FCSTD DOCUMENT  (FreeCAD 1.0R39319 (Git))
Label: externalDesign
License: All rights reserved
LicenseURL: http://en.wikipedia.org/wiki/All_rights_reserved
objects: Part::Feature×136, Sketcher::SketchObject×119, Part::MultiFuse×93, Part::Extrusion×87, Part::Fillet×59, Part::Cut×56, Part::FeaturePython×56, Part::Cylinder×50, Part::Loft×17, App::Part×15, Part::Box×14, Part::Sphere×14, Part::Compound×8, Part::Mirroring×2, Part::Part2DObjectPython×2, Part::MultiCommon×1
note: 833 computed .brp shape members not serialized (recipe doc carries the construction recipe); baked Part::Feature solids carry a one-line shape summary decoded from their .brp

FEATURE [Part::Cylinder] Cylinder198  label="tSlotCut"
  Angle = 360
  AttacherType = Attacher::AttachEngine3D
  FirstAngle = 0
  Height = 10
  Placement = pos=(0,-290.956,1.7236) rot=(1,0,0;0.698132rad)
  Radius = 1.63
  SecondAngle = 0
FEATURE [Part::Feature] Part__Feature328  label="srsCut009"
  Placement = pos=(-31.2,-59.5,20.5) rot=(0,0,1;0rad)
  shape: bbox 22.79 x 8 x 17.08 mm, 886 faces (baked)
FEATURE [Sketcher::SketchObject] Sketch332
  ArcFitTolerance = 0
  FullyConstrained = true
  MakeInternals = false
  sketch-geometry (7):
    g0: LineSegment StartX=45 StartY=-77.9423 StartZ=0 EndX=90 EndY=3.3e-15 EndZ=0
    g1: LineSegment StartX=90 StartY=3.3e-15 StartZ=0 EndX=45 EndY=77.9423 EndZ=0
    g2: LineSegment StartX=45 StartY=77.9423 StartZ=0 EndX=-45 EndY=77.9423 EndZ=0
    g3: LineSegment StartX=-45 StartY=77.9423 StartZ=0 EndX=-90 EndY=1.9e-14 EndZ=0
    g4: LineSegment StartX=-90 StartY=1.9e-14 StartZ=0 EndX=-45 EndY=-77.9423 EndZ=0
    g5: LineSegment StartX=-45 StartY=-77.9423 StartZ=0 EndX=45 EndY=-77.9423 EndZ=0
    g6: Circle [constr] CenterX=0 CenterY=0 CenterZ=0 NormalX=0 NormalY=0 NormalZ=1 AngleXU=0 Radius=90
  constraints (16):
    c: Coincident(g0,g1)
    c: Coincident(g1,g2)
    c: Coincident(g2,g3)
    c: Coincident(g3,g4)
    c: Coincident(g4,g5)
    c: Coincident(g5,g0)
    c: Equal(g0, g1-g5) x5
    c: PointOnObject(g0,g6)
    c: PointOnObject(g1,g6)
    c: PointOnObject(g2,g6)
    c: PointOnObject(g3,g6)
    c: PointOnObject(g4,g6)
    c: PointOnObject(g5,g6)
    c: DistanceX(g5,g5) = 90
    c: Horizontal(g5)
    c: Coincident(g6,g-1)
FEATURE [Sketcher::SketchObject] Sketch333
  ArcFitTolerance = 0
  FullyConstrained = true
  MakeInternals = false
  Placement = pos=(0,0,20) rot=(0,0,1;0rad)
  sketch-geometry (7):
    g0: LineSegment StartX=35 StartY=-60.6218 StartZ=0 EndX=70 EndY=2e-16 EndZ=0
    g1: LineSegment StartX=70 StartY=2e-16 StartZ=0 EndX=35 EndY=60.6218 EndZ=0
    g2: LineSegment StartX=35 StartY=60.6218 StartZ=0 EndX=-35 EndY=60.6218 EndZ=0
    g3: LineSegment StartX=-35 StartY=60.6218 StartZ=0 EndX=-70 EndY=-2.1e-15 EndZ=0
    g4: LineSegment StartX=-70 StartY=0 StartZ=0 EndX=-35 EndY=-60.6218 EndZ=0
    g5: LineSegment StartX=-35 StartY=-60.6218 StartZ=0 EndX=35 EndY=-60.6218 EndZ=0
    g6: Circle [constr] CenterX=0 CenterY=0 CenterZ=0 NormalX=0 NormalY=0 NormalZ=1 AngleXU=0 Radius=70
  constraints (16):
    c: Coincident(g0,g1)
    c: Coincident(g1,g2)
    c: Coincident(g2,g3)
    c: Coincident(g3,g4)
    c: Coincident(g4,g5)
    c: Coincident(g5,g0)
    c: Equal(g0, g1-g5) x5
    c: PointOnObject(g0,g6)
    c: PointOnObject(g1,g6)
    c: PointOnObject(g2,g6)
    c: PointOnObject(g3,g6)
    c: PointOnObject(g4,g6)
    c: PointOnObject(g5,g6)
    c: DistanceX(g5,g5) = 70
    c: Horizontal(g5)
    c: Coincident(g6,g-1)
FEATURE [Part::Loft] Loft
  Closed = false
  MaxDegree = 5
  Ruled = false
  Sections = -> [Sketch333,Sketch332]
  Solid = true
FEATURE [Sketcher::SketchObject] Sketch334
  ArcFitTolerance = 0
  FullyConstrained = true
  MakeInternals = false
  sketch-geometry (7):
    g0: LineSegment StartX=45 StartY=-77.9423 StartZ=0 EndX=90 EndY=3.3e-15 EndZ=0
    g1: LineSegment StartX=90 StartY=0 StartZ=0 EndX=45 EndY=77.9423 EndZ=0
    g2: LineSegment StartX=45 StartY=77.9423 StartZ=0 EndX=-45 EndY=77.9423 EndZ=0
    g3: LineSegment StartX=-45 StartY=77.9423 StartZ=0 EndX=-90 EndY=1.9e-14 EndZ=0
    g4: LineSegment StartX=-90 StartY=1.9e-14 StartZ=0 EndX=-45 EndY=-77.9423 EndZ=0
    g5: LineSegment StartX=-45 StartY=-77.9423 StartZ=0 EndX=45 EndY=-77.9423 EndZ=0
    g6: Circle [constr] CenterX=0 CenterY=0 CenterZ=0 NormalX=0 NormalY=0 NormalZ=1 AngleXU=0 Radius=90
  constraints (16):
    c: Coincident(g0,g1)
    c: Coincident(g1,g2)
    c: Coincident(g2,g3)
    c: Coincident(g3,g4)
    c: Coincident(g4,g5)
    c: Coincident(g5,g0)
    c: Equal(g0, g1-g5) x5
    c: PointOnObject(g0,g6)
    c: PointOnObject(g1,g6)
    c: PointOnObject(g2,g6)
    c: PointOnObject(g3,g6)
    c: PointOnObject(g4,g6)
    c: PointOnObject(g5,g6)
    c: DistanceX(g5,g5) = 90
    c: Horizontal(g5)
    c: Coincident(g6,g-1)
FEATURE [Sketcher::SketchObject] Sketch335
  ArcFitTolerance = 0
  FullyConstrained = true
  MakeInternals = false
  Placement = pos=(0,0,20) rot=(0,0,1;0rad)
  sketch-geometry (7):
    g0: LineSegment StartX=35 StartY=-60.6218 StartZ=0 EndX=70 EndY=2e-16 EndZ=0
    g1: LineSegment StartX=70 StartY=2e-16 StartZ=0 EndX=35 EndY=60.6218 EndZ=0
    g2: LineSegment StartX=35 StartY=60.6218 StartZ=0 EndX=-35 EndY=60.6218 EndZ=0
    g3: LineSegment StartX=-35 StartY=60.6218 StartZ=0 EndX=-70 EndY=-2.1e-15 EndZ=0
    g4: LineSegment StartX=-70 StartY=-2.1e-15 StartZ=0 EndX=-35 EndY=-60.6218 EndZ=0
    g5: LineSegment StartX=-35 StartY=-60.6218 StartZ=0 EndX=35 EndY=-60.6218 EndZ=0
    g6: Circle [constr] CenterX=0 CenterY=0 CenterZ=0 NormalX=0 NormalY=0 NormalZ=1 AngleXU=0 Radius=70
  constraints (16):
    c: Coincident(g0,g1)
    c: Coincident(g1,g2)
    c: Coincident(g2,g3)
    c: Coincident(g3,g4)
    c: Coincident(g4,g5)
    c: Coincident(g5,g0)
    c: Equal(g0, g1-g5) x5
    c: PointOnObject(g0,g6)
    c: PointOnObject(g1,g6)
    c: PointOnObject(g2,g6)
    c: PointOnObject(g3,g6)
    c: PointOnObject(g4,g6)
    c: PointOnObject(g5,g6)
    c: DistanceX(g5,g5) = 70
    c: Horizontal(g5)
    c: Coincident(g6,g-1)
FEATURE [Part::Loft] Loft065
  Closed = false
  MaxDegree = 5
  Placement = pos=(0,0,-4) rot=(0,0,1;0rad)
  Ruled = false
  Sections = -> [Sketch335,Sketch334]
  Solid = true
FEATURE [Part::Cut] Cut124  label="flap"
  Base = -> Loft
  Tool = -> Loft065
FEATURE [Part::Fillet] Fillet216
  Base = -> Cut124
  EdgeLinks = -> Cut124 [Edge1,Edge5,Edge6,Edge7,Edge8,Edge9,Edge27,Edge29,Edge31,Edge33,Edge35,Edge36]
  Edges = 12 edges r=5: [Edge1,Edge5,Edge6,Edge7,Edge8,Edge9,Edge27,Edge29,Edge31,Edge33,Edge35,Edge36]
FEATURE [Part::Fillet] Fillet217
  Base = -> Fillet216
  EdgeLinks = -> Fillet216 [Edge2,Edge6,Edge11,Edge12,Edge13,Edge14,Edge15,Edge16,Edge17,Edge18,Edge19,Edge20]
  Edges = 12 edges r=1: [Edge2,Edge6,Edge11,Edge12,Edge13,Edge14,Edge15,Edge16,Edge17,Edge18,Edge19,Edge20]
FEATURE [Part::Fillet] Fillet218
  Base = -> Fillet217
  EdgeLinks = -> Fillet217 [Edge1,Edge3,Edge5,Edge15,Edge17,Edge41,Edge61,Edge63,Edge65,Edge66,Edge69,Edge70]
  Edges = 12 edges r=2: [Edge1,Edge3,Edge5,Edge15,Edge17,Edge41,Edge61,Edge63,Edge65,Edge66,Edge69,Edge70]
FEATURE [Sketcher::SketchObject] Sketch336
  ArcFitTolerance = 0
  FullyConstrained = false
  MakeInternals = false
  sketch-geometry (7):
    g0: LineSegment StartX=32.5172 StartY=-56.2817 StartZ=0 EndX=65 EndY=0.0199031 EndZ=0
    g1: LineSegment StartX=65 StartY=0.0199031 StartZ=0 EndX=32.4828 EndY=56.3016 EndZ=0
    g2: LineSegment StartX=32.4828 StartY=56.3016 StartZ=0 EndX=-32.5172 EndY=56.2817 EndZ=0
    g3: LineSegment StartX=-32.5172 StartY=56.2817 StartZ=0 EndX=-65 EndY=-0.0199031 EndZ=0
    g4: LineSegment StartX=-65 StartY=-0.0199031 StartZ=0 EndX=-32.4828 EndY=-56.3016 EndZ=0
    g5: LineSegment StartX=-32.4828 StartY=-56.3016 StartZ=0 EndX=32.5172 EndY=-56.2817 EndZ=0
    g6: Circle [constr] CenterX=0 CenterY=0 CenterZ=0 NormalX=0 NormalY=0 NormalZ=1 AngleXU=0 Radius=65
  constraints (15):
    c: Coincident(g0,g1)
    c: Coincident(g1,g2)
    c: Coincident(g2,g3)
    c: Coincident(g3,g4)
    c: Coincident(g4,g5)
    c: Coincident(g5,g0)
    c: Equal(g0, g1-g5) x5
    c: PointOnObject(g0,g6)
    c: PointOnObject(g1,g6)
    c: PointOnObject(g2,g6)
    c: PointOnObject(g3,g6)
    c: PointOnObject(g4,g6)
    c: PointOnObject(g5,g6)
    c: Coincident(g6,g-1)
    c: DistanceX(g2,g2) = 65
FEATURE [Part::Extrusion] Extrude137
  Base = -> Sketch336
  Dir = (0,0,1)
  DirMode = 2
  FaceMakerClass = Part::FaceMakerBullseye
  FaceMakerMode = 3
  LengthFwd = 20
  LengthRev = 0
  Solid = true
  Symmetric = false
FEATURE [Part::Cut] Cut125  label="plate"
  Base = -> Fillet218
  Tool = -> Extrude137
FEATURE [Part::Fillet] Fillet219  label="plate001"
  Base = -> Cut125
  EdgeLinks = -> Cut125 [Edge48,Edge49,Edge50,Edge51,Edge52,Edge53,Edge110,Edge111,Edge112,Edge113,Edge114,Edge115,Edge116,Edge117,Edge118,Edge119,Edge120,Edge121]
  Edges = 18 edges r=1.5: [Edge48,Edge49,Edge50,Edge51,Edge52,Edge53,Edge110,Edge111,Edge112,Edge113,Edge114,Edge115,Edge116,Edge117,Edge118,Edge119,Edge120,Edge121]
FEATURE [Sketcher::SketchObject] Sketch337
  ArcFitTolerance = 0
  FullyConstrained = true
  MakeInternals = false
  sketch-geometry (7):
    g0: LineSegment StartX=45 StartY=-77.9423 StartZ=0 EndX=90 EndY=3.3e-15 EndZ=0
    g1: LineSegment StartX=90 StartY=3.3e-15 StartZ=0 EndX=45 EndY=77.9423 EndZ=0
    g2: LineSegment StartX=45 StartY=77.9423 StartZ=0 EndX=-45 EndY=77.9423 EndZ=0
    g3: LineSegment StartX=-45 StartY=77.9423 StartZ=0 EndX=-90 EndY=1.9e-14 EndZ=0
    g4: LineSegment StartX=-90 StartY=1.9e-14 StartZ=0 EndX=-45 EndY=-77.9423 EndZ=0
    g5: LineSegment StartX=-45 StartY=-77.9423 StartZ=0 EndX=45 EndY=-77.9423 EndZ=0
    g6: Circle [constr] CenterX=0 CenterY=0 CenterZ=0 NormalX=0 NormalY=0 NormalZ=1 AngleXU=0 Radius=90
  constraints (16):
    c: Coincident(g0,g1)
    c: Coincident(g1,g2)
    c: Coincident(g2,g3)
    c: Coincident(g3,g4)
    c: Coincident(g4,g5)
    c: Coincident(g5,g0)
    c: Equal(g0, g1-g5) x5
    c: PointOnObject(g0,g6)
    c: PointOnObject(g1,g6)
    c: PointOnObject(g2,g6)
    c: PointOnObject(g3,g6)
    c: PointOnObject(g4,g6)
    c: PointOnObject(g5,g6)
    c: DistanceX(g5,g5) = 90
    c: Horizontal(g5)
    c: Coincident(g6,g-1)
FEATURE [Sketcher::SketchObject] Sketch338
  ArcFitTolerance = 0
  FullyConstrained = true
  MakeInternals = false
  Placement = pos=(0,0,20) rot=(0,0,1;0rad)
  sketch-geometry (7):
    g0: LineSegment StartX=35 StartY=-60.6218 StartZ=0 EndX=70 EndY=2e-16 EndZ=0
    g1: LineSegment StartX=70 StartY=0 StartZ=0 EndX=35 EndY=60.6218 EndZ=0
    g2: LineSegment StartX=35 StartY=60.6218 StartZ=0 EndX=-35 EndY=60.6218 EndZ=0
    g3: LineSegment StartX=-35 StartY=60.6218 StartZ=0 EndX=-70 EndY=-2.1e-15 EndZ=0
    g4: LineSegment StartX=-70 StartY=0 StartZ=0 EndX=-35 EndY=-60.6218 EndZ=0
    g5: LineSegment StartX=-35 StartY=-60.6218 StartZ=0 EndX=35 EndY=-60.6218 EndZ=0
    g6: Circle [constr] CenterX=0 CenterY=0 CenterZ=0 NormalX=0 NormalY=0 NormalZ=1 AngleXU=0 Radius=70
  constraints (16):
    c: Coincident(g0,g1)
    c: Coincident(g1,g2)
    c: Coincident(g2,g3)
    c: Coincident(g3,g4)
    c: Coincident(g4,g5)
    c: Coincident(g5,g0)
    c: Equal(g0, g1-g5) x5
    c: PointOnObject(g0,g6)
    c: PointOnObject(g1,g6)
    c: PointOnObject(g2,g6)
    c: PointOnObject(g3,g6)
    c: PointOnObject(g4,g6)
    c: PointOnObject(g5,g6)
    c: DistanceX(g5,g5) = 70
    c: Horizontal(g5)
    c: Coincident(g6,g-1)
FEATURE [Part::Loft] Loft066
  Closed = false
  MaxDegree = 5
  Ruled = false
  Sections = -> [Sketch338,Sketch337]
  Solid = true
FEATURE [Sketcher::SketchObject] Sketch339
  ArcFitTolerance = 0
  FullyConstrained = true
  MakeInternals = false
  sketch-geometry (7):
    g0: LineSegment StartX=45 StartY=-77.9423 StartZ=0 EndX=90 EndY=3.3e-15 EndZ=0
    g1: LineSegment StartX=90 StartY=0 StartZ=0 EndX=45 EndY=77.9423 EndZ=0
    g2: LineSegment StartX=45 StartY=77.9423 StartZ=0 EndX=-45 EndY=77.9423 EndZ=0
    g3: LineSegment StartX=-45 StartY=77.9423 StartZ=0 EndX=-90 EndY=1.9e-14 EndZ=0
    g4: LineSegment StartX=-90 StartY=1.42e-14 StartZ=0 EndX=-45 EndY=-77.9423 EndZ=0
    g5: LineSegment StartX=-45 StartY=-77.9423 StartZ=0 EndX=45 EndY=-77.9423 EndZ=0
    g6: Circle [constr] CenterX=0 CenterY=0 CenterZ=0 NormalX=0 NormalY=0 NormalZ=1 AngleXU=0 Radius=90
  constraints (16):
    c: Coincident(g0,g1)
    c: Coincident(g1,g2)
    c: Coincident(g2,g3)
    c: Coincident(g3,g4)
    c: Coincident(g4,g5)
    c: Coincident(g5,g0)
    c: Equal(g0, g1-g5) x5
    c: PointOnObject(g0,g6)
    c: PointOnObject(g1,g6)
    c: PointOnObject(g2,g6)
    c: PointOnObject(g3,g6)
    c: PointOnObject(g4,g6)
    c: PointOnObject(g5,g6)
    c: DistanceX(g5,g5) = 90
    c: Horizontal(g5)
    c: Coincident(g6,g-1)
FEATURE [Sketcher::SketchObject] Sketch340
  ArcFitTolerance = 0
  FullyConstrained = true
  MakeInternals = false
  Placement = pos=(0,0,20) rot=(0,0,1;0rad)
  sketch-geometry (7):
    g0: LineSegment StartX=35 StartY=-60.6218 StartZ=0 EndX=70 EndY=2e-16 EndZ=0
    g1: LineSegment StartX=70 StartY=0 StartZ=0 EndX=35 EndY=60.6218 EndZ=0
    g2: LineSegment StartX=35 StartY=60.6218 StartZ=0 EndX=-35 EndY=60.6218 EndZ=0
    g3: LineSegment StartX=-35 StartY=60.6218 StartZ=0 EndX=-70 EndY=-2.1e-15 EndZ=0
    g4: LineSegment StartX=-70 StartY=0 StartZ=0 EndX=-35 EndY=-60.6218 EndZ=0
    g5: LineSegment StartX=-35 StartY=-60.6218 StartZ=0 EndX=35 EndY=-60.6218 EndZ=0
    g6: Circle [constr] CenterX=0 CenterY=0 CenterZ=0 NormalX=0 NormalY=0 NormalZ=1 AngleXU=0 Radius=70
  constraints (16):
    c: Coincident(g0,g1)
    c: Coincident(g1,g2)
    c: Coincident(g2,g3)
    c: Coincident(g3,g4)
    c: Coincident(g4,g5)
    c: Coincident(g5,g0)
    c: Equal(g0, g1-g5) x5
    c: PointOnObject(g0,g6)
    c: PointOnObject(g1,g6)
    c: PointOnObject(g2,g6)
    c: PointOnObject(g3,g6)
    c: PointOnObject(g4,g6)
    c: PointOnObject(g5,g6)
    c: DistanceX(g5,g5) = 70
    c: Horizontal(g5)
    c: Coincident(g6,g-1)
FEATURE [Part::Loft] Loft067
  Closed = false
  MaxDegree = 5
  Placement = pos=(0,0,-4) rot=(0,0,1;0rad)
  Ruled = false
  Sections = -> [Sketch340,Sketch339]
  Solid = true
FEATURE [Part::Cut] Cut126  label="flap001"
  Base = -> Loft066
  Tool = -> Loft067
FEATURE [Part::Fillet] Fillet220
  Base = -> Cut126
  EdgeLinks = -> Cut126 [Edge1,Edge5,Edge6,Edge7,Edge8,Edge9,Edge27,Edge29,Edge31,Edge33,Edge35,Edge36]
  Edges = 12 edges r=5: [Edge1,Edge5,Edge6,Edge7,Edge8,Edge9,Edge27,Edge29,Edge31,Edge33,Edge35,Edge36]
FEATURE [Part::Fillet] Fillet221
  Base = -> Fillet220
  EdgeLinks = -> Fillet220 [Edge2,Edge6,Edge11,Edge12,Edge13,Edge14,Edge15,Edge16,Edge17,Edge18,Edge19,Edge20]
  Edges = 12 edges r=1: [Edge2,Edge6,Edge11,Edge12,Edge13,Edge14,Edge15,Edge16,Edge17,Edge18,Edge19,Edge20]
FEATURE [Part::Fillet] Fillet222
  Base = -> Fillet221
  EdgeLinks = -> Fillet221 [Edge1,Edge3,Edge5,Edge15,Edge17,Edge41,Edge61,Edge63,Edge65,Edge66,Edge69,Edge70]
  Edges = 12 edges r=2: [Edge1,Edge3,Edge5,Edge15,Edge17,Edge41,Edge61,Edge63,Edge65,Edge66,Edge69,Edge70]
FEATURE [Sketcher::SketchObject] Sketch341
  ArcFitTolerance = 0
  FullyConstrained = false
  MakeInternals = false
  sketch-geometry (7):
    g0: LineSegment StartX=32.5172 StartY=-56.2817 StartZ=0 EndX=65 EndY=0.0199031 EndZ=0
    g1: LineSegment StartX=65 StartY=0.0199031 StartZ=0 EndX=32.4828 EndY=56.3016 EndZ=0
    g2: LineSegment StartX=32.4828 StartY=56.3016 StartZ=0 EndX=-32.5172 EndY=56.2817 EndZ=0
    g3: LineSegment StartX=-32.5172 StartY=56.2817 StartZ=0 EndX=-65 EndY=-0.0199031 EndZ=0
    g4: LineSegment StartX=-65 StartY=-0.0199031 StartZ=0 EndX=-32.4828 EndY=-56.3016 EndZ=0
    g5: LineSegment StartX=-32.4828 StartY=-56.3016 StartZ=0 EndX=32.5172 EndY=-56.2817 EndZ=0
    g6: Circle [constr] CenterX=0 CenterY=0 CenterZ=0 NormalX=0 NormalY=0 NormalZ=1 AngleXU=0 Radius=65
  constraints (15):
    c: Coincident(g0,g1)
    c: Coincident(g1,g2)
    c: Coincident(g2,g3)
    c: Coincident(g3,g4)
    c: Coincident(g4,g5)
    c: Coincident(g5,g0)
    c: Equal(g0, g1-g5) x5
    c: PointOnObject(g0,g6)
    c: PointOnObject(g1,g6)
    c: PointOnObject(g2,g6)
    c: PointOnObject(g3,g6)
    c: PointOnObject(g4,g6)
    c: PointOnObject(g5,g6)
    c: Coincident(g6,g-1)
    c: DistanceX(g2,g2) = 65
FEATURE [Part::Extrusion] Extrude138
  Base = -> Sketch341
  Dir = (0,0,1)
  DirMode = 2
  FaceMakerClass = Part::FaceMakerBullseye
  FaceMakerMode = 3
  LengthFwd = 20
  LengthRev = 0
  Solid = true
  Symmetric = false
FEATURE [Part::Cut] Cut127  label="plate002"
  Base = -> Fillet222
  Tool = -> Extrude138
FEATURE [Part::Fillet] Fillet223  label="plate003"
  Base = -> Cut127
  EdgeLinks = -> Cut127 [Edge48,Edge49,Edge50,Edge51,Edge52,Edge53,Edge110,Edge111,Edge112,Edge113,Edge114,Edge115,Edge116,Edge117,Edge118,Edge119,Edge120,Edge121]
  Edges = 18 edges r=1.5: [Edge48,Edge49,Edge50,Edge51,Edge52,Edge53,Edge110,Edge111,Edge112,Edge113,Edge114,Edge115,Edge116,Edge117,Edge118,Edge119,Edge120,Edge121]
  Placement = pos=(0,0,18) rot=(0,0,1;0rad)
FEATURE [Sketcher::SketchObject] Sketch342
  ArcFitTolerance = 0
  FullyConstrained = true
  MakeInternals = false
  sketch-geometry (7):
    g0: LineSegment StartX=45 StartY=-77.9423 StartZ=0 EndX=90 EndY=3.3e-15 EndZ=0
    g1: LineSegment StartX=90 StartY=0 StartZ=0 EndX=45 EndY=77.9423 EndZ=0
    g2: LineSegment StartX=45 StartY=77.9423 StartZ=0 EndX=-45 EndY=77.9423 EndZ=0
    g3: LineSegment StartX=-45 StartY=77.9423 StartZ=0 EndX=-90 EndY=1.9e-14 EndZ=0
    g4: LineSegment StartX=-90 StartY=1.9e-14 StartZ=0 EndX=-45 EndY=-77.9423 EndZ=0
    g5: LineSegment StartX=-45 StartY=-77.9423 StartZ=0 EndX=45 EndY=-77.9423 EndZ=0
    g6: Circle [constr] CenterX=0 CenterY=0 CenterZ=0 NormalX=0 NormalY=0 NormalZ=1 AngleXU=0 Radius=90
  constraints (16):
    c: Coincident(g0,g1)
    c: Coincident(g1,g2)
    c: Coincident(g2,g3)
    c: Coincident(g3,g4)
    c: Coincident(g4,g5)
    c: Coincident(g5,g0)
    c: Equal(g0, g1-g5) x5
    c: PointOnObject(g0,g6)
    c: PointOnObject(g1,g6)
    c: PointOnObject(g2,g6)
    c: PointOnObject(g3,g6)
    c: PointOnObject(g4,g6)
    c: PointOnObject(g5,g6)
    c: DistanceX(g5,g5) = 90
    c: Horizontal(g5)
    c: Coincident(g6,g-1)
FEATURE [Sketcher::SketchObject] Sketch343
  ArcFitTolerance = 0
  FullyConstrained = true
  MakeInternals = false
  Placement = pos=(0,0,20) rot=(0,0,1;0rad)
  sketch-geometry (7):
    g0: LineSegment StartX=35 StartY=-60.6218 StartZ=0 EndX=70 EndY=2e-16 EndZ=0
    g1: LineSegment StartX=70 StartY=0 StartZ=0 EndX=35 EndY=60.6218 EndZ=0
    g2: LineSegment StartX=35 StartY=60.6218 StartZ=0 EndX=-35 EndY=60.6218 EndZ=0
    g3: LineSegment StartX=-35 StartY=60.6218 StartZ=0 EndX=-70 EndY=-2.1e-15 EndZ=0
    g4: LineSegment StartX=-70 StartY=-2.1e-15 StartZ=0 EndX=-35 EndY=-60.6218 EndZ=0
    g5: LineSegment StartX=-35 StartY=-60.6218 StartZ=0 EndX=35 EndY=-60.6218 EndZ=0
    g6: Circle [constr] CenterX=0 CenterY=0 CenterZ=0 NormalX=0 NormalY=0 NormalZ=1 AngleXU=0 Radius=70
  constraints (16):
    c: Coincident(g0,g1)
    c: Coincident(g1,g2)
    c: Coincident(g2,g3)
    c: Coincident(g3,g4)
    c: Coincident(g4,g5)
    c: Coincident(g5,g0)
    c: Equal(g0, g1-g5) x5
    c: PointOnObject(g0,g6)
    c: PointOnObject(g1,g6)
    c: PointOnObject(g2,g6)
    c: PointOnObject(g3,g6)
    c: PointOnObject(g4,g6)
    c: PointOnObject(g5,g6)
    c: DistanceX(g5,g5) = 70
    c: Horizontal(g5)
    c: Coincident(g6,g-1)
FEATURE [Part::Loft] Loft068
  Closed = false
  MaxDegree = 5
  Ruled = false
  Sections = -> [Sketch343,Sketch342]
  Solid = true
FEATURE [Sketcher::SketchObject] Sketch344
  ArcFitTolerance = 0
  FullyConstrained = true
  MakeInternals = false
  sketch-geometry (7):
    g0: LineSegment StartX=45 StartY=-77.9423 StartZ=0 EndX=90 EndY=3.3e-15 EndZ=0
    g1: LineSegment StartX=90 StartY=3.3e-15 StartZ=0 EndX=45 EndY=77.9423 EndZ=0
    g2: LineSegment StartX=45 StartY=77.9423 StartZ=0 EndX=-45 EndY=77.9423 EndZ=0
    g3: LineSegment StartX=-45 StartY=77.9423 StartZ=0 EndX=-90 EndY=1.9e-14 EndZ=0
    g4: LineSegment StartX=-90 StartY=1.42e-14 StartZ=0 EndX=-45 EndY=-77.9423 EndZ=0
    g5: LineSegment StartX=-45 StartY=-77.9423 StartZ=0 EndX=45 EndY=-77.9423 EndZ=0
    g6: Circle [constr] CenterX=0 CenterY=0 CenterZ=0 NormalX=0 NormalY=0 NormalZ=1 AngleXU=0 Radius=90
  constraints (16):
    c: Coincident(g0,g1)
    c: Coincident(g1,g2)
    c: Coincident(g2,g3)
    c: Coincident(g3,g4)
    c: Coincident(g4,g5)
    c: Coincident(g5,g0)
    c: Equal(g0, g1-g5) x5
    c: PointOnObject(g0,g6)
    c: PointOnObject(g1,g6)
    c: PointOnObject(g2,g6)
    c: PointOnObject(g3,g6)
    c: PointOnObject(g4,g6)
    c: PointOnObject(g5,g6)
    c: DistanceX(g5,g5) = 90
    c: Horizontal(g5)
    c: Coincident(g6,g-1)
FEATURE [Sketcher::SketchObject] Sketch345
  ArcFitTolerance = 0
  FullyConstrained = true
  MakeInternals = false
  Placement = pos=(0,0,20) rot=(0,0,1;0rad)
  sketch-geometry (7):
    g0: LineSegment StartX=35 StartY=-60.6218 StartZ=0 EndX=70 EndY=2e-16 EndZ=0
    g1: LineSegment StartX=70 StartY=0 StartZ=0 EndX=35 EndY=60.6218 EndZ=0
    g2: LineSegment StartX=35 StartY=60.6218 StartZ=0 EndX=-35 EndY=60.6218 EndZ=0
    g3: LineSegment StartX=-35 StartY=60.6218 StartZ=0 EndX=-70 EndY=-2.1e-15 EndZ=0
    g4: LineSegment StartX=-70 StartY=0 StartZ=0 EndX=-35 EndY=-60.6218 EndZ=0
    g5: LineSegment StartX=-35 StartY=-60.6218 StartZ=0 EndX=35 EndY=-60.6218 EndZ=0
    g6: Circle [constr] CenterX=0 CenterY=0 CenterZ=0 NormalX=0 NormalY=0 NormalZ=1 AngleXU=0 Radius=70
  constraints (16):
    c: Coincident(g0,g1)
    c: Coincident(g1,g2)
    c: Coincident(g2,g3)
    c: Coincident(g3,g4)
    c: Coincident(g4,g5)
    c: Coincident(g5,g0)
    c: Equal(g0, g1-g5) x5
    c: PointOnObject(g0,g6)
    c: PointOnObject(g1,g6)
    c: PointOnObject(g2,g6)
    c: PointOnObject(g3,g6)
    c: PointOnObject(g4,g6)
    c: PointOnObject(g5,g6)
    c: DistanceX(g5,g5) = 70
    c: Horizontal(g5)
    c: Coincident(g6,g-1)
FEATURE [Part::Loft] Loft069
  Closed = false
  MaxDegree = 5
  Placement = pos=(0,0,-4) rot=(0,0,1;0rad)
  Ruled = false
  Sections = -> [Sketch345,Sketch344]
  Solid = true
FEATURE [Part::Cut] Cut128  label="flap002"
  Base = -> Loft068
  Tool = -> Loft069
FEATURE [Part::Fillet] Fillet224
  Base = -> Cut128
  EdgeLinks = -> Cut128 [Edge1,Edge5,Edge6,Edge7,Edge8,Edge9,Edge27,Edge29,Edge31,Edge33,Edge35,Edge36]
  Edges = 12 edges r=5: [Edge1,Edge5,Edge6,Edge7,Edge8,Edge9,Edge27,Edge29,Edge31,Edge33,Edge35,Edge36]
FEATURE [Part::Fillet] Fillet225
  Base = -> Fillet224
  EdgeLinks = -> Fillet224 [Edge2,Edge6,Edge11,Edge12,Edge13,Edge14,Edge15,Edge16,Edge17,Edge18,Edge19,Edge20]
  Edges = 12 edges r=1: [Edge2,Edge6,Edge11,Edge12,Edge13,Edge14,Edge15,Edge16,Edge17,Edge18,Edge19,Edge20]
FEATURE [Part::Fillet] Fillet226
  Base = -> Fillet225
  EdgeLinks = -> Fillet225 [Edge1,Edge3,Edge5,Edge15,Edge17,Edge41,Edge61,Edge63,Edge65,Edge66,Edge69,Edge70]
  Edges = 12 edges r=2: [Edge1,Edge3,Edge5,Edge15,Edge17,Edge41,Edge61,Edge63,Edge65,Edge66,Edge69,Edge70]
FEATURE [Sketcher::SketchObject] Sketch346
  ArcFitTolerance = 0
  FullyConstrained = false
  MakeInternals = false
  sketch-geometry (7):
    g0: LineSegment StartX=32.5172 StartY=-56.2817 StartZ=0 EndX=65 EndY=0.0199031 EndZ=0
    g1: LineSegment StartX=65 StartY=0.0199031 StartZ=0 EndX=32.4828 EndY=56.3016 EndZ=0
    g2: LineSegment StartX=32.4828 StartY=56.3016 StartZ=0 EndX=-32.5172 EndY=56.2817 EndZ=0
    g3: LineSegment StartX=-32.5172 StartY=56.2817 StartZ=0 EndX=-65 EndY=-0.0199031 EndZ=0
    g4: LineSegment StartX=-65 StartY=-0.0199031 StartZ=0 EndX=-32.4828 EndY=-56.3016 EndZ=0
    g5: LineSegment StartX=-32.4828 StartY=-56.3016 StartZ=0 EndX=32.5172 EndY=-56.2817 EndZ=0
    g6: Circle [constr] CenterX=0 CenterY=0 CenterZ=0 NormalX=0 NormalY=0 NormalZ=1 AngleXU=0 Radius=65
  constraints (15):
    c: Coincident(g0,g1)
    c: Coincident(g1,g2)
    c: Coincident(g2,g3)
    c: Coincident(g3,g4)
    c: Coincident(g4,g5)
    c: Coincident(g5,g0)
    c: Equal(g0, g1-g5) x5
    c: PointOnObject(g0,g6)
    c: PointOnObject(g1,g6)
    c: PointOnObject(g2,g6)
    c: PointOnObject(g3,g6)
    c: PointOnObject(g4,g6)
    c: PointOnObject(g5,g6)
    c: Coincident(g6,g-1)
    c: DistanceX(g2,g2) = 65
FEATURE [Part::Extrusion] Extrude139
  Base = -> Sketch346
  Dir = (0,0,1)
  DirMode = 2
  FaceMakerClass = Part::FaceMakerBullseye
  FaceMakerMode = 3
  LengthFwd = 20
  LengthRev = 0
  Solid = true
  Symmetric = false
FEATURE [Part::Cut] Cut129  label="plate004"
  Base = -> Fillet226
  Tool = -> Extrude139
FEATURE [Part::Fillet] Fillet227  label="plate005"
  Base = -> Cut129
  EdgeLinks = -> Cut129 [Edge48,Edge49,Edge50,Edge51,Edge52,Edge53,Edge110,Edge111,Edge112,Edge113,Edge114,Edge115,Edge116,Edge117,Edge118,Edge119,Edge120,Edge121]
  Edges = 18 edges r=1.5: [Edge48,Edge49,Edge50,Edge51,Edge52,Edge53,Edge110,Edge111,Edge112,Edge113,Edge114,Edge115,Edge116,Edge117,Edge118,Edge119,Edge120,Edge121]
  Placement = pos=(0,0,36) rot=(0,0,1;0rad)
FEATURE [Sketcher::SketchObject] Sketch347
  ArcFitTolerance = 0
  FullyConstrained = true
  MakeInternals = false
  sketch-geometry (7):
    g0: LineSegment StartX=45 StartY=-77.9423 StartZ=0 EndX=90 EndY=3.3e-15 EndZ=0
    g1: LineSegment StartX=90 StartY=0 StartZ=0 EndX=45 EndY=77.9423 EndZ=0
    g2: LineSegment StartX=45 StartY=77.9423 StartZ=0 EndX=-45 EndY=77.9423 EndZ=0
    g3: LineSegment StartX=-45 StartY=77.9423 StartZ=0 EndX=-90 EndY=1.9e-14 EndZ=0
    g4: LineSegment StartX=-90 StartY=1.9e-14 StartZ=0 EndX=-45 EndY=-77.9423 EndZ=0
    g5: LineSegment StartX=-45 StartY=-77.9423 StartZ=0 EndX=45 EndY=-77.9423 EndZ=0
    g6: Circle [constr] CenterX=0 CenterY=0 CenterZ=0 NormalX=0 NormalY=0 NormalZ=1 AngleXU=0 Radius=90
  constraints (16):
    c: Coincident(g0,g1)
    c: Coincident(g1,g2)
    c: Coincident(g2,g3)
    c: Coincident(g3,g4)
    c: Coincident(g4,g5)
    c: Coincident(g5,g0)
    c: Equal(g0, g1-g5) x5
    c: PointOnObject(g0,g6)
    c: PointOnObject(g1,g6)
    c: PointOnObject(g2,g6)
    c: PointOnObject(g3,g6)
    c: PointOnObject(g4,g6)
    c: PointOnObject(g5,g6)
    c: DistanceX(g5,g5) = 90
    c: Horizontal(g5)
    c: Coincident(g6,g-1)
FEATURE [Sketcher::SketchObject] Sketch348
  ArcFitTolerance = 0
  FullyConstrained = true
  MakeInternals = false
  Placement = pos=(0,0,20) rot=(0,0,1;0rad)
  sketch-geometry (7):
    g0: LineSegment StartX=35 StartY=-60.6218 StartZ=0 EndX=70 EndY=2e-16 EndZ=0
    g1: LineSegment StartX=70 StartY=0 StartZ=0 EndX=35 EndY=60.6218 EndZ=0
    g2: LineSegment StartX=35 StartY=60.6218 StartZ=0 EndX=-35 EndY=60.6218 EndZ=0
    g3: LineSegment StartX=-35 StartY=60.6218 StartZ=0 EndX=-70 EndY=-2.1e-15 EndZ=0
    g4: LineSegment StartX=-70 StartY=-2.1e-15 StartZ=0 EndX=-35 EndY=-60.6218 EndZ=0
    g5: LineSegment StartX=-35 StartY=-60.6218 StartZ=0 EndX=35 EndY=-60.6218 EndZ=0
    g6: Circle [constr] CenterX=0 CenterY=0 CenterZ=0 NormalX=0 NormalY=0 NormalZ=1 AngleXU=0 Radius=70
  constraints (16):
    c: Coincident(g0,g1)
    c: Coincident(g1,g2)
    c: Coincident(g2,g3)
    c: Coincident(g3,g4)
    c: Coincident(g4,g5)
    c: Coincident(g5,g0)
    c: Equal(g0, g1-g5) x5
    c: PointOnObject(g0,g6)
    c: PointOnObject(g1,g6)
    c: PointOnObject(g2,g6)
    c: PointOnObject(g3,g6)
    c: PointOnObject(g4,g6)
    c: PointOnObject(g5,g6)
    c: DistanceX(g5,g5) = 70
    c: Horizontal(g5)
    c: Coincident(g6,g-1)
FEATURE [Part::Loft] Loft070
  Closed = false
  MaxDegree = 5
  Ruled = false
  Sections = -> [Sketch348,Sketch347]
  Solid = true
FEATURE [Sketcher::SketchObject] Sketch349
  ArcFitTolerance = 0
  FullyConstrained = true
  MakeInternals = false
  sketch-geometry (7):
    g0: LineSegment StartX=45 StartY=-77.9423 StartZ=0 EndX=90 EndY=3.3e-15 EndZ=0
    g1: LineSegment StartX=90 StartY=0 StartZ=0 EndX=45 EndY=77.9423 EndZ=0
    g2: LineSegment StartX=45 StartY=77.9423 StartZ=0 EndX=-45 EndY=77.9423 EndZ=0
    g3: LineSegment StartX=-45 StartY=77.9423 StartZ=0 EndX=-90 EndY=1.9e-14 EndZ=0
    g4: LineSegment StartX=-90 StartY=1.9e-14 StartZ=0 EndX=-45 EndY=-77.9423 EndZ=0
    g5: LineSegment StartX=-45 StartY=-77.9423 StartZ=0 EndX=45 EndY=-77.9423 EndZ=0
    g6: Circle [constr] CenterX=0 CenterY=0 CenterZ=0 NormalX=0 NormalY=0 NormalZ=1 AngleXU=0 Radius=90
  constraints (16):
    c: Coincident(g0,g1)
    c: Coincident(g1,g2)
    c: Coincident(g2,g3)
    c: Coincident(g3,g4)
    c: Coincident(g4,g5)
    c: Coincident(g5,g0)
    c: Equal(g0, g1-g5) x5
    c: PointOnObject(g0,g6)
    c: PointOnObject(g1,g6)
    c: PointOnObject(g2,g6)
    c: PointOnObject(g3,g6)
    c: PointOnObject(g4,g6)
    c: PointOnObject(g5,g6)
    c: DistanceX(g5,g5) = 90
    c: Horizontal(g5)
    c: Coincident(g6,g-1)
FEATURE [Sketcher::SketchObject] Sketch350
  ArcFitTolerance = 0
  FullyConstrained = true
  MakeInternals = false
  Placement = pos=(0,0,20) rot=(0,0,1;0rad)
  sketch-geometry (7):
    g0: LineSegment StartX=35 StartY=-60.6218 StartZ=0 EndX=70 EndY=2e-16 EndZ=0
    g1: LineSegment StartX=70 StartY=0 StartZ=0 EndX=35 EndY=60.6218 EndZ=0
    g2: LineSegment StartX=35 StartY=60.6218 StartZ=0 EndX=-35 EndY=60.6218 EndZ=0
    g3: LineSegment StartX=-35 StartY=60.6218 StartZ=0 EndX=-70 EndY=-2.1e-15 EndZ=0
    g4: LineSegment StartX=-70 StartY=-2.1e-15 StartZ=0 EndX=-35 EndY=-60.6218 EndZ=0
    g5: LineSegment StartX=-35 StartY=-60.6218 StartZ=0 EndX=35 EndY=-60.6218 EndZ=0
    g6: Circle [constr] CenterX=0 CenterY=0 CenterZ=0 NormalX=0 NormalY=0 NormalZ=1 AngleXU=0 Radius=70
  constraints (16):
    c: Coincident(g0,g1)
    c: Coincident(g1,g2)
    c: Coincident(g2,g3)
    c: Coincident(g3,g4)
    c: Coincident(g4,g5)
    c: Coincident(g5,g0)
    c: Equal(g0, g1-g5) x5
    c: PointOnObject(g0,g6)
    c: PointOnObject(g1,g6)
    c: PointOnObject(g2,g6)
    c: PointOnObject(g3,g6)
    c: PointOnObject(g4,g6)
    c: PointOnObject(g5,g6)
    c: DistanceX(g5,g5) = 70
    c: Horizontal(g5)
    c: Coincident(g6,g-1)
FEATURE [Part::Loft] Loft071
  Closed = false
  MaxDegree = 5
  Placement = pos=(0,0,-4) rot=(0,0,1;0rad)
  Ruled = false
  Sections = -> [Sketch350,Sketch349]
  Solid = true
FEATURE [Part::Cut] Cut130  label="flap003"
  Base = -> Loft070
  Tool = -> Loft071
FEATURE [Part::Fillet] Fillet228
  Base = -> Cut130
  EdgeLinks = -> Cut130 [Edge1,Edge5,Edge6,Edge7,Edge8,Edge9,Edge27,Edge29,Edge31,Edge33,Edge35,Edge36]
  Edges = 12 edges r=5: [Edge1,Edge5,Edge6,Edge7,Edge8,Edge9,Edge27,Edge29,Edge31,Edge33,Edge35,Edge36]
FEATURE [Part::Fillet] Fillet229
  Base = -> Fillet228
  EdgeLinks = -> Fillet228 [Edge2,Edge6,Edge11,Edge12,Edge13,Edge14,Edge15,Edge16,Edge17,Edge18,Edge19,Edge20]
  Edges = 12 edges r=1: [Edge2,Edge6,Edge11,Edge12,Edge13,Edge14,Edge15,Edge16,Edge17,Edge18,Edge19,Edge20]
FEATURE [Part::Fillet] Fillet230
  Base = -> Fillet229
  EdgeLinks = -> Fillet229 [Edge1,Edge3,Edge5,Edge15,Edge17,Edge41,Edge61,Edge63,Edge65,Edge66,Edge69,Edge70]
  Edges = 12 edges r=2: [Edge1,Edge3,Edge5,Edge15,Edge17,Edge41,Edge61,Edge63,Edge65,Edge66,Edge69,Edge70]
FEATURE [Sketcher::SketchObject] Sketch351
  ArcFitTolerance = 0
  FullyConstrained = false
  MakeInternals = false
  sketch-geometry (7):
    g0: LineSegment StartX=32.5172 StartY=-56.2817 StartZ=0 EndX=65 EndY=0.0199031 EndZ=0
    g1: LineSegment StartX=65 StartY=0.0199031 StartZ=0 EndX=32.4828 EndY=56.3016 EndZ=0
    g2: LineSegment StartX=32.4828 StartY=56.3016 StartZ=0 EndX=-32.5172 EndY=56.2817 EndZ=0
    g3: LineSegment StartX=-32.5172 StartY=56.2817 StartZ=0 EndX=-65 EndY=-0.0199031 EndZ=0
    g4: LineSegment StartX=-65 StartY=-0.0199031 StartZ=0 EndX=-32.4828 EndY=-56.3016 EndZ=0
    g5: LineSegment StartX=-32.4828 StartY=-56.3016 StartZ=0 EndX=32.5172 EndY=-56.2817 EndZ=0
    g6: Circle [constr] CenterX=0 CenterY=0 CenterZ=0 NormalX=0 NormalY=0 NormalZ=1 AngleXU=0 Radius=65
  constraints (15):
    c: Coincident(g0,g1)
    c: Coincident(g1,g2)
    c: Coincident(g2,g3)
    c: Coincident(g3,g4)
    c: Coincident(g4,g5)
    c: Coincident(g5,g0)
    c: Equal(g0, g1-g5) x5
    c: PointOnObject(g0,g6)
    c: PointOnObject(g1,g6)
    c: PointOnObject(g2,g6)
    c: PointOnObject(g3,g6)
    c: PointOnObject(g4,g6)
    c: PointOnObject(g5,g6)
    c: Coincident(g6,g-1)
    c: DistanceX(g2,g2) = 65
FEATURE [Part::Extrusion] Extrude140
  Base = -> Sketch351
  Dir = (0,0,1)
  DirMode = 2
  FaceMakerClass = Part::FaceMakerBullseye
  FaceMakerMode = 3
  LengthFwd = 20
  LengthRev = 0
  Solid = true
  Symmetric = false
FEATURE [Part::Cut] Cut131  label="plate006"
  Base = -> Fillet230
  Tool = -> Extrude140
FEATURE [Part::Fillet] Fillet231  label="plate007"
  Base = -> Cut131
  EdgeLinks = -> Cut131 [Edge48,Edge49,Edge50,Edge51,Edge52,Edge53,Edge110,Edge111,Edge112,Edge113,Edge114,Edge115,Edge116,Edge117,Edge118,Edge119,Edge120,Edge121]
  Edges = 18 edges r=1.5: [Edge48,Edge49,Edge50,Edge51,Edge52,Edge53,Edge110,Edge111,Edge112,Edge113,Edge114,Edge115,Edge116,Edge117,Edge118,Edge119,Edge120,Edge121]
  Placement = pos=(0,0,54) rot=(0,0,1;0rad)
FEATURE [Sketcher::SketchObject] Sketch352
  ArcFitTolerance = 0
  FullyConstrained = true
  MakeInternals = false
  sketch-geometry (7):
    g0: LineSegment StartX=45 StartY=-77.9423 StartZ=0 EndX=90 EndY=3.3e-15 EndZ=0
    g1: LineSegment StartX=90 StartY=0 StartZ=0 EndX=45 EndY=77.9423 EndZ=0
    g2: LineSegment StartX=45 StartY=77.9423 StartZ=0 EndX=-45 EndY=77.9423 EndZ=0
    g3: LineSegment StartX=-45 StartY=77.9423 StartZ=0 EndX=-90 EndY=1.9e-14 EndZ=0
    g4: LineSegment StartX=-90 StartY=1.9e-14 StartZ=0 EndX=-45 EndY=-77.9423 EndZ=0
    g5: LineSegment StartX=-45 StartY=-77.9423 StartZ=0 EndX=45 EndY=-77.9423 EndZ=0
    g6: Circle [constr] CenterX=0 CenterY=0 CenterZ=0 NormalX=0 NormalY=0 NormalZ=1 AngleXU=0 Radius=90
  constraints (16):
    c: Coincident(g0,g1)
    c: Coincident(g1,g2)
    c: Coincident(g2,g3)
    c: Coincident(g3,g4)
    c: Coincident(g4,g5)
    c: Coincident(g5,g0)
    c: Equal(g0, g1-g5) x5
    c: PointOnObject(g0,g6)
    c: PointOnObject(g1,g6)
    c: PointOnObject(g2,g6)
    c: PointOnObject(g3,g6)
    c: PointOnObject(g4,g6)
    c: PointOnObject(g5,g6)
    c: DistanceX(g5,g5) = 90
    c: Horizontal(g5)
    c: Coincident(g6,g-1)
FEATURE [Sketcher::SketchObject] Sketch353
  ArcFitTolerance = 0
  FullyConstrained = true
  MakeInternals = false
  Placement = pos=(0,0,20) rot=(0,0,1;0rad)
  sketch-geometry (7):
    g0: LineSegment StartX=35 StartY=-60.6218 StartZ=0 EndX=70 EndY=2e-16 EndZ=0
    g1: LineSegment StartX=70 StartY=0 StartZ=0 EndX=35 EndY=60.6218 EndZ=0
    g2: LineSegment StartX=35 StartY=60.6218 StartZ=0 EndX=-35 EndY=60.6218 EndZ=0
    g3: LineSegment StartX=-35 StartY=60.6218 StartZ=0 EndX=-70 EndY=-2.1e-15 EndZ=0
    g4: LineSegment StartX=-70 StartY=0 StartZ=0 EndX=-35 EndY=-60.6218 EndZ=0
    g5: LineSegment StartX=-35 StartY=-60.6218 StartZ=0 EndX=35 EndY=-60.6218 EndZ=0
    g6: Circle [constr] CenterX=0 CenterY=0 CenterZ=0 NormalX=0 NormalY=0 NormalZ=1 AngleXU=0 Radius=70
  constraints (16):
    c: Coincident(g0,g1)
    c: Coincident(g1,g2)
    c: Coincident(g2,g3)
    c: Coincident(g3,g4)
    c: Coincident(g4,g5)
    c: Coincident(g5,g0)
    c: Equal(g0, g1-g5) x5
    c: PointOnObject(g0,g6)
    c: PointOnObject(g1,g6)
    c: PointOnObject(g2,g6)
    c: PointOnObject(g3,g6)
    c: PointOnObject(g4,g6)
    c: PointOnObject(g5,g6)
    c: DistanceX(g5,g5) = 70
    c: Horizontal(g5)
    c: Coincident(g6,g-1)
FEATURE [Part::Loft] Loft072
  Closed = false
  MaxDegree = 5
  Ruled = false
  Sections = -> [Sketch353,Sketch352]
  Solid = true
FEATURE [Sketcher::SketchObject] Sketch354
  ArcFitTolerance = 0
  FullyConstrained = true
  MakeInternals = false
  sketch-geometry (7):
    g0: LineSegment StartX=45 StartY=-77.9423 StartZ=0 EndX=90 EndY=3.3e-15 EndZ=0
    g1: LineSegment StartX=90 StartY=0 StartZ=0 EndX=45 EndY=77.9423 EndZ=0
    g2: LineSegment StartX=45 StartY=77.9423 StartZ=0 EndX=-45 EndY=77.9423 EndZ=0
    g3: LineSegment StartX=-45 StartY=77.9423 StartZ=0 EndX=-90 EndY=1.9e-14 EndZ=0
    g4: LineSegment StartX=-90 StartY=1.42e-14 StartZ=0 EndX=-45 EndY=-77.9423 EndZ=0
    g5: LineSegment StartX=-45 StartY=-77.9423 StartZ=0 EndX=45 EndY=-77.9423 EndZ=0
    g6: Circle [constr] CenterX=0 CenterY=0 CenterZ=0 NormalX=0 NormalY=0 NormalZ=1 AngleXU=0 Radius=90
  constraints (16):
    c: Coincident(g0,g1)
    c: Coincident(g1,g2)
    c: Coincident(g2,g3)
    c: Coincident(g3,g4)
    c: Coincident(g4,g5)
    c: Coincident(g5,g0)
    c: Equal(g0, g1-g5) x5
    c: PointOnObject(g0,g6)
    c: PointOnObject(g1,g6)
    c: PointOnObject(g2,g6)
    c: PointOnObject(g3,g6)
    c: PointOnObject(g4,g6)
    c: PointOnObject(g5,g6)
    c: DistanceX(g5,g5) = 90
    c: Horizontal(g5)
    c: Coincident(g6,g-1)
FEATURE [Sketcher::SketchObject] Sketch355
  ArcFitTolerance = 0
  FullyConstrained = true
  MakeInternals = false
  Placement = pos=(0,0,20) rot=(0,0,1;0rad)
  sketch-geometry (7):
    g0: LineSegment StartX=35 StartY=-60.6218 StartZ=0 EndX=70 EndY=2e-16 EndZ=0
    g1: LineSegment StartX=70 StartY=0 StartZ=0 EndX=35 EndY=60.6218 EndZ=0
    g2: LineSegment StartX=35 StartY=60.6218 StartZ=0 EndX=-35 EndY=60.6218 EndZ=0
    g3: LineSegment StartX=-35 StartY=60.6218 StartZ=0 EndX=-70 EndY=-2.1e-15 EndZ=0
    g4: LineSegment StartX=-70 StartY=0 StartZ=0 EndX=-35 EndY=-60.6218 EndZ=0
    g5: LineSegment StartX=-35 StartY=-60.6218 StartZ=0 EndX=35 EndY=-60.6218 EndZ=0
    g6: Circle [constr] CenterX=0 CenterY=0 CenterZ=0 NormalX=0 NormalY=0 NormalZ=1 AngleXU=0 Radius=70
  constraints (16):
    c: Coincident(g0,g1)
    c: Coincident(g1,g2)
    c: Coincident(g2,g3)
    c: Coincident(g3,g4)
    c: Coincident(g4,g5)
    c: Coincident(g5,g0)
    c: Equal(g0, g1-g5) x5
    c: PointOnObject(g0,g6)
    c: PointOnObject(g1,g6)
    c: PointOnObject(g2,g6)
    c: PointOnObject(g3,g6)
    c: PointOnObject(g4,g6)
    c: PointOnObject(g5,g6)
    c: DistanceX(g5,g5) = 70
    c: Horizontal(g5)
    c: Coincident(g6,g-1)
FEATURE [Part::Loft] Loft073
  Closed = false
  MaxDegree = 5
  Placement = pos=(0,0,-4) rot=(0,0,1;0rad)
  Ruled = false
  Sections = -> [Sketch355,Sketch354]
  Solid = true
FEATURE [Part::Cut] Cut132  label="flap004"
  Base = -> Loft072
  Tool = -> Loft073
FEATURE [Part::Fillet] Fillet232
  Base = -> Cut132
  EdgeLinks = -> Cut132 [Edge1,Edge5,Edge6,Edge7,Edge8,Edge9,Edge27,Edge29,Edge31,Edge33,Edge35,Edge36]
  Edges = 12 edges r=5: [Edge1,Edge5,Edge6,Edge7,Edge8,Edge9,Edge27,Edge29,Edge31,Edge33,Edge35,Edge36]
FEATURE [Part::Fillet] Fillet233
  Base = -> Fillet232
  EdgeLinks = -> Fillet232 [Edge2,Edge6,Edge11,Edge12,Edge13,Edge14,Edge15,Edge16,Edge17,Edge18,Edge19,Edge20]
  Edges = 12 edges r=1: [Edge2,Edge6,Edge11,Edge12,Edge13,Edge14,Edge15,Edge16,Edge17,Edge18,Edge19,Edge20]
FEATURE [Part::Fillet] Fillet234
  Base = -> Fillet233
  EdgeLinks = -> Fillet233 [Edge1,Edge3,Edge5,Edge15,Edge17,Edge41,Edge61,Edge63,Edge65,Edge66,Edge69,Edge70]
  Edges = 12 edges r=2: [Edge1,Edge3,Edge5,Edge15,Edge17,Edge41,Edge61,Edge63,Edge65,Edge66,Edge69,Edge70]
FEATURE [Sketcher::SketchObject] Sketch356
  ArcFitTolerance = 0
  FullyConstrained = false
  MakeInternals = false
  sketch-geometry (7):
    g0: LineSegment StartX=32.5172 StartY=-56.2817 StartZ=0 EndX=65 EndY=0.0199031 EndZ=0
    g1: LineSegment StartX=65 StartY=0.0199031 StartZ=0 EndX=32.4828 EndY=56.3016 EndZ=0
    g2: LineSegment StartX=32.4828 StartY=56.3016 StartZ=0 EndX=-32.5172 EndY=56.2817 EndZ=0
    g3: LineSegment StartX=-32.5172 StartY=56.2817 StartZ=0 EndX=-65 EndY=-0.0199031 EndZ=0
    g4: LineSegment StartX=-65 StartY=-0.0199031 StartZ=0 EndX=-32.4828 EndY=-56.3016 EndZ=0
    g5: LineSegment StartX=-32.4828 StartY=-56.3016 StartZ=0 EndX=32.5172 EndY=-56.2817 EndZ=0
    g6: Circle [constr] CenterX=0 CenterY=0 CenterZ=0 NormalX=0 NormalY=0 NormalZ=1 AngleXU=0 Radius=65
  constraints (15):
    c: Coincident(g0,g1)
    c: Coincident(g1,g2)
    c: Coincident(g2,g3)
    c: Coincident(g3,g4)
    c: Coincident(g4,g5)
    c: Coincident(g5,g0)
    c: Equal(g0, g1-g5) x5
    c: PointOnObject(g0,g6)
    c: PointOnObject(g1,g6)
    c: PointOnObject(g2,g6)
    c: PointOnObject(g3,g6)
    c: PointOnObject(g4,g6)
    c: PointOnObject(g5,g6)
    c: Coincident(g6,g-1)
    c: DistanceX(g2,g2) = 65
FEATURE [Part::Extrusion] Extrude141
  Base = -> Sketch356
  Dir = (0,0,1)
  DirMode = 2
  FaceMakerClass = Part::FaceMakerBullseye
  FaceMakerMode = 3
  LengthFwd = 20
  LengthRev = 0
  Solid = true
  Symmetric = false
FEATURE [Part::Cut] Cut133  label="plate008"
  Base = -> Fillet234
  Tool = -> Extrude141
FEATURE [Part::Fillet] Fillet235  label="plate009"
  Base = -> Cut133
  EdgeLinks = -> Cut133 [Edge48,Edge49,Edge50,Edge51,Edge52,Edge53,Edge110,Edge111,Edge112,Edge113,Edge114,Edge115,Edge116,Edge117,Edge118,Edge119,Edge120,Edge121]
  Edges = 18 edges r=1.5: [Edge48,Edge49,Edge50,Edge51,Edge52,Edge53,Edge110,Edge111,Edge112,Edge113,Edge114,Edge115,Edge116,Edge117,Edge118,Edge119,Edge120,Edge121]
  Placement = pos=(0,0,72) rot=(0,0,1;0rad)
FEATURE [Sketcher::SketchObject] Sketch357
  ArcFitTolerance = 0
  FullyConstrained = true
  MakeInternals = false
  sketch-geometry (7):
    g0: LineSegment StartX=45 StartY=-77.9423 StartZ=0 EndX=90 EndY=3.3e-15 EndZ=0
    g1: LineSegment StartX=90 StartY=3.3e-15 StartZ=0 EndX=45 EndY=77.9423 EndZ=0
    g2: LineSegment StartX=45 StartY=77.9423 StartZ=0 EndX=-45 EndY=77.9423 EndZ=0
    g3: LineSegment StartX=-45 StartY=77.9423 StartZ=0 EndX=-90 EndY=1.9e-14 EndZ=0
    g4: LineSegment StartX=-90 StartY=1.9e-14 StartZ=0 EndX=-45 EndY=-77.9423 EndZ=0
    g5: LineSegment StartX=-45 StartY=-77.9423 StartZ=0 EndX=45 EndY=-77.9423 EndZ=0
    g6: Circle [constr] CenterX=0 CenterY=0 CenterZ=0 NormalX=0 NormalY=0 NormalZ=1 AngleXU=0 Radius=90
  constraints (16):
    c: Coincident(g0,g1)
    c: Coincident(g1,g2)
    c: Coincident(g2,g3)
    c: Coincident(g3,g4)
    c: Coincident(g4,g5)
    c: Coincident(g5,g0)
    c: Equal(g0, g1-g5) x5
    c: PointOnObject(g0,g6)
    c: PointOnObject(g1,g6)
    c: PointOnObject(g2,g6)
    c: PointOnObject(g3,g6)
    c: PointOnObject(g4,g6)
    c: PointOnObject(g5,g6)
    c: DistanceX(g5,g5) = 90
    c: Horizontal(g5)
    c: Coincident(g6,g-1)
FEATURE [Sketcher::SketchObject] Sketch358
  ArcFitTolerance = 0
  FullyConstrained = true
  MakeInternals = false
  Placement = pos=(0,0,20) rot=(0,0,1;0rad)
  sketch-geometry (7):
    g0: LineSegment StartX=35 StartY=-60.6218 StartZ=0 EndX=70 EndY=2e-16 EndZ=0
    g1: LineSegment StartX=70 StartY=2e-16 StartZ=0 EndX=35 EndY=60.6218 EndZ=0
    g2: LineSegment StartX=35 StartY=60.6218 StartZ=0 EndX=-35 EndY=60.6218 EndZ=0
    g3: LineSegment StartX=-35 StartY=60.6218 StartZ=0 EndX=-70 EndY=-2.1e-15 EndZ=0
    g4: LineSegment StartX=-70 StartY=0 StartZ=0 EndX=-35 EndY=-60.6218 EndZ=0
    g5: LineSegment StartX=-35 StartY=-60.6218 StartZ=0 EndX=35 EndY=-60.6218 EndZ=0
    g6: Circle [constr] CenterX=0 CenterY=0 CenterZ=0 NormalX=0 NormalY=0 NormalZ=1 AngleXU=0 Radius=70
  constraints (16):
    c: Coincident(g0,g1)
    c: Coincident(g1,g2)
    c: Coincident(g2,g3)
    c: Coincident(g3,g4)
    c: Coincident(g4,g5)
    c: Coincident(g5,g0)
    c: Equal(g0, g1-g5) x5
    c: PointOnObject(g0,g6)
    c: PointOnObject(g1,g6)
    c: PointOnObject(g2,g6)
    c: PointOnObject(g3,g6)
    c: PointOnObject(g4,g6)
    c: PointOnObject(g5,g6)
    c: DistanceX(g5,g5) = 70
    c: Horizontal(g5)
    c: Coincident(g6,g-1)
FEATURE [Part::Loft] Loft074
  Closed = false
  MaxDegree = 5
  Ruled = false
  Sections = -> [Sketch358,Sketch357]
  Solid = true
FEATURE [Sketcher::SketchObject] Sketch359
  ArcFitTolerance = 0
  FullyConstrained = true
  MakeInternals = false
  sketch-geometry (7):
    g0: LineSegment StartX=45 StartY=-77.9423 StartZ=0 EndX=90 EndY=3.3e-15 EndZ=0
    g1: LineSegment StartX=90 StartY=0 StartZ=0 EndX=45 EndY=77.9423 EndZ=0
    g2: LineSegment StartX=45 StartY=77.9423 StartZ=0 EndX=-45 EndY=77.9423 EndZ=0
    g3: LineSegment StartX=-45 StartY=77.9423 StartZ=0 EndX=-90 EndY=1.9e-14 EndZ=0
    g4: LineSegment StartX=-90 StartY=1.9e-14 StartZ=0 EndX=-45 EndY=-77.9423 EndZ=0
    g5: LineSegment StartX=-45 StartY=-77.9423 StartZ=0 EndX=45 EndY=-77.9423 EndZ=0
    g6: Circle [constr] CenterX=0 CenterY=0 CenterZ=0 NormalX=0 NormalY=0 NormalZ=1 AngleXU=0 Radius=90
  constraints (16):
    c: Coincident(g0,g1)
    c: Coincident(g1,g2)
    c: Coincident(g2,g3)
    c: Coincident(g3,g4)
    c: Coincident(g4,g5)
    c: Coincident(g5,g0)
    c: Equal(g0, g1-g5) x5
    c: PointOnObject(g0,g6)
    c: PointOnObject(g1,g6)
    c: PointOnObject(g2,g6)
    c: PointOnObject(g3,g6)
    c: PointOnObject(g4,g6)
    c: PointOnObject(g5,g6)
    c: DistanceX(g5,g5) = 90
    c: Horizontal(g5)
    c: Coincident(g6,g-1)
FEATURE [Sketcher::SketchObject] Sketch360
  ArcFitTolerance = 0
  FullyConstrained = true
  MakeInternals = false
  Placement = pos=(0,0,20) rot=(0,0,1;0rad)
  sketch-geometry (7):
    g0: LineSegment StartX=35 StartY=-60.6218 StartZ=0 EndX=70 EndY=2e-16 EndZ=0
    g1: LineSegment StartX=70 StartY=0 StartZ=0 EndX=35 EndY=60.6218 EndZ=0
    g2: LineSegment StartX=35 StartY=60.6218 StartZ=0 EndX=-35 EndY=60.6218 EndZ=0
    g3: LineSegment StartX=-35 StartY=60.6218 StartZ=0 EndX=-70 EndY=-2.1e-15 EndZ=0
    g4: LineSegment StartX=-70 StartY=0 StartZ=0 EndX=-35 EndY=-60.6218 EndZ=0
    g5: LineSegment StartX=-35 StartY=-60.6218 StartZ=0 EndX=35 EndY=-60.6218 EndZ=0
    g6: Circle [constr] CenterX=0 CenterY=0 CenterZ=0 NormalX=0 NormalY=0 NormalZ=1 AngleXU=0 Radius=70
  constraints (16):
    c: Coincident(g0,g1)
    c: Coincident(g1,g2)
    c: Coincident(g2,g3)
    c: Coincident(g3,g4)
    c: Coincident(g4,g5)
    c: Coincident(g5,g0)
    c: Equal(g0, g1-g5) x5
    c: PointOnObject(g0,g6)
    c: PointOnObject(g1,g6)
    c: PointOnObject(g2,g6)
    c: PointOnObject(g3,g6)
    c: PointOnObject(g4,g6)
    c: PointOnObject(g5,g6)
    c: DistanceX(g5,g5) = 70
    c: Horizontal(g5)
    c: Coincident(g6,g-1)
FEATURE [Part::Loft] Loft075
  Closed = false
  MaxDegree = 5
  Placement = pos=(0,0,-4) rot=(0,0,1;0rad)
  Ruled = false
  Sections = -> [Sketch360,Sketch359]
  Solid = true
FEATURE [Part::Cut] Cut134  label="flap005"
  Base = -> Loft074
  Tool = -> Loft075
FEATURE [Part::Fillet] Fillet236
  Base = -> Cut134
  EdgeLinks = -> Cut134 [Edge1,Edge5,Edge6,Edge7,Edge8,Edge9,Edge27,Edge29,Edge31,Edge33,Edge35,Edge36]
  Edges = 12 edges r=5: [Edge1,Edge5,Edge6,Edge7,Edge8,Edge9,Edge27,Edge29,Edge31,Edge33,Edge35,Edge36]
FEATURE [Part::Fillet] Fillet237
  Base = -> Fillet236
  EdgeLinks = -> Fillet236 [Edge2,Edge6,Edge11,Edge12,Edge13,Edge14,Edge15,Edge16,Edge17,Edge18,Edge19,Edge20]
  Edges = 12 edges r=1: [Edge2,Edge6,Edge11,Edge12,Edge13,Edge14,Edge15,Edge16,Edge17,Edge18,Edge19,Edge20]
FEATURE [Part::Fillet] Fillet238
  Base = -> Fillet237
  EdgeLinks = -> Fillet237 [Edge1,Edge3,Edge5,Edge15,Edge17,Edge41,Edge61,Edge63,Edge65,Edge66,Edge69,Edge70]
  Edges = 12 edges r=2: [Edge1,Edge3,Edge5,Edge15,Edge17,Edge41,Edge61,Edge63,Edge65,Edge66,Edge69,Edge70]
FEATURE [Sketcher::SketchObject] Sketch361
  ArcFitTolerance = 0
  FullyConstrained = false
  MakeInternals = false
  sketch-geometry (7):
    g0: LineSegment StartX=32.5172 StartY=-56.2817 StartZ=0 EndX=65 EndY=0.0199031 EndZ=0
    g1: LineSegment StartX=65 StartY=0.0199031 StartZ=0 EndX=32.4828 EndY=56.3016 EndZ=0
    g2: LineSegment StartX=32.4828 StartY=56.3016 StartZ=0 EndX=-32.5172 EndY=56.2817 EndZ=0
    g3: LineSegment StartX=-32.5172 StartY=56.2817 StartZ=0 EndX=-65 EndY=-0.0199031 EndZ=0
    g4: LineSegment StartX=-65 StartY=-0.0199031 StartZ=0 EndX=-32.4828 EndY=-56.3016 EndZ=0
    g5: LineSegment StartX=-32.4828 StartY=-56.3016 StartZ=0 EndX=32.5172 EndY=-56.2817 EndZ=0
    g6: Circle [constr] CenterX=0 CenterY=0 CenterZ=0 NormalX=0 NormalY=0 NormalZ=1 AngleXU=0 Radius=65
  constraints (15):
    c: Coincident(g0,g1)
    c: Coincident(g1,g2)
    c: Coincident(g2,g3)
    c: Coincident(g3,g4)
    c: Coincident(g4,g5)
    c: Coincident(g5,g0)
    c: Equal(g0, g1-g5) x5
    c: PointOnObject(g0,g6)
    c: PointOnObject(g1,g6)
    c: PointOnObject(g2,g6)
    c: PointOnObject(g3,g6)
    c: PointOnObject(g4,g6)
    c: PointOnObject(g5,g6)
    c: Coincident(g6,g-1)
    c: DistanceX(g2,g2) = 65
FEATURE [Part::Extrusion] Extrude142
  Base = -> Sketch361
  Dir = (0,0,1)
  DirMode = 2
  FaceMakerClass = Part::FaceMakerBullseye
  FaceMakerMode = 3
  LengthFwd = 20
  LengthRev = 0
  Solid = true
  Symmetric = false
FEATURE [Part::Cut] Cut135  label="plate010"
  Base = -> Fillet238
  Tool = -> Extrude142
FEATURE [Part::Fillet] Fillet239  label="plate011"
  Base = -> Cut135
  EdgeLinks = -> Cut135 [Edge48,Edge49,Edge50,Edge51,Edge52,Edge53,Edge110,Edge111,Edge112,Edge113,Edge114,Edge115,Edge116,Edge117,Edge118,Edge119,Edge120,Edge121]
  Edges = 18 edges r=1.5: [Edge48,Edge49,Edge50,Edge51,Edge52,Edge53,Edge110,Edge111,Edge112,Edge113,Edge114,Edge115,Edge116,Edge117,Edge118,Edge119,Edge120,Edge121]
  Placement = pos=(0,0,90) rot=(0,0,1;0rad)
FEATURE [Sketcher::SketchObject] Sketch362
  ArcFitTolerance = 0
  FullyConstrained = true
  MakeInternals = false
  sketch-geometry (7):
    g0: LineSegment StartX=45 StartY=-77.9423 StartZ=0 EndX=90 EndY=3.3e-15 EndZ=0
    g1: LineSegment StartX=90 StartY=0 StartZ=0 EndX=45 EndY=77.9423 EndZ=0
    g2: LineSegment StartX=45 StartY=77.9423 StartZ=0 EndX=-45 EndY=77.9423 EndZ=0
    g3: LineSegment StartX=-45 StartY=77.9423 StartZ=0 EndX=-90 EndY=1.9e-14 EndZ=0
    g4: LineSegment StartX=-90 StartY=1.42e-14 StartZ=0 EndX=-45 EndY=-77.9423 EndZ=0
    g5: LineSegment StartX=-45 StartY=-77.9423 StartZ=0 EndX=45 EndY=-77.9423 EndZ=0
    g6: Circle [constr] CenterX=0 CenterY=0 CenterZ=0 NormalX=0 NormalY=0 NormalZ=1 AngleXU=0 Radius=90
  constraints (16):
    c: Coincident(g0,g1)
    c: Coincident(g1,g2)
    c: Coincident(g2,g3)
    c: Coincident(g3,g4)
    c: Coincident(g4,g5)
    c: Coincident(g5,g0)
    c: Equal(g0, g1-g5) x5
    c: PointOnObject(g0,g6)
    c: PointOnObject(g1,g6)
    c: PointOnObject(g2,g6)
    c: PointOnObject(g3,g6)
    c: PointOnObject(g4,g6)
    c: PointOnObject(g5,g6)
    c: DistanceX(g5,g5) = 90
    c: Horizontal(g5)
    c: Coincident(g6,g-1)
FEATURE [Sketcher::SketchObject] Sketch363
  ArcFitTolerance = 0
  FullyConstrained = true
  MakeInternals = false
  Placement = pos=(0,0,20) rot=(0,0,1;0rad)
  sketch-geometry (7):
    g0: LineSegment StartX=35 StartY=-60.6218 StartZ=0 EndX=70 EndY=2e-16 EndZ=0
    g1: LineSegment StartX=70 StartY=2e-16 StartZ=0 EndX=35 EndY=60.6218 EndZ=0
    g2: LineSegment StartX=35 StartY=60.6218 StartZ=0 EndX=-35 EndY=60.6218 EndZ=0
    g3: LineSegment StartX=-35 StartY=60.6218 StartZ=0 EndX=-70 EndY=-2.1e-15 EndZ=0
    g4: LineSegment StartX=-70 StartY=-2.1e-15 StartZ=0 EndX=-35 EndY=-60.6218 EndZ=0
    g5: LineSegment StartX=-35 StartY=-60.6218 StartZ=0 EndX=35 EndY=-60.6218 EndZ=0
    g6: Circle [constr] CenterX=0 CenterY=0 CenterZ=0 NormalX=0 NormalY=0 NormalZ=1 AngleXU=0 Radius=70
  constraints (16):
    c: Coincident(g0,g1)
    c: Coincident(g1,g2)
    c: Coincident(g2,g3)
    c: Coincident(g3,g4)
    c: Coincident(g4,g5)
    c: Coincident(g5,g0)
    c: Equal(g0, g1-g5) x5
    c: PointOnObject(g0,g6)
    c: PointOnObject(g1,g6)
    c: PointOnObject(g2,g6)
    c: PointOnObject(g3,g6)
    c: PointOnObject(g4,g6)
    c: PointOnObject(g5,g6)
    c: DistanceX(g5,g5) = 70
    c: Horizontal(g5)
    c: Coincident(g6,g-1)
FEATURE [Part::Loft] Loft076
  Closed = false
  MaxDegree = 5
  Ruled = false
  Sections = -> [Sketch363,Sketch362]
  Solid = true
FEATURE [Sketcher::SketchObject] Sketch364
  ArcFitTolerance = 0
  FullyConstrained = true
  MakeInternals = false
  sketch-geometry (7):
    g0: LineSegment StartX=45 StartY=-77.9423 StartZ=0 EndX=90 EndY=3.3e-15 EndZ=0
    g1: LineSegment StartX=90 StartY=3.3e-15 StartZ=0 EndX=45 EndY=77.9423 EndZ=0
    g2: LineSegment StartX=45 StartY=77.9423 StartZ=0 EndX=-45 EndY=77.9423 EndZ=0
    g3: LineSegment StartX=-45 StartY=77.9423 StartZ=0 EndX=-90 EndY=1.9e-14 EndZ=0
    g4: LineSegment StartX=-90 StartY=1.42e-14 StartZ=0 EndX=-45 EndY=-77.9423 EndZ=0
    g5: LineSegment StartX=-45 StartY=-77.9423 StartZ=0 EndX=45 EndY=-77.9423 EndZ=0
    g6: Circle [constr] CenterX=0 CenterY=0 CenterZ=0 NormalX=0 NormalY=0 NormalZ=1 AngleXU=0 Radius=90
  constraints (16):
    c: Coincident(g0,g1)
    c: Coincident(g1,g2)
    c: Coincident(g2,g3)
    c: Coincident(g3,g4)
    c: Coincident(g4,g5)
    c: Coincident(g5,g0)
    c: Equal(g0, g1-g5) x5
    c: PointOnObject(g0,g6)
    c: PointOnObject(g1,g6)
    c: PointOnObject(g2,g6)
    c: PointOnObject(g3,g6)
    c: PointOnObject(g4,g6)
    c: PointOnObject(g5,g6)
    c: DistanceX(g5,g5) = 90
    c: Horizontal(g5)
    c: Coincident(g6,g-1)
FEATURE [Sketcher::SketchObject] Sketch365
  ArcFitTolerance = 0
  FullyConstrained = true
  MakeInternals = false
  Placement = pos=(0,0,20) rot=(0,0,1;0rad)
  sketch-geometry (7):
    g0: LineSegment StartX=35 StartY=-60.6218 StartZ=0 EndX=70 EndY=2e-16 EndZ=0
    g1: LineSegment StartX=70 StartY=2e-16 StartZ=0 EndX=35 EndY=60.6218 EndZ=0
    g2: LineSegment StartX=35 StartY=60.6218 StartZ=0 EndX=-35 EndY=60.6218 EndZ=0
    g3: LineSegment StartX=-35 StartY=60.6218 StartZ=0 EndX=-70 EndY=-2.1e-15 EndZ=0
    g4: LineSegment StartX=-70 StartY=-2.1e-15 StartZ=0 EndX=-35 EndY=-60.6218 EndZ=0
    g5: LineSegment StartX=-35 StartY=-60.6218 StartZ=0 EndX=35 EndY=-60.6218 EndZ=0
    g6: Circle [constr] CenterX=0 CenterY=0 CenterZ=0 NormalX=0 NormalY=0 NormalZ=1 AngleXU=0 Radius=70
  constraints (16):
    c: Coincident(g0,g1)
    c: Coincident(g1,g2)
    c: Coincident(g2,g3)
    c: Coincident(g3,g4)
    c: Coincident(g4,g5)
    c: Coincident(g5,g0)
    c: Equal(g0, g1-g5) x5
    c: PointOnObject(g0,g6)
    c: PointOnObject(g1,g6)
    c: PointOnObject(g2,g6)
    c: PointOnObject(g3,g6)
    c: PointOnObject(g4,g6)
    c: PointOnObject(g5,g6)
    c: DistanceX(g5,g5) = 70
    c: Horizontal(g5)
    c: Coincident(g6,g-1)
FEATURE [Part::Loft] Loft077
  Closed = false
  MaxDegree = 5
  Placement = pos=(0,0,-4) rot=(0,0,1;0rad)
  Ruled = false
  Sections = -> [Sketch365,Sketch364]
  Solid = true
FEATURE [Part::Cut] Cut136  label="flap006"
  Base = -> Loft076
  Tool = -> Loft077
FEATURE [Part::Fillet] Fillet240
  Base = -> Cut136
  EdgeLinks = -> Cut136 [Edge1,Edge5,Edge6,Edge7,Edge8,Edge9,Edge27,Edge29,Edge31,Edge33,Edge35,Edge36]
  Edges = 12 edges r=5: [Edge1,Edge5,Edge6,Edge7,Edge8,Edge9,Edge27,Edge29,Edge31,Edge33,Edge35,Edge36]
FEATURE [Part::Fillet] Fillet241
  Base = -> Fillet240
  EdgeLinks = -> Fillet240 [Edge2,Edge6,Edge11,Edge12,Edge13,Edge14,Edge15,Edge16,Edge17,Edge18,Edge19,Edge20]
  Edges = 12 edges r=1: [Edge2,Edge6,Edge11,Edge12,Edge13,Edge14,Edge15,Edge16,Edge17,Edge18,Edge19,Edge20]
FEATURE [Part::Fillet] Fillet242
  Base = -> Fillet241
  EdgeLinks = -> Fillet241 [Edge1,Edge3,Edge5,Edge15,Edge17,Edge41,Edge61,Edge63,Edge65,Edge66,Edge69,Edge70]
  Edges = 12 edges r=2: [Edge1,Edge3,Edge5,Edge15,Edge17,Edge41,Edge61,Edge63,Edge65,Edge66,Edge69,Edge70]
FEATURE [Sketcher::SketchObject] Sketch366
  ArcFitTolerance = 0
  FullyConstrained = false
  MakeInternals = false
  sketch-geometry (7):
    g0: LineSegment StartX=32.5172 StartY=-56.2817 StartZ=0 EndX=65 EndY=0.0199031 EndZ=0
    g1: LineSegment StartX=65 StartY=0.0199031 StartZ=0 EndX=32.4828 EndY=56.3016 EndZ=0
    g2: LineSegment StartX=32.4828 StartY=56.3016 StartZ=0 EndX=-32.5172 EndY=56.2817 EndZ=0
    g3: LineSegment StartX=-32.5172 StartY=56.2817 StartZ=0 EndX=-65 EndY=-0.0199031 EndZ=0
    g4: LineSegment StartX=-65 StartY=-0.0199031 StartZ=0 EndX=-32.4828 EndY=-56.3016 EndZ=0
    g5: LineSegment StartX=-32.4828 StartY=-56.3016 StartZ=0 EndX=32.5172 EndY=-56.2817 EndZ=0
    g6: Circle [constr] CenterX=0 CenterY=0 CenterZ=0 NormalX=0 NormalY=0 NormalZ=1 AngleXU=0 Radius=65
  constraints (15):
    c: Coincident(g0,g1)
    c: Coincident(g1,g2)
    c: Coincident(g2,g3)
    c: Coincident(g3,g4)
    c: Coincident(g4,g5)
    c: Coincident(g5,g0)
    c: Equal(g0, g1-g5) x5
    c: PointOnObject(g0,g6)
    c: PointOnObject(g1,g6)
    c: PointOnObject(g2,g6)
    c: PointOnObject(g3,g6)
    c: PointOnObject(g4,g6)
    c: PointOnObject(g5,g6)
    c: Coincident(g6,g-1)
    c: DistanceX(g2,g2) = 65
FEATURE [Part::Extrusion] Extrude143
  Base = -> Sketch366
  Dir = (0,0,1)
  DirMode = 2
  FaceMakerClass = Part::FaceMakerBullseye
  FaceMakerMode = 3
  LengthFwd = 16
  LengthRev = 0
  Solid = true
  Symmetric = false
FEATURE [Part::Cut] Cut137  label="base"
  Base = -> Fillet242
  Placement = pos=(0,0,-5) rot=(0,0,1;0rad)
  Tool = -> Extrude143
FEATURE [Sketcher::SketchObject] Sketch367
  ArcFitTolerance = 0
  FullyConstrained = true
  MakeInternals = false
  sketch-geometry (7):
    g0: LineSegment StartX=45 StartY=-77.9423 StartZ=0 EndX=90 EndY=3.3e-15 EndZ=0
    g1: LineSegment StartX=90 StartY=3.3e-15 StartZ=0 EndX=45 EndY=77.9423 EndZ=0
    g2: LineSegment StartX=45 StartY=77.9423 StartZ=0 EndX=-45 EndY=77.9423 EndZ=0
    g3: LineSegment StartX=-45 StartY=77.9423 StartZ=0 EndX=-90 EndY=1.9e-14 EndZ=0
    g4: LineSegment StartX=-90 StartY=1.9e-14 StartZ=0 EndX=-45 EndY=-77.9423 EndZ=0
    g5: LineSegment StartX=-45 StartY=-77.9423 StartZ=0 EndX=45 EndY=-77.9423 EndZ=0
    g6: Circle [constr] CenterX=0 CenterY=0 CenterZ=0 NormalX=0 NormalY=0 NormalZ=1 AngleXU=0 Radius=90
  constraints (16):
    c: Coincident(g0,g1)
    c: Coincident(g1,g2)
    c: Coincident(g2,g3)
    c: Coincident(g3,g4)
    c: Coincident(g4,g5)
    c: Coincident(g5,g0)
    c: Equal(g0, g1-g5) x5
    c: PointOnObject(g0,g6)
    c: PointOnObject(g1,g6)
    c: PointOnObject(g2,g6)
    c: PointOnObject(g3,g6)
    c: PointOnObject(g4,g6)
    c: PointOnObject(g5,g6)
    c: DistanceX(g5,g5) = 90
    c: Horizontal(g5)
    c: Coincident(g6,g-1)
FEATURE [Sketcher::SketchObject] Sketch368
  ArcFitTolerance = 0
  FullyConstrained = true
  MakeInternals = false
  Placement = pos=(0,0,20) rot=(0,0,1;0rad)
  sketch-geometry (7):
    g0: LineSegment StartX=35 StartY=-60.6218 StartZ=0 EndX=70 EndY=2e-16 EndZ=0
    g1: LineSegment StartX=70 StartY=2e-16 StartZ=0 EndX=35 EndY=60.6218 EndZ=0
    g2: LineSegment StartX=35 StartY=60.6218 StartZ=0 EndX=-35 EndY=60.6218 EndZ=0
    g3: LineSegment StartX=-35 StartY=60.6218 StartZ=0 EndX=-70 EndY=-2.1e-15 EndZ=0
    g4: LineSegment StartX=-70 StartY=0 StartZ=0 EndX=-35 EndY=-60.6218 EndZ=0
    g5: LineSegment StartX=-35 StartY=-60.6218 StartZ=0 EndX=35 EndY=-60.6218 EndZ=0
    g6: Circle [constr] CenterX=0 CenterY=0 CenterZ=0 NormalX=0 NormalY=0 NormalZ=1 AngleXU=0 Radius=70
  constraints (16):
    c: Coincident(g0,g1)
    c: Coincident(g1,g2)
    c: Coincident(g2,g3)
    c: Coincident(g3,g4)
    c: Coincident(g4,g5)
    c: Coincident(g5,g0)
    c: Equal(g0, g1-g5) x5
    c: PointOnObject(g0,g6)
    c: PointOnObject(g1,g6)
    c: PointOnObject(g2,g6)
    c: PointOnObject(g3,g6)
    c: PointOnObject(g4,g6)
    c: PointOnObject(g5,g6)
    c: DistanceX(g5,g5) = 70
    c: Horizontal(g5)
    c: Coincident(g6,g-1)
FEATURE [Part::Loft] Loft078
  Closed = false
  MaxDegree = 5
  Ruled = false
  Sections = -> [Sketch368,Sketch367]
  Solid = true
FEATURE [Sketcher::SketchObject] Sketch369
  ArcFitTolerance = 0
  FullyConstrained = true
  MakeInternals = false
  sketch-geometry (7):
    g0: LineSegment StartX=45 StartY=-77.9423 StartZ=0 EndX=90 EndY=3.3e-15 EndZ=0
    g1: LineSegment StartX=90 StartY=0 StartZ=0 EndX=45 EndY=77.9423 EndZ=0
    g2: LineSegment StartX=45 StartY=77.9423 StartZ=0 EndX=-45 EndY=77.9423 EndZ=0
    g3: LineSegment StartX=-45 StartY=77.9423 StartZ=0 EndX=-90 EndY=1.9e-14 EndZ=0
    g4: LineSegment StartX=-90 StartY=1.9e-14 StartZ=0 EndX=-45 EndY=-77.9423 EndZ=0
    g5: LineSegment StartX=-45 StartY=-77.9423 StartZ=0 EndX=45 EndY=-77.9423 EndZ=0
    g6: Circle [constr] CenterX=0 CenterY=0 CenterZ=0 NormalX=0 NormalY=0 NormalZ=1 AngleXU=0 Radius=90
  constraints (16):
    c: Coincident(g0,g1)
    c: Coincident(g1,g2)
    c: Coincident(g2,g3)
    c: Coincident(g3,g4)
    c: Coincident(g4,g5)
    c: Coincident(g5,g0)
    c: Equal(g0, g1-g5) x5
    c: PointOnObject(g0,g6)
    c: PointOnObject(g1,g6)
    c: PointOnObject(g2,g6)
    c: PointOnObject(g3,g6)
    c: PointOnObject(g4,g6)
    c: PointOnObject(g5,g6)
    c: DistanceX(g5,g5) = 90
    c: Horizontal(g5)
    c: Coincident(g6,g-1)
FEATURE [Sketcher::SketchObject] Sketch370
  ArcFitTolerance = 0
  FullyConstrained = true
  MakeInternals = false
  Placement = pos=(0,0,20) rot=(0,0,1;0rad)
  sketch-geometry (7):
    g0: LineSegment StartX=35 StartY=-60.6218 StartZ=0 EndX=70 EndY=2e-16 EndZ=0
    g1: LineSegment StartX=70 StartY=0 StartZ=0 EndX=35 EndY=60.6218 EndZ=0
    g2: LineSegment StartX=35 StartY=60.6218 StartZ=0 EndX=-35 EndY=60.6218 EndZ=0
    g3: LineSegment StartX=-35 StartY=60.6218 StartZ=0 EndX=-70 EndY=-2.1e-15 EndZ=0
    g4: LineSegment StartX=-70 StartY=0 StartZ=0 EndX=-35 EndY=-60.6218 EndZ=0
    g5: LineSegment StartX=-35 StartY=-60.6218 StartZ=0 EndX=35 EndY=-60.6218 EndZ=0
    g6: Circle [constr] CenterX=0 CenterY=0 CenterZ=0 NormalX=0 NormalY=0 NormalZ=1 AngleXU=0 Radius=70
  constraints (16):
    c: Coincident(g0,g1)
    c: Coincident(g1,g2)
    c: Coincident(g2,g3)
    c: Coincident(g3,g4)
    c: Coincident(g4,g5)
    c: Coincident(g5,g0)
    c: Equal(g0, g1-g5) x5
    c: PointOnObject(g0,g6)
    c: PointOnObject(g1,g6)
    c: PointOnObject(g2,g6)
    c: PointOnObject(g3,g6)
    c: PointOnObject(g4,g6)
    c: PointOnObject(g5,g6)
    c: DistanceX(g5,g5) = 70
    c: Horizontal(g5)
    c: Coincident(g6,g-1)
FEATURE [Part::Loft] Loft079
  Closed = false
  MaxDegree = 5
  Placement = pos=(0,0,-4) rot=(0,0,1;0rad)
  Ruled = false
  Sections = -> [Sketch370,Sketch369]
  Solid = true
FEATURE [Part::Cut] Cut138  label="flap007"
  Base = -> Loft078
  Tool = -> Loft079
FEATURE [Part::Fillet] Fillet243
  Base = -> Cut138
  EdgeLinks = -> Cut138 [Edge1,Edge5,Edge6,Edge7,Edge8,Edge9,Edge27,Edge29,Edge31,Edge33,Edge35,Edge36]
  Edges = 12 edges r=5: [Edge1,Edge5,Edge6,Edge7,Edge8,Edge9,Edge27,Edge29,Edge31,Edge33,Edge35,Edge36]
FEATURE [Part::Fillet] Fillet244
  Base = -> Fillet243
  EdgeLinks = -> Fillet243 [Edge2,Edge6,Edge11,Edge12,Edge13,Edge14,Edge15,Edge16,Edge17,Edge18,Edge19,Edge20]
  Edges = 12 edges r=1: [Edge2,Edge6,Edge11,Edge12,Edge13,Edge14,Edge15,Edge16,Edge17,Edge18,Edge19,Edge20]
FEATURE [Part::Fillet] Fillet245
  Base = -> Fillet244
  EdgeLinks = -> Fillet244 [Edge1,Edge3,Edge17,Edge61,Edge65,Edge69,Edge70]
  Edges = 7 edges r=2: [Edge1,Edge3,Edge17,Edge61,Edge65,Edge69,Edge70]
FEATURE [Sketcher::SketchObject] Sketch371
  ArcFitTolerance = 0
  FullyConstrained = false
  MakeInternals = false
  sketch-geometry (7):
    g0: LineSegment StartX=32.5172 StartY=-56.2817 StartZ=0 EndX=65 EndY=0.0199031 EndZ=0
    g1: LineSegment StartX=65 StartY=0.0199031 StartZ=0 EndX=32.4828 EndY=56.3016 EndZ=0
    g2: LineSegment StartX=32.4828 StartY=56.3016 StartZ=0 EndX=-32.5172 EndY=56.2817 EndZ=0
    g3: LineSegment StartX=-32.5172 StartY=56.2817 StartZ=0 EndX=-65 EndY=-0.0199031 EndZ=0
    g4: LineSegment StartX=-65 StartY=-0.0199031 StartZ=0 EndX=-32.4828 EndY=-56.3016 EndZ=0
    g5: LineSegment StartX=-32.4828 StartY=-56.3016 StartZ=0 EndX=32.5172 EndY=-56.2817 EndZ=0
    g6: Circle [constr] CenterX=0 CenterY=0 CenterZ=0 NormalX=0 NormalY=0 NormalZ=1 AngleXU=0 Radius=65
  constraints (15):
    c: Coincident(g0,g1)
    c: Coincident(g1,g2)
    c: Coincident(g2,g3)
    c: Coincident(g3,g4)
    c: Coincident(g4,g5)
    c: Coincident(g5,g0)
    c: Equal(g0, g1-g5) x5
    c: PointOnObject(g0,g6)
    c: PointOnObject(g1,g6)
    c: PointOnObject(g2,g6)
    c: PointOnObject(g3,g6)
    c: PointOnObject(g4,g6)
    c: PointOnObject(g5,g6)
    c: Coincident(g6,g-1)
    c: DistanceX(g2,g2) = 65
FEATURE [Part::Extrusion] Extrude144
  Base = -> Sketch371
  Dir = (0,0,1)
  DirMode = 2
  FaceMakerClass = Part::FaceMakerBullseye
  FaceMakerMode = 3
  LengthFwd = 16
  LengthRev = 0
  Solid = true
  Symmetric = false
FEATURE [Part::Cut] Cut139  label="top"
  Base = -> Fillet245
  Placement = pos=(0,0,108) rot=(0,0,1;0rad)
  Tool = -> Extrude144
FEATURE [Sketcher::SketchObject] Sketch372
  ArcFitTolerance = 0
  FullyConstrained = true
  MakeInternals = false
  Placement = pos=(22,0,0) rot=(0.57735,0.57735,0.57735;2.0944rad)
  sketch-geometry (4):
    g0: LineSegment StartX=-285 StartY=-10 StartZ=0 EndX=-279 EndY=-10 EndZ=0
    g1: LineSegment StartX=-279 StartY=-10 StartZ=0 EndX=-279 EndY=10 EndZ=0
    g2: LineSegment StartX=-279 StartY=10 StartZ=0 EndX=-285 EndY=4.5 EndZ=0
    g3: LineSegment StartX=-285 StartY=4.5 StartZ=0 EndX=-285 EndY=-10 EndZ=0
  constraints (12):
    c: Horizontal(g0)
    c: Coincident(g1,g0)
    c: Vertical(g1)
    c: Coincident(g2,g1)
    c: Coincident(g3,g2)
    c: Coincident(g3,g0)
    c: Vertical(g3)
    c: DistanceX(g0) = -285
    c: DistanceY(g0) = -10
    c: DistanceX(g0,g0) = 6
    c: DistanceY(g2) = 4.5
    c: DistanceY(g1) = 10
FEATURE [Part::Extrusion] Extrude145  label="tSlotCut001"
  Base = -> Sketch372
  Dir = (1,0,0)
  DirMode = 2
  FaceMakerClass = Part::FaceMakerBullseye
  FaceMakerMode = 3
  LengthFwd = 44
  LengthRev = 0
  Reversed = true
  Solid = true
  Symmetric = false
FEATURE [Sketcher::SketchObject] Sketch375  label="logoPanel007"
  ArcFitTolerance = 0
  FullyConstrained = true
  MakeInternals = false
  Placement = pos=(0,0,-126) rot=(0,0,1;0rad)
  sketch-geometry (4):
    g0: LineSegment StartX=29.9062 StartY=-352 StartZ=0 EndX=27 EndY=-348 EndZ=0
    g1: LineSegment StartX=-27 StartY=-348 StartZ=0 EndX=-29.9062 EndY=-352 EndZ=0
    g2: LineSegment StartX=29.9062 StartY=-352 StartZ=0 EndX=-29.9062 EndY=-352 EndZ=0
    g3: LineSegment StartX=-27 StartY=-348 StartZ=0 EndX=27 EndY=-348 EndZ=0
  constraints (12):
    c: DistanceY(g1) = -352
    c: DistanceY(g1) = -348
    c: Coincident(g2,g0)
    c: Coincident(g2,g1)
    c: Horizontal(g2)
    c: Angle(g2,g1) = 0.942478
    c: Angle(g0,g2) = 0.942478
    c: DistanceX(g1) = -27
    c: DistanceX(g0) = 27
    c: Coincident(g3,g1)
    c: Coincident(g3,g0)
    c: Horizontal(g3)
FEATURE [Part::Extrusion] Extrude148  label="srsIn"
  Base = -> Sketch375
  Dir = (0,0,1)
  DirMode = 2
  FaceMakerClass = Part::FaceMakerBullseye
  FaceMakerMode = 3
  LengthFwd = 38
  LengthRev = 0
  Placement = pos=(0,292.5,144) rot=(0,0,1;0rad)
  Solid = true
  Symmetric = false
FEATURE [Sketcher::SketchObject] Sketch377
  ArcFitTolerance = 0
  FullyConstrained = true
  MakeInternals = false
  Placement = pos=(0,-234,0) rot=(1,0,0;1.5708rad)
  sketch-geometry (8):
    g0: LineSegment StartX=-13 StartY=10 StartZ=0 EndX=13 EndY=10 EndZ=0
    g1: LineSegment StartX=13 StartY=10 StartZ=0 EndX=13 EndY=-16 EndZ=0
    g2: LineSegment StartX=13 StartY=-16 StartZ=0 EndX=-13 EndY=-16 EndZ=0
    g3: LineSegment StartX=-13 StartY=-16 StartZ=0 EndX=-13 EndY=10 EndZ=0
    g4: LineSegment StartX=-20 StartY=-20 StartZ=0 EndX=-20 EndY=17 EndZ=0
    g5: LineSegment StartX=-20 StartY=17 StartZ=0 EndX=20 EndY=17 EndZ=0
    g6: LineSegment StartX=20 StartY=17 StartZ=0 EndX=20 EndY=-20 EndZ=0
    g7: LineSegment StartX=-20 StartY=-20 StartZ=0 EndX=20 EndY=-20 EndZ=0
  constraints (24):
    c: Coincident(g0,g1)
    c: Coincident(g1,g2)
    c: Coincident(g2,g3)
    c: Coincident(g3,g0)
    c: Horizontal(g0)
    c: Horizontal(g2)
    c: Vertical(g1)
    c: Vertical(g3)
    c: DistanceY(g2,g0) = 26
    c: DistanceX(g0,g0) = 26
    c: DistanceX(g0) = -13
    c: Vertical(g4)
    c: Coincident(g5,g4)
    c: Horizontal(g5)
    c: DistanceX(g4,g0) = 7
    c: DistanceY(g0,g4) = 7
    c: DistanceX(g0,g5) = 7
    c: DistanceY(g4) = -20
    c: Coincident(g6,g5)
    c: Vertical(g6)
    c: Coincident(g7,g4)
    c: Coincident(g7,g6)
    c: Horizontal(g7)
    c: DistanceY(g2) = -16
FEATURE [Part::Extrusion] Extrude150  label="tSlotHold005"
  Base = -> Sketch377
  Dir = (0,-1,2e-16)
  DirMode = 2
  FaceMakerClass = Part::FaceMakerBullseye
  FaceMakerMode = 3
  LengthFwd = 45
  LengthRev = 0
  Solid = true
  Symmetric = false
FEATURE [Sketcher::SketchObject] Sketch378
  ArcFitTolerance = 0
  FullyConstrained = true
  MakeInternals = false
  Placement = pos=(-20,0,0) rot=(0.57735,0.57735,0.57735;2.0944rad)
  sketch-geometry (8):
    g0: LineSegment StartX=-299.827 StartY=3.70134 StartZ=0 EndX=-297.77 EndY=1.25 EndZ=0
    g1: LineSegment StartX=-297.77 StartY=1.25 StartZ=0 EndX=-279 EndY=17 EndZ=0
    g2: LineSegment StartX=-299.827 StartY=3.70134 StartZ=0 EndX=-328.073 EndY=-20 EndZ=0
    g3: LineSegment StartX=-328.073 StartY=-20 StartZ=0 EndX=-279 EndY=-20 EndZ=0
    g4: LineSegment StartX=-279 StartY=-20 StartZ=0 EndX=-279 EndY=17 EndZ=0
    g5: LineSegment StartX=-305 StartY=-10 StartZ=0 EndX=-285 EndY=-10 EndZ=0
    g6: LineSegment StartX=-285 StartY=-10 StartZ=0 EndX=-285 EndY=6.78199 EndZ=0
    g7: LineSegment StartX=-285 StartY=6.78199 StartZ=0 EndX=-305 EndY=-10 EndZ=0
  constraints (24):
    c: Coincident(g1,g0)
    c: DistanceX(g1) = -279
    c: DistanceY(g1) = 17
    c: Angle(g1,g0) = 1.5708
    c: Angle(g1) = 0.698132
    c: Distance(g0) = 3.2
    c: DistanceY(g0) = 1.25
    c: Coincident(g2,g0)
    c: DistanceY(g2) = -20
    c: Coincident(g3,g2)
    c: Horizontal(g3)
    c: Coincident(g4,g3)
    c: Coincident(g4,g1)
    c: Vertical(g4)
    c: Angle(g3,g2) = 0.698132
    c: Horizontal(g5)
    c: Coincident(g6,g5)
    c: Vertical(g6)
    c: Coincident(g7,g6)
    c: Coincident(g7,g5)
    c: DistanceY(g2,g5) = 10
    c: Angle(g5,g7) = 0.698132
    c: DistanceX(g5,g5) = 20
    c: DistanceX(g5) = -305
FEATURE [Part::Extrusion] Extrude152  label="tSlotIn"
  Base = -> Sketch378
  Dir = (1,0,0)
  DirMode = 2
  FaceMakerClass = Part::FaceMakerBullseye
  FaceMakerMode = 3
  LengthFwd = 40
  LengthRev = 0
  Solid = true
  Symmetric = false
FEATURE [Sketcher::SketchObject] Sketch379
  ArcFitTolerance = 0
  FullyConstrained = true
  MakeInternals = false
  Placement = pos=(0,0,-20) rot=(0,0,1;0rad)
  sketch-geometry (5):
    g0: LineSegment StartX=20 StartY=-256.531 StartZ=0 EndX=20 EndY=-234 EndZ=0
    g1: LineSegment StartX=20 StartY=-234 StartZ=0 EndX=-20 EndY=-234 EndZ=0
    g2: LineSegment StartX=-20 StartY=-234 StartZ=0 EndX=-20 EndY=-256.531 EndZ=0
    g3: LineSegment StartX=-20 StartY=-256.531 StartZ=0 EndX=3e-16 EndY=-242 EndZ=0
    g4: LineSegment StartX=3e-16 StartY=-242 StartZ=0 EndX=20 EndY=-256.531 EndZ=0
  constraints (15):
    c: Vertical(g0)
    c: Coincident(g1,g0)
    c: Horizontal(g1)
    c: Coincident(g2,g1)
    c: Vertical(g2)
    c: Coincident(g3,g2)
    c: PointOnObject(g3,g-2)
    c: Coincident(g4,g3)
    c: Coincident(g4,g0)
    c: Angle(g3,g4) = 1.88496
    c: DistanceY(g3) = -242
    c: DistanceY(g2,g0) = 0
    c: DistanceX(g2) = -20
    c: DistanceX(g0) = 20
    c: DistanceY(g1) = -234
FEATURE [Part::Extrusion] Extrude151  label="tSllotHoldCut002"
  Base = -> Sketch379
  Dir = (0,0,1)
  DirMode = 2
  FaceMakerClass = Part::FaceMakerBullseye
  FaceMakerMode = 3
  LengthFwd = 37
  LengthRev = 0
  Solid = true
  Symmetric = false
FEATURE [Part::Cut] Cut140  label="tSlotHold004"
  Base = -> Extrude150
  Tool = -> Extrude151
FEATURE [Sketcher::SketchObject] Sketch380
  ArcFitTolerance = 0
  FullyConstrained = true
  MakeInternals = false
  sketch-geometry (14):
    g0: LineSegment StartX=5 StartY=-8.66025 StartZ=0 EndX=10 EndY=3.18e-14 EndZ=0
    g1: LineSegment StartX=10 StartY=3.18e-14 StartZ=0 EndX=5 EndY=8.66025 EndZ=0
    g2: LineSegment StartX=5 StartY=8.66025 StartZ=0 EndX=-5 EndY=8.66025 EndZ=0
    g3: LineSegment StartX=-5 StartY=8.66025 StartZ=0 EndX=-10 EndY=-4.28e-14 EndZ=0
    g4: LineSegment StartX=-10 StartY=-4.26e-14 StartZ=0 EndX=-5 EndY=-8.66025 EndZ=0
    g5: LineSegment StartX=-5 StartY=-8.66025 StartZ=0 EndX=5 EndY=-8.66025 EndZ=0
    g6: Circle [constr] CenterX=0 CenterY=0 CenterZ=0 NormalX=0 NormalY=0 NormalZ=1 AngleXU=0 Radius=10
    g7: LineSegment StartX=1.75 StartY=-3.03109 StartZ=0 EndX=3.5 EndY=-8.26e-14 EndZ=0
    g8: LineSegment StartX=3.5 StartY=-8.26e-14 StartZ=0 EndX=1.75 EndY=3.03109 EndZ=0
    g9: LineSegment StartX=1.75 StartY=3.03109 StartZ=0 EndX=-1.75 EndY=3.03109 EndZ=0
    g10: LineSegment StartX=-1.75 StartY=3.03109 StartZ=0 EndX=-3.5 EndY=8.09e-14 EndZ=0
    g11: LineSegment StartX=-3.5 StartY=8.08e-14 StartZ=0 EndX=-1.75 EndY=-3.03109 EndZ=0
    g12: LineSegment StartX=-1.75 StartY=-3.03109 StartZ=0 EndX=1.75 EndY=-3.03109 EndZ=0
    g13: Circle [constr] CenterX=0 CenterY=0 CenterZ=0 NormalX=0 NormalY=0 NormalZ=1 AngleXU=0 Radius=3.5
  constraints (33):
    c: Coincident(g0,g1)
    c: Coincident(g1,g2)
    c: Coincident(g2,g3)
    c: Coincident(g3,g4)
    c: Coincident(g4,g5)
    c: Coincident(g5,g0)
    c: Equal(g0, g1-g5) x5
    c: PointOnObject(g0,g6)
    c: PointOnObject(g1,g6)
    c: PointOnObject(g2,g6)
    c: PointOnObject(g3,g6)
    c: PointOnObject(g4,g6)
    c: PointOnObject(g5,g6)
    c: DistanceX(g6) = 0
    c: DistanceY(g6) = 0
    c: Horizontal(g5)
    c: Coincident(g7,g8)
    c: Coincident(g8,g9)
    c: Coincident(g9,g10)
    c: Coincident(g10,g11)
    c: Coincident(g11,g12)
    c: Coincident(g12,g7)
    c: Equal(g7, g8-g12) x5
    c: PointOnObject(g7,g13)
    c: PointOnObject(g8,g13)
    c: PointOnObject(g9,g13)
    c: PointOnObject(g10,g13)
    c: PointOnObject(g11,g13)
    c: PointOnObject(g12,g13)
    c: Coincident(g13,g6)
    c: Horizontal(g12)
    c: Diameter(g13) = 7
    c: Diameter(g6) = 20
FEATURE [Part::Extrusion] Extrude153  label="tSlotIn001"
  Base = -> Sketch380
  Dir = (0,0,1)
  DirMode = 2
  FaceMakerClass = Part::FaceMakerBullseye
  FaceMakerMode = 3
  LengthFwd = 3
  LengthRev = 0
  Placement = pos=(0,-291.803,2.70756) rot=(1,0,0;3.83972rad)
  Solid = true
  Symmetric = false
FEATURE [Sketcher::SketchObject] Sketch388  label="m6Cut006"
  ArcFitTolerance = 0
  FullyConstrained = true
  MakeInternals = false
  Placement = pos=(0,0,14.5) rot=(0,0,1;0rad)
  sketch-geometry (1):
    g0: Circle CenterX=0 CenterY=-263.25 CenterZ=0 NormalX=0 NormalY=0 NormalZ=1 AngleXU=0 Radius=6.5
  constraints (3):
    c: DistanceX(g0) = 0
    c: Diameter(g0) = 13
    c: DistanceY(g0) = -263.25
FEATURE [Part::Extrusion] Extrude159
  Base = -> Sketch388
  Dir = (0,0,1)
  DirMode = 2
  FaceMakerClass = Part::FaceMakerBullseye
  FaceMakerMode = 3
  LengthFwd = 10
  LengthRev = 0
  Solid = true
  Symmetric = false
FEATURE [Sketcher::SketchObject] Sketch389  label="m6Cut007"
  ArcFitTolerance = 0
  FullyConstrained = true
  MakeInternals = false
  Placement = pos=(0,0,9) rot=(0,0,-1;0rad)
  sketch-geometry (1):
    g0: Circle CenterX=0 CenterY=-263.25 CenterZ=0 NormalX=0 NormalY=0 NormalZ=1 AngleXU=0 Radius=3.5
  constraints (3):
    c: DistanceX(g0) = 0
    c: Diameter(g0) = 7
    c: DistanceY(g0) = -263.25
FEATURE [Part::Extrusion] Extrude160
  Base = -> Sketch389
  Dir = (0,0,1)
  DirMode = 2
  FaceMakerClass = Part::FaceMakerBullseye
  FaceMakerMode = 3
  LengthFwd = 10
  LengthRev = 0
  Solid = true
  Symmetric = false
FEATURE [Sketcher::SketchObject] Sketch390
  ArcFitTolerance = 0
  FullyConstrained = true
  MakeInternals = false
  Placement = pos=(0,0,-20) rot=(0,0,1;0rad)
  sketch-geometry (6):
    g0: LineSegment StartX=-9.5 StartY=-279 StartZ=0 EndX=9.5 EndY=-279 EndZ=0
    g1: LineSegment StartX=9.5 StartY=-279 StartZ=0 EndX=9.5 EndY=-403 EndZ=0
    g2: LineSegment StartX=9.5 StartY=-403 StartZ=0 EndX=-9.5 EndY=-403 EndZ=0
    g3: LineSegment StartX=-9.5 StartY=-403 StartZ=0 EndX=-9.5 EndY=-279 EndZ=0
    g4: Circle CenterX=0 CenterY=-393.7 CenterZ=0 NormalX=0 NormalY=0 NormalZ=1 AngleXU=0 Radius=3.5
    g5: Circle CenterX=0 CenterY=-374.65 CenterZ=0 NormalX=0 NormalY=0 NormalZ=1 AngleXU=0 Radius=3.5
  constraints (18):
    c: Coincident(g0,g1)
    c: Coincident(g1,g2)
    c: Coincident(g2,g3)
    c: Horizontal(g0)
    c: Horizontal(g2)
    c: Vertical(g1)
    c: Vertical(g3)
    c: DistanceX(g2,g2) = 19
    c: DistanceX(g2) = -9.5
    c: DistanceY(g2) = -403
    c: PointOnObject(g4,g-2)
    c: PointOnObject(g5,g-2)
    c: Equal(g4,g5)
    c: Diameter(g4) = 7
    c: DistanceY(g4,g5) = 19.05
    c: DistanceY(g4) = -393.7
    c: DistanceY(g0) = -279
    c: Coincident(g0,g3)
FEATURE [Part::Extrusion] Extrude161  label="beam008"
  Base = -> Sketch390
  Dir = (0,0,1)
  DirMode = 2
  FaceMakerClass = Part::FaceMakerBullseye
  FaceMakerMode = 3
  LengthFwd = 10
  LengthRev = 0
  Solid = true
  Symmetric = false
FEATURE [Sketcher::SketchObject] Sketch391
  ArcFitTolerance = 0
  FullyConstrained = true
  MakeInternals = false
  Placement = pos=(0,-392.25,0) rot=(1,0,0;1.5708rad)
  sketch-geometry (5):
    g0: LineSegment StartX=-3.75 StartY=-10 StartZ=0 EndX=-3.75 EndY=-17.0849 EndZ=0
    g1: LineSegment StartX=-3.75 StartY=-17.0849 StartZ=0 EndX=0 EndY=-19.25 EndZ=0
    g2: LineSegment StartX=0 StartY=-19.25 StartZ=0 EndX=3.75 EndY=-17.0849 EndZ=0
    g3: LineSegment StartX=3.75 StartY=-17.0849 StartZ=0 EndX=3.75 EndY=-10 EndZ=0
    g4: LineSegment StartX=-3.75 StartY=-10 StartZ=0 EndX=3.75 EndY=-10 EndZ=0
  constraints (15):
    c: Vertical(g0)
    c: Coincident(g1,g0)
    c: PointOnObject(g1,g-2)
    c: Coincident(g2,g1)
    c: Coincident(g3,g2)
    c: Vertical(g3)
    c: Angle(g2,g1) = 2.0944
    c: DistanceY(g1) = -19.25
    c: DistanceY(g2,g0) = 0
    c: Angle(g3,g2) = 2.0944
    c: DistanceX(g2) = 3.75
    c: Coincident(g4,g0)
    c: Coincident(g4,g3)
    c: Horizontal(g4)
    c: DistanceY(g3) = -10
FEATURE [Part::Extrusion] Extrude162
  Base = -> Sketch391
  Dir = (0,-1,2e-16)
  DirMode = 2
  FaceMakerClass = Part::FaceMakerBullseye
  FaceMakerMode = 3
  LengthFwd = 3
  LengthRev = 0
  Solid = true
  Symmetric = false
FEATURE [Part::Cut] Cut143  label="beam006"
  Base = -> Extrude161
  Tool = -> Extrude162
FEATURE [Sketcher::SketchObject] Sketch392
  ArcFitTolerance = 0
  FullyConstrained = true
  MakeInternals = false
  Placement = pos=(0,-392.25,0) rot=(1,0,0;1.5708rad)
  sketch-geometry (7):
    g0: LineSegment StartX=3.68061 StartY=-17.125 StartZ=0 EndX=3.68061 EndY=-12.875 EndZ=0
    g1: LineSegment StartX=3.68061 StartY=-12.875 StartZ=0 EndX=-1.6279e-12 EndY=-10.75 EndZ=0
    g2: LineSegment StartX=-1.628e-12 StartY=-10.75 StartZ=0 EndX=-3.68061 EndY=-12.875 EndZ=0
    g3: LineSegment StartX=-3.68061 StartY=-12.875 StartZ=0 EndX=-3.68061 EndY=-17.125 EndZ=0
    g4: LineSegment StartX=-3.68061 StartY=-17.125 StartZ=0 EndX=-1.6275e-12 EndY=-19.25 EndZ=0
    g5: LineSegment StartX=-1.6276e-12 StartY=-19.25 StartZ=0 EndX=3.68061 EndY=-17.125 EndZ=0
    g6: Circle [constr] CenterX=0 CenterY=-15 CenterZ=0 NormalX=0 NormalY=0 NormalZ=1 AngleXU=0 Radius=4.25
  constraints (17):
    c: Coincident(g0,g1)
    c: Coincident(g1,g2)
    c: Coincident(g2,g3)
    c: Coincident(g3,g4)
    c: Coincident(g4,g5)
    c: Coincident(g5,g0)
    c: Equal(g0, g1-g5) x5
    c: PointOnObject(g0,g6)
    c: PointOnObject(g1,g6)
    c: PointOnObject(g2,g6)
    c: PointOnObject(g3,g6)
    c: PointOnObject(g4,g6)
    c: PointOnObject(g5,g6)
    c: PointOnObject(g6,g-2)
    c: DistanceY(g4) = -19.25
    c: Vertical(g0)
    c: DistanceY(g1) = -10.75
FEATURE [Part::Extrusion] Extrude163
  Base = -> Sketch392
  Dir = (0,-1,2e-16)
  DirMode = 2
  FaceMakerClass = Part::FaceMakerBullseye
  FaceMakerMode = 3
  LengthFwd = 3
  LengthRev = 0
  Placement = pos=(0,-2,0) rot=(0,0,1;0rad)
  Solid = true
  Symmetric = false
FEATURE [Part::Cut] Cut144  label="beam007"
  Base = -> Cut143
  Tool = -> Extrude163
FEATURE [Part::Fillet] Fillet247  label="tSlotIn002"
  Base = -> Cut144
  EdgeLinks = -> Cut144 [Edge5,Edge6,Edge7,Edge8,Edge9,Edge10,Edge11,Edge14]
  Edges = 8 edges: [Edge5 r=1,Edge6 r=2,Edge7 r=2,Edge8 r=1,Edge9 r=2,Edge10 r=2,Edge11 r=1,Edge14 r=1]
FEATURE [Sketcher::SketchObject] Sketch393
  ArcFitTolerance = 0
  FullyConstrained = true
  MakeInternals = false
  MapMode = 2
  sketch-geometry (4):
    g0: LineSegment StartX=24 StartY=-278.8 StartZ=0 EndX=24 EndY=-323.3 EndZ=0
    g1: LineSegment StartX=24 StartY=-323.3 StartZ=0 EndX=28 EndY=-323.3 EndZ=0
    g2: LineSegment StartX=28 StartY=-323.3 StartZ=0 EndX=28 EndY=-278.8 EndZ=0
    g3: LineSegment StartX=24 StartY=-278.8 StartZ=0 EndX=28 EndY=-278.8 EndZ=0
  constraints (12):
    c: Vertical(g0)
    c: Coincident(g1,g0)
    c: Coincident(g2,g1)
    c: Vertical(g2)
    c: Horizontal(g1)
    c: DistanceX(g0) = 24
    c: DistanceX(g1,g1) = 4
    c: DistanceY(g0) = -323.3
    c: Coincident(g3,g0)
    c: Coincident(g3,g2)
    c: Horizontal(g3)
    c: DistanceY(g0,g0) = 44.5
FEATURE [Part::Extrusion] Extrude164  label="rail004"
  Base = -> Sketch393
  Dir = (0,0,1)
  DirMode = 2
  FaceMakerClass = Part::FaceMakerBullseye
  FaceMakerMode = 3
  LengthFwd = 4
  LengthRev = 0
  Placement = pos=(0,0,-16) rot=(0,0,1;0rad)
  Solid = true
  Symmetric = false
FEATURE [Part::Fillet] Fillet248  label="tSlotIn003"
  Base = -> Extrude164
  EdgeLinks = -> Extrude164 [Edge10]
  Edges = 1 edges r=1: [Edge10]
FEATURE [Part::MultiFuse] Fusion168  label="tSlot"
  Shapes = -> [Fillet247,Fillet248,Extrude153,Extrude152,Cut140]
FEATURE [Sketcher::SketchObject] Sketch395
  ArcFitTolerance = 0
  FullyConstrained = true
  MakeInternals = false
  Placement = pos=(0,-395,0) rot=(1,0,0;1.5708rad)
  sketch-geometry (1):
    g0: Circle CenterX=0 CenterY=-15 CenterZ=0 NormalX=0 NormalY=0 NormalZ=1 AngleXU=0 Radius=2.2
  constraints (3):
    c: PointOnObject(g0,g-2)
    c: DistanceY(g0) = -15
    c: Diameter(g0) = 4.4
FEATURE [Part::Extrusion] Extrude166
  Base = -> Sketch395
  Dir = (0,-1,2e-16)
  DirMode = 2
  FaceMakerClass = Part::FaceMakerBullseye
  FaceMakerMode = 3
  LengthFwd = 8
  LengthRev = 0
  Solid = true
  Symmetric = false
FEATURE [Part::MultiFuse] Fusion167  label="tSlotCut002"
  Shapes = -> [Extrude166,Extrude159,Extrude160]
FEATURE [Part::MultiFuse] Fusion169  label="tSlotCut003"
  Shapes = -> [Fusion167,Extrude145,Cylinder198]
FEATURE [Part::Cut] Cut145  label="tSlotMount"
  Base = -> Fusion168
  Placement = pos=(0,292.5,144) rot=(0,0,1;0rad)
  Tool = -> Fusion169
FEATURE [Part::Fillet] Fillet250
  Base = -> Cut145
  EdgeLinks = -> Cut145 [Edge74,Edge77,Edge99,Edge110,Edge111]
  Edges = 5 edges r=1.7: [Edge74,Edge77,Edge99,Edge110,Edge111]
FEATURE [Part::Fillet] Fillet251
  Base = -> Fillet250
  EdgeLinks = -> Fillet250 [Edge155]
  Edges = 1 edges r=1: [Edge155]
FEATURE [Sketcher::SketchObject] Sketch396
  ArcFitTolerance = 0
  FullyConstrained = true
  MakeInternals = false
  Placement = pos=(0,0,14.25) rot=(0,0,1;0rad)
  sketch-geometry (18):
    g0: LineSegment StartX=-36 StartY=-62.3538 StartZ=0 EndX=-16 EndY=-62.3538 EndZ=0
    g1: LineSegment StartX=-36 StartY=-62.3538 StartZ=0 EndX=-46 EndY=-45.0333 EndZ=0
    g2: LineSegment StartX=-46 StartY=-45.0333 StartZ=0 EndX=-16 EndY=-62.3538 EndZ=0
    g3: LineSegment StartX=36 StartY=-62.3538 StartZ=0 EndX=16 EndY=-62.3538 EndZ=0
    g4: LineSegment StartX=16 StartY=-62.3538 StartZ=0 EndX=46 EndY=-45.0333 EndZ=0
    g5: LineSegment StartX=46 StartY=-45.0333 StartZ=0 EndX=36 EndY=-62.3538 EndZ=0
    g6: LineSegment StartX=72 StartY=0 StartZ=0 EndX=62 EndY=-17.3205 EndZ=0
    g7: LineSegment StartX=62 StartY=-17.3205 StartZ=0 EndX=62 EndY=17.3205 EndZ=0
    g8: LineSegment StartX=62 StartY=17.3205 StartZ=0 EndX=72 EndY=7e-15 EndZ=0
    g9: LineSegment StartX=36 StartY=62.3538 StartZ=0 EndX=16 EndY=62.3538 EndZ=0
    g10: LineSegment StartX=16 StartY=62.3538 StartZ=0 EndX=46 EndY=45.0333 EndZ=0
    g11: LineSegment StartX=46 StartY=45.0333 StartZ=0 EndX=36 EndY=62.3538 EndZ=0
    g12: LineSegment StartX=-16 StartY=62.3538 StartZ=0 EndX=-36 EndY=62.3538 EndZ=0
    g13: LineSegment StartX=-36 StartY=62.3538 StartZ=0 EndX=-46 EndY=45.0333 EndZ=0
    g14: LineSegment StartX=-46 StartY=45.0333 StartZ=0 EndX=-16 EndY=62.3538 EndZ=0
    g15: LineSegment StartX=-72 StartY=-9e-16 StartZ=0 EndX=-62 EndY=17.3205 EndZ=0
    g16: LineSegment StartX=-62 StartY=17.3205 StartZ=0 EndX=-62 EndY=-17.3205 EndZ=0
    g17: LineSegment StartX=-62 StartY=-17.3205 StartZ=0 EndX=-72 EndY=-9e-16 EndZ=0
  constraints (54):
    c: Coincident(g2,g1)
    c: Coincident(g2,g0)
    c: Coincident(g4,g3)
    c: Coincident(g5,g4)
    c: Coincident(g7,g6)
    c: Vertical(g7)
    c: Coincident(g8,g7)
    c: Coincident(g10,g9)
    c: Coincident(g11,g10)
    c: Coincident(g14,g13)
    c: Coincident(g14,g12)
    c: Coincident(g16,g15)
    c: Coincident(g17,g16)
    c: Distance(g-1,g3) = 72
    c: Distance(g-1,g12) = 72
    c: Vertical(g16)
    c: DistanceX(g0) = -36
    c: Vertical(g12,g0)
    c: DistanceX(g3) = 36
    c: Vertical(g9,g3)
    c: Horizontal(g6,g-1)
    c: Horizontal(g-1,g15)
    c: DistanceX(g15,g-1) = 72
    c: DistanceX(g-1,g6) = 72
    c: Horizontal(g12)
    c: Horizontal(g9)
    c: Horizontal(g3)
    c: Horizontal(g0)
    c: Distance(g-1,g0) = 72
    c: Distance(g-1,g9) = 72
    c: Distance(g0) = 20
    c: Distance(g1) = 20
    c: Coincident(g0,g1)
    c: Distance(g5) = 20
    c: Distance(g3) = 20
    c: Angle(g6) = -2.0944
    c: Distance(g6) = 20
    c: Distance(g8) = 20
    c: Distance(g11) = 20
    c: Distance(g9) = 20
    c: Distance(g12) = 20
    c: Distance(g13) = 20
    c: Distance(g15) = 20
    c: Distance(g17) = 20
    c: Angle(g17) = 2.0944
    c: Coincident(g15,g17)
    c: Coincident(g6,g8)
    c: Angle(g5) = -2.0944
    c: Coincident(g3,g5)
    c: Angle(g1) = 2.0944
    c: Coincident(g12,g13)
    c: Angle(g13) = -2.0944
    c: Coincident(g9,g11)
    c: Angle(g11) = 2.0944
FEATURE [Part::Extrusion] Extrude167  label="legs"
  Base = -> Sketch396
  Dir = (0,0,1)
  DirMode = 2
  FaceMakerClass = Part::FaceMakerBullseye
  FaceMakerMode = 3
  LengthFwd = 111
  LengthRev = 0
  Solid = true
  Symmetric = false
FEATURE [Part::MultiFuse] Fusion171  label="srs"
  Shapes = -> [Extrude167,Cut139,Fillet239,Fillet219,Fillet227,Fillet231,Fillet235,Fillet223]
FEATURE [Part::MultiFuse] Fusion172  label="srs021"
  Shapes = -> [Fusion171,Extrude148]
FEATURE [Sketcher::SketchObject] Sketch397  label="logoPanel009"
  ArcFitTolerance = 0
  FullyConstrained = true
  MakeInternals = false
  Placement = pos=(0,292.5,-126) rot=(0,0,1;0rad)
  sketch-geometry (4):
    g0: LineSegment StartX=31.3923 StartY=-370 StartZ=0 EndX=21 EndY=-352 EndZ=0
    g1: LineSegment StartX=21 StartY=-352 StartZ=0 EndX=-21 EndY=-352 EndZ=0
    g2: LineSegment StartX=-21 StartY=-352 StartZ=0 EndX=-31.3923 EndY=-370 EndZ=0
    g3: LineSegment StartX=31.3923 StartY=-370 StartZ=0 EndX=-31.3923 EndY=-370 EndZ=0
  constraints (12):
    c: Coincident(g1,g0)
    c: Horizontal(g1)
    c: Coincident(g2,g1)
    c: DistanceY(g1) = -352
    c: Coincident(g3,g0)
    c: Coincident(g3,g2)
    c: Horizontal(g3)
    c: Angle(g3,g2) = 1.0472
    c: Angle(g0,g3) = 1.0472
    c: DistanceX(g0) = 21
    c: DistanceX(g1) = -21
    c: DistanceY(g2) = -370
FEATURE [Part::Extrusion] Extrude168  label="srsCut006"
  Base = -> Sketch397
  Dir = (0,0,1)
  DirMode = 2
  FaceMakerClass = Part::FaceMakerBullseye
  FaceMakerMode = 3
  LengthFwd = 36
  LengthRev = 0
  Placement = pos=(0,0,144) rot=(0,0,1;0rad)
  Solid = true
  Symmetric = false
FEATURE [Sketcher::SketchObject] Sketch398
  ArcFitTolerance = 0
  FullyConstrained = true
  MakeInternals = false
  Placement = pos=(0,292.5,18) rot=(0,0,1;0rad)
  sketch-geometry (4):
    g0: LineSegment StartX=-14 StartY=-350 StartZ=0 EndX=14 EndY=-350 EndZ=0
    g1: LineSegment StartX=-14 StartY=-350 StartZ=0 EndX=-21 EndY=-352 EndZ=0
    g2: LineSegment StartX=-21 StartY=-352 StartZ=0 EndX=21 EndY=-352 EndZ=0
    g3: LineSegment StartX=21 StartY=-352 StartZ=0 EndX=14 EndY=-350 EndZ=0
  constraints (12):
    c: Horizontal(g0)
    c: DistanceY(g0) = -350
    c: DistanceX(g0) = 14
    c: DistanceX(g0) = -14
    c: Coincident(g1,g0)
    c: Coincident(g2,g1)
    c: Horizontal(g2)
    c: Coincident(g3,g2)
    c: Coincident(g0,g3)
    c: DistanceY(g1,g0) = 2
    c: DistanceX(g1) = -21
    c: DistanceX(g2) = 21
FEATURE [Part::Extrusion] Extrude169  label="logoConcaveCut003"
  Base = -> Sketch398
  Dir = (0,0,1)
  DirMode = 2
  FaceMakerClass = Part::FaceMakerBullseye
  FaceMakerMode = 3
  LengthFwd = 36
  LengthRev = 0
  Solid = true
  Symmetric = false
FEATURE [Sketcher::SketchObject] Sketch399
  ArcFitTolerance = 0
  FullyConstrained = true
  MakeInternals = false
  Placement = pos=(-21,292.5,142) rot=(0.57735,0.57735,0.57735;2.0944rad)
  sketch-geometry (4):
    g0: LineSegment StartX=-352 StartY=-88 StartZ=0 EndX=-350 EndY=-94 EndZ=0
    g1: LineSegment StartX=-350 StartY=-94 StartZ=0 EndX=-350 EndY=-118 EndZ=0
    g2: LineSegment StartX=-350 StartY=-118 StartZ=0 EndX=-352 EndY=-124 EndZ=0
    g3: LineSegment StartX=-352 StartY=-124 StartZ=0 EndX=-352 EndY=-88 EndZ=0
  constraints (12):
    c: Coincident(g0,g1)
    c: Vertical(g1)
    c: Coincident(g1,g2)
    c: Coincident(g2,g3)
    c: Coincident(g3,g0)
    c: Vertical(g3)
    c: DistanceX(g0) = -352
    c: DistanceX(g0,g0) = 2
    c: DistanceY(g0,g0) = 6
    c: DistanceY(g2,g1) = 6
    c: DistanceY(g2) = -124
    c: DistanceY(g2,g0) = 36
FEATURE [Part::Extrusion] Extrude170
  Base = -> Sketch399
  Dir = (1,0,0)
  DirMode = 2
  FaceMakerClass = Part::FaceMakerBullseye
  FaceMakerMode = 3
  LengthFwd = 42
  LengthRev = 0
  Solid = true
  Symmetric = false
FEATURE [Part::MultiCommon] Common005
  Shapes = -> [Extrude170,Extrude169]
FEATURE [Part::Fillet] Fillet249  label="srsCut007"
  Base = -> Common005
  EdgeLinks = -> Common005 [Edge1,Edge2,Edge3,Edge5,Edge7,Edge8,Edge9,Edge10]
  Edges = 8 edges r=3: [Edge1,Edge2,Edge3,Edge5,Edge7,Edge8,Edge9,Edge10]
FEATURE [Part::MultiFuse] Fusion173  label="srsCut010"
  Shapes = -> [Extrude168,Fillet249,Part__Feature328]
FEATURE [Part::Cut] Cut146  label="srs022"
  Base = -> Fusion172
  Tool = -> Fusion173
FEATURE [Part::MultiFuse] Fusion174
  Shapes = -> [Fillet251,Cut146]
FEATURE [Part::Fillet] Fillet252
  Base = -> Fusion174
  EdgeLinks = -> Fusion174 [Edge56,Edge64,Edge77,Edge80]
  Edges = 4 edges r=2: [Edge56,Edge64,Edge77,Edge80]
FEATURE [Part::Fillet] Fillet253
  Base = -> Fillet252
  EdgeLinks = -> Fillet252 [Edge14,Edge16,Edge46,Edge70]
  Edges = 4 edges r=1.75: [Edge14,Edge16,Edge46,Edge70]
FEATURE [Part::Fillet] Fillet254
  Base = -> Fillet253
  EdgeLinks = -> Fillet253 [Edge34,Edge35,Edge57,Edge71,Edge72,Edge73,Edge89]
  Edges = 7 edges: [Edge34 r=3,Edge35 r=1,Edge57 r=1,Edge71 r=3,Edge72 r=3,Edge73 r=3,Edge89 r=3]
FEATURE [Part::Fillet] Fillet255
  Base = -> Fillet254
  EdgeLinks = -> Fillet254 [Edge167,Edge169,Edge171,Edge173,Edge175,Edge180,Edge181,Edge182,Edge183,Edge184,Edge185]
  Edges = 11 edges r=1: [Edge167,Edge169,Edge171,Edge173,Edge175,Edge180,Edge181,Edge182,Edge183,Edge184,Edge185]
FEATURE [Part::Fillet] Fillet256
  Base = -> Fillet255
  EdgeLinks = -> Fillet255 [Edge37,Edge61]
  Edges = 2 edges r=1: [Edge37,Edge61]
FEATURE [Part::Fillet] Fillet257
  Base = -> Fillet256
  EdgeLinks = -> Fillet256 [Edge17,Edge18,Edge19,Edge20,Edge21]
  Edges = 5 edges r=1: [Edge17,Edge18,Edge19,Edge20,Edge21]
FEATURE [Part::Fillet] Fillet258
  Base = -> Fillet257
  EdgeLinks = -> Fillet257 [Edge106,Edge153,Edge161,Edge171,Edge206]
  Edges = 5 edges r=2: [Edge106,Edge153,Edge161,Edge171,Edge206]
FEATURE [Part::Fillet] Fillet259
  Base = -> Fillet258
  EdgeLinks = -> Fillet258 [Edge74,Edge90]
  Edges = 2 edges r=3: [Edge74,Edge90]
FEATURE [Part::Fillet] Fillet260  label="srs023"
  Base = -> Fillet259
  EdgeLinks = -> Fillet259 [Edge24,Edge25,Edge27,Edge96,Edge97,Edge98,Edge99,Edge100,Edge102,Edge104]
  Edges = 10 edges r=1: [Edge24,Edge25,Edge27,Edge96,Edge97,Edge98,Edge99,Edge100,Edge102,Edge104]
FEATURE [Part::Fillet] Fillet261
  Base = -> Fillet260
  EdgeLinks = -> Fillet260 [Edge82,Edge206,Edge222,Edge226,Edge229]
  Edges = 5 edges: [Edge82 r=2,Edge206 r=2,Edge222 r=2,Edge226 r=1,Edge229 r=2]
FEATURE [Sketcher::SketchObject] Sketch400
  ArcFitTolerance = 0
  FullyConstrained = true
  MakeInternals = false
  Placement = pos=(0,37,0) rot=(1,0,0;1.5708rad)
  sketch-geometry (12):
    g0: ArcOfCircle CenterX=-12 CenterY=153 CenterZ=0 NormalX=0 NormalY=0 NormalZ=1 AngleXU=0 Radius=1 StartAngle=1.5708 EndAngle=3.14159
    g1: ArcOfCircle CenterX=12 CenterY=153 CenterZ=0 NormalX=0 NormalY=0 NormalZ=1 AngleXU=0 Radius=1 StartAngle=-1.8e-15 EndAngle=1.5708
    g2: ArcOfCircle CenterX=-12 CenterY=129 CenterZ=0 NormalX=0 NormalY=0 NormalZ=1 AngleXU=0 Radius=1 StartAngle=3.14159 EndAngle=4.71239
    g3: ArcOfCircle CenterX=12 CenterY=129 CenterZ=0 NormalX=0 NormalY=0 NormalZ=1 AngleXU=0 Radius=1 StartAngle=4.71239 EndAngle=6.28319
    g4: LineSegment StartX=-13 StartY=153 StartZ=0 EndX=-13 EndY=154 EndZ=0
    g5: LineSegment StartX=-13 StartY=154 StartZ=0 EndX=-12 EndY=154 EndZ=0
    g6: LineSegment StartX=12 StartY=154 StartZ=0 EndX=13 EndY=154 EndZ=0
    g7: LineSegment StartX=13 StartY=154 StartZ=0 EndX=13 EndY=153 EndZ=0
    g8: LineSegment StartX=13 StartY=129 StartZ=0 EndX=13 EndY=128 EndZ=0
    g9: LineSegment StartX=13 StartY=128 StartZ=0 EndX=12 EndY=128 EndZ=0
    g10: LineSegment StartX=-13 StartY=129 StartZ=0 EndX=-13 EndY=128 EndZ=0
    g11: LineSegment StartX=-13 StartY=128 StartZ=0 EndX=-12 EndY=128 EndZ=0
  constraints (40):
    c: Angle(g0) = 1.5708
    c: DistanceY(g0,g0) = 0
    c: DistanceY(g1,g1) = 0
    c: Angle(g1) = 1.5708
    c: Angle(g2) = 1.5708
    c: Angle(g3) = 1.5708
    c: DistanceY(g2,g2) = 0
    c: DistanceY(g3,g3) = 0
    c: DistanceX(g2) = -12
    c: Diameter(g2) = 2
    c: Equal(g2,g3)
    c: Equal(g3,g1)
    c: Equal(g1,g0)
    c: DistanceY(g2,g3) = 0
    c: DistanceX(g3) = 12
    c: DistanceX(g2,g0) = 0
    c: DistanceY(g2,g0) = 24
    c: DistanceY(g0,g1) = 0
    c: DistanceX(g1,g3) = 0
    c: Coincident(g4,g0)
    c: Vertical(g4)
    c: Coincident(g5,g4)
    c: Coincident(g5,g0)
    c: Horizontal(g5)
    c: Coincident(g6,g1)
    c: Horizontal(g6)
    c: Coincident(g7,g6)
    c: Coincident(g7,g1)
    c: Vertical(g7)
    c: Coincident(g8,g3)
    c: Vertical(g8)
    c: Coincident(g9,g8)
    c: Coincident(g9,g3)
    c: Horizontal(g9)
    c: Coincident(g10,g2)
    c: Vertical(g10)
    c: Coincident(g11,g10)
    c: Coincident(g11,g2)
    c: Horizontal(g11)
    c: DistanceY(g10) = 128
FEATURE [Part::Extrusion] Extrude171
  Base = -> Sketch400
  Dir = (0,-1,2e-16)
  DirMode = 2
  FaceMakerClass = Part::FaceMakerBullseye
  FaceMakerMode = 3
  LengthFwd = 30
  LengthRev = 0
  Solid = true
  Symmetric = false
FEATURE [Part::MultiFuse] Fusion175  label="srs024"
  Placement = pos=(0,-296,-103) rot=(0,0,1;0rad)
  Shapes = -> [Fillet261,Extrude171]
FEATURE [Part::Feature] Part__Feature329  label="47065T221_T-Slotted Framing"
  Placement = pos=(6,207.5,-258.5) rot=(0,1,0;1.5708rad)
  shape: bbox 54.06 x 50.55 x 59.52 mm, 612 faces, 9 solids (baked)
FEATURE [Part::FeaturePython] Clone  label="tSlotTop"  # WARN: FeaturePython — macro-defined, semantics opaque (R4)
  AttacherType = Attacher::AttachEngine3D
  Fuse = false
  Placement = pos=(0,-49.4,554) rot=(1,0,0;1.5708rad)
  Scale = (1,1,3)
FEATURE [Part::FeaturePython] Clone001  label="tSlotBottom"  # WARN: FeaturePython — macro-defined, semantics opaque (R4)
  AttacherType = Attacher::AttachEngine3D
  Fuse = false
  Placement = pos=(0,-49.4,38) rot=(1,0,0;1.5708rad)
  Scale = (1,1,3)
FEATURE [Part::Feature] Part__Feature016  label="Z_-16147B_ZH-16147B-01"
  shape: bbox 438.9 x 219.4 x 405.1 mm, 3210 faces (baked)
FEATURE [Part::Feature] Part__Feature017  label="INSERTS-4"
  Placement = pos=(-180.975,-168.256,-155.575) rot=(0,0,1;0rad)
  shape: bbox 7.519 x 8.463 x 7.519 mm, 71 faces (baked)
FEATURE [Part::Feature] Part__Feature018  label="INSERTS-005"
  Placement = pos=(-170.872,-174.835,-145.472) rot=(0,0,1;3.14159rad)
  shape: bbox 7.519 x 8.463 x 7.519 mm, 71 faces (baked)
FEATURE [Part::Feature] Part__Feature019  label="INSERTS-006"
  Placement = pos=(-205.994,-3.7592,-180.594) rot=(0,0,1;3.14159rad)
  shape: bbox 7.519 x 8.463 x 7.519 mm, 71 faces (baked)
FEATURE [Part::Feature] Part__Feature020  label="INSERTS-007"
  Placement = pos=(-180.975,-168.083,155.575) rot=(1,0,0;3.14159rad)
  shape: bbox 7.519 x 8.463 x 7.519 mm, 71 faces (baked)
FEATURE [Part::Feature] Part__Feature021  label="INSERTS-008"
  Placement = pos=(-170.872,-175.008,145.472) rot=(0,1,0;3.14159rad)
  shape: bbox 7.519 x 8.463 x 7.519 mm, 71 faces (baked)
FEATURE [Part::Feature] Part__Feature022  label="INSERTS-009"
  Placement = pos=(-205.994,-3.93217,180.594) rot=(0,1,0;3.14159rad)
  shape: bbox 7.519 x 8.463 x 7.519 mm, 71 faces (baked)
FEATURE [Part::Feature] Part__Feature023  label="INSERTS-010"
  Placement = pos=(180.975,-168.083,-155.575) rot=(0,0,1;3.14159rad)
  shape: bbox 7.519 x 8.463 x 7.519 mm, 71 faces (baked)
FEATURE [Part::Feature] Part__Feature024  label="INSERTS-011"
  Placement = pos=(170.872,-175.008,-145.472) rot=(0,0,1;0rad)
  shape: bbox 7.519 x 8.463 x 7.519 mm, 71 faces (baked)
FEATURE [Part::Feature] Part__Feature025  label="INSERTS-012"
  Placement = pos=(205.994,-3.93217,-180.594) rot=(0,0,1;0rad)
  shape: bbox 7.519 x 8.463 x 7.519 mm, 71 faces (baked)
FEATURE [Part::Feature] Part__Feature026  label="INSERTS-013"
  Placement = pos=(180.975,-168.256,155.575) rot=(0,1,0;3.14159rad)
  shape: bbox 7.519 x 8.463 x 7.519 mm, 71 faces (baked)
FEATURE [Part::Feature] Part__Feature027  label="INSERTS-014"
  Placement = pos=(170.872,-174.835,145.472) rot=(1,0,0;3.14159rad)
  shape: bbox 7.519 x 8.463 x 7.519 mm, 71 faces (baked)
FEATURE [Part::Feature] Part__Feature028  label="INSERTS-015"
  Placement = pos=(205.994,-3.7592,180.594) rot=(1,0,0;3.14159rad)
  shape: bbox 7.519 x 8.463 x 7.519 mm, 71 faces (baked)
FEATURE [Part::Feature] Part__Feature029  label="LABEL-104"
  Placement = pos=(-1.221e-12,-20.3197,-180.67) rot=(1,0,0;1.56207rad)
  shape: bbox 63.5 x 38.1 x 0.3833 mm, 10 faces (baked)
FEATURE [App::Part] Z__16147BI_ZH_16147BI_01  label="Z_-16147BI_ZH-16147BI-01"
  Group = -> [Part__Feature016,Part__Feature017,Part__Feature018,Part__Feature019,Part__Feature020,Part__Feature021,Part__Feature022,Part__Feature023,Part__Feature024,Part__Feature025,Part__Feature026,Part__Feature027,Part__Feature028,Part__Feature029]
  Origin = -> Origin004
FEATURE [Part::Feature] Part__Feature030  label="Z_-16141C_ZH-16141C-01"
  shape: bbox 448.9 x 49.63 x 409 mm, 1738 faces (baked)
FEATURE [Part::Feature] Part__Feature031  label="ZH-1614G"
  Placement = pos=(0,0.635,6.9e-15) rot=(0,0,1;0rad)
  shape: bbox 434.5 x 6.35 x 383.7 mm, 136 faces (baked)
FEATURE [App::Part] Z__16141CG_ZH_16141CG_01  label="Z_-16141CG_ZH-16141CG-01"
  Group = -> [Part__Feature030,Part__Feature031]
  Origin = -> Origin005
FEATURE [Part::Feature] Part__Feature032  label="ZH-01F_ZH-01F-01"
  Placement = pos=(-158.172,-191.294,-145.472) rot=(0,0,1;0rad)
  shape: bbox 75.05 x 15.88 x 54.71 mm, 393 faces (baked)
FEATURE [Part::Feature] Part__Feature033  label="pan cross head_ai_SCREWS-046"
  Placement = pos=(-170.872,-191.294,-145.472) rot=(-0.002139,-0.002139,0.999995;1.5708rad)
  shape: bbox 10.25 x 22.43 x 10.25 mm, 92 faces (baked)
FEATURE [Part::Feature] Part__Feature034  label="pan cross head_ai_SCREWS-047"
  Placement = pos=(-170.872,-191.294,145.472) rot=(0.002139,0.002139,0.999995;1.5708rad)
  shape: bbox 10.25 x 22.43 x 10.25 mm, 92 faces (baked)
FEATURE [Part::Feature] Part__Feature035  label="ZH-01F_ZH-01F-002"
  Placement = pos=(-158.172,-191.294,145.472) rot=(0,0,1;0rad)
  shape: bbox 75.05 x 15.88 x 54.71 mm, 393 faces (baked)
FEATURE [Part::Feature] Part__Feature036  label="pan cross head_ai_SCREWS-048"
  Placement = pos=(170.872,-191.294,-145.472) rot=(0.707106,0.707106,-0.001512;3.14462rad)
  shape: bbox 10.25 x 22.43 x 10.25 mm, 92 faces (baked)
FEATURE [Part::Feature] Part__Feature037  label="pan cross head_ai_SCREWS-049"
  Placement = pos=(170.872,-191.294,145.472) rot=(0.707106,0.707106,0.001512;3.13857rad)
  shape: bbox 10.25 x 22.43 x 10.25 mm, 92 faces (baked)
FEATURE [Part::Feature] Part__Feature038  label="ZH-01F_ZH-01F-003"
  Placement = pos=(158.172,-191.294,-145.472) rot=(0,1,0;3.14159rad)
  shape: bbox 75.05 x 15.88 x 54.71 mm, 393 faces (baked)
FEATURE [Part::Feature] Part__Feature039  label="ZH-01F_ZH-01F-004"
  Placement = pos=(158.172,-191.294,145.472) rot=(0,1,0;3.14159rad)
  shape: bbox 75.05 x 15.88 x 54.71 mm, 393 faces (baked)
FEATURE [Part::Feature] Part__Feature040  label="SCREWS-047_default"
  Placement = pos=(-205.994,12.0142,-180.594) rot=(-1,0,0;1.5708rad)
  shape: bbox 9.234 x 22.51 x 9.177 mm, 32 faces (baked)
FEATURE [Part::Feature] Part__Feature041  label="SCREWS-047_default001"
  Placement = pos=(205.994,12.0142,-180.594) rot=(-1,0,0;1.5708rad)
  shape: bbox 9.234 x 22.51 x 9.177 mm, 32 faces (baked)
FEATURE [Part::Feature] Part__Feature042  label="SCREWS-047_default002"
  Placement = pos=(-205.994,12.0142,180.594) rot=(-1,0,0;1.5708rad)
  shape: bbox 9.234 x 22.51 x 9.177 mm, 32 faces (baked)
FEATURE [Part::Feature] Part__Feature043  label="SCREWS-047_default003"
  Placement = pos=(205.994,12.0142,180.594) rot=(-1,0,0;1.5708rad)
  shape: bbox 9.234 x 22.51 x 9.177 mm, 32 faces (baked)
FEATURE [App::Part] ZH_161407_33  label="ZH-161407-33"
  Group = -> [Z__16147BI_ZH_16147BI_01,Z__16141CG_ZH_16141CG_01,Part__Feature032,Part__Feature033,Part__Feature034,Part__Feature035,Part__Feature036,Part__Feature037,Part__Feature038,Part__Feature039,Part__Feature040,Part__Feature041,Part__Feature042,Part__Feature043]
  Origin = -> Origin006
  Placement = pos=(0,-180,296) rot=(0.707107,0,0.707107;3.14159rad)
FEATURE [Part::Box] Box  label="metalSheet"
  AttacherType = Attacher::AttachEngine3D
  Height = 593
  Length = 470
  Placement = pos=(-235,0,0) rot=(0,0,1;0rad)
  Width = 4
FEATURE [Part::Feature] Part__Feature  label="15275A57_Corner Bracket"
  Placement = pos=(-210,0,592.5) rot=(0,0.707107,0.707107;3.14159rad)
  shape: bbox 50.01 x 54.99 x 45.01 mm, 103 faces (baked)
FEATURE [Sketcher::SketchObject] Sketch
  ArcFitTolerance = 0
  FullyConstrained = true
  MakeInternals = false
  sketch-geometry (20):
    g0: LineSegment StartX=56.25 StartY=0 StartZ=0 EndX=93.75 EndY=0 EndZ=0
    g1: LineSegment StartX=56.25 StartY=0 StartZ=0 EndX=30 EndY=-80.2196 EndZ=0
    g2: LineSegment StartX=93.75 StartY=0 StartZ=0 EndX=120 EndY=-80.2196 EndZ=0
    g3: LineSegment StartX=30 StartY=-80.2196 StartZ=0 EndX=30 EndY=-117.72 EndZ=0
    g4: LineSegment StartX=30 StartY=-117.72 StartZ=0 EndX=56.25 EndY=-144.5 EndZ=0
    g5: LineSegment StartX=56.25 StartY=-144.5 StartZ=0 EndX=93.75 EndY=-144.5 EndZ=0
    g6: LineSegment StartX=93.75 StartY=-144.5 StartZ=0 EndX=120 EndY=-117.72 EndZ=0
    g7: LineSegment StartX=120 StartY=-117.72 StartZ=0 EndX=120 EndY=-80.2196 EndZ=0
    g8: ArcOfCircle CenterX=72.5 CenterY=-139.19 CenterZ=0 NormalX=0 NormalY=0 NormalZ=1 AngleXU=0 Radius=2.65 StartAngle=1.5708 EndAngle=4.71239
    g9: ArcOfCircle CenterX=77.5 CenterY=-139.19 CenterZ=0 NormalX=0 NormalY=0 NormalZ=1 AngleXU=0 Radius=2.65 StartAngle=4.71239 EndAngle=7.85398
    g10: LineSegment StartX=72.5 StartY=-141.84 StartZ=0 EndX=77.5 EndY=-141.84 EndZ=0
    g11: LineSegment StartX=77.5 StartY=-136.54 StartZ=0 EndX=72.5 EndY=-136.54 EndZ=0
    g12: Circle CenterX=62.5 CenterY=-5.75 CenterZ=0 NormalX=0 NormalY=0 NormalZ=1 AngleXU=0 Radius=2.5
    g13: Circle CenterX=75 CenterY=-5.75 CenterZ=0 NormalX=0 NormalY=0 NormalZ=1 AngleXU=0 Radius=2.5
    g14: Circle CenterX=87.5 CenterY=-5.75 CenterZ=0 NormalX=0 NormalY=0 NormalZ=1 AngleXU=0 Radius=2.5
    g15: Circle CenterX=75 CenterY=-20.75 CenterZ=0 NormalX=0 NormalY=0 NormalZ=1 AngleXU=0 Radius=2.5
    g16: Circle CenterX=75 CenterY=-45.75 CenterZ=0 NormalX=0 NormalY=0 NormalZ=1 AngleXU=0 Radius=2.5
    g17: Circle CenterX=62.5 CenterY=-33.25 CenterZ=0 NormalX=0 NormalY=0 NormalZ=1 AngleXU=0 Radius=2.5
    g18: Circle CenterX=87.5 CenterY=-33.25 CenterZ=0 NormalX=0 NormalY=0 NormalZ=1 AngleXU=0 Radius=2.5
    g19: Circle CenterX=75 CenterY=-98.9696 CenterZ=0 NormalX=0 NormalY=0 NormalZ=1 AngleXU=0 Radius=15
  constraints (58):
    c: PointOnObject(g0,g-1)
    c: PointOnObject(g0,g-1)
    c: Coincident(g1,g0)
    c: Coincident(g2,g0)
    c: Coincident(g3,g1)
    c: Vertical(g3)
    c: Coincident(g4,g3)
    c: Coincident(g5,g4)
    c: Horizontal(g5)
    c: Coincident(g6,g5)
    c: Coincident(g7,g2)
    c: DistanceX(g1) = 30
    c: Coincident(g6,g7)
    c: Horizontal(g6,g3)
    c: Horizontal(g2,g1)
    c: Vertical(g7)
    c: DistanceX(g0,g0) = 37.5
    c: DistanceX(g1,g2) = 90
    c: DistanceY(g4,g0) = 144.5
    c: DistanceX(g4,g5) = 37.5
    c: Vertical(g4,g0)
    c: Distance(g4) = 37.5
    c: Distance(g6) = 37.5
    c: Distance(g3,g1) = 37.5
    c: Tangent(g8,g10) = -1.5708
    c: Tangent(g10,g9) = -1.5708
    c: Tangent(g9,g11) = -1.5708
    c: Tangent(g11,g8) = -1.5708
    c: Equal(g8,g9)
    c: Horizontal(g9,g8)
    c: DistanceY(g9,g9) = 5.3
    c: DistanceX(g12,g14) = 25
    c: Equal(g14,g13)
    c: Equal(g14,g12)
    c: Diameter(g14) = 5
    c: Horizontal(g14,g13)
    c: Horizontal(g13,g12)
    c: DistanceX(g0,g13) = 18.75
    c: DistanceY(g12,g0) = 5.75
    c: DistanceX(g12,g13) = 12.5
    c: DistanceY(g15,g13) = 15
    c: DistanceY(g16,g15) = 25
    c: Vertical(g13,g15)
    c: Vertical(g15,g16)
    c: Horizontal(g18,g17)
    c: DistanceX(g17,g18) = 25
    c: Vertical(g17,g12)
    c: Equal(g16,g18)
    c: Equal(g16,g17)
    c: Equal(g16,g15)
    c: Diameter(g16) = 5
    c: DistanceY(g17,g15) = 12.5
    c: DistanceX(g8,g9) = 5
    c: DistanceX(g4,g8) = 16.25
    c: DistanceY(g4,g8) = 5.31
    c: DistanceX(g4,g19) = 18.75
    c: Diameter(g19) = 30
    c: DistanceY(g3,g19) = 18.75
FEATURE [Part::Extrusion] Extrude  label="mount"
  Base = -> Sketch
  Dir = (0,0,1)
  DirMode = 2
  FaceMakerClass = Part::FaceMakerBullseye
  FaceMakerMode = 3
  LengthFwd = 2.5
  LengthRev = 0
  Solid = true
  Symmetric = false
FEATURE [Sketcher::SketchObject] Sketch001
  ArcFitTolerance = 0
  FullyConstrained = true
  MakeInternals = false
  Placement = pos=(0,0,12.5) rot=(0,0,1;0rad)
  sketch-geometry (1):
    g0: Circle CenterX=75 CenterY=-99 CenterZ=0 NormalX=0 NormalY=0 NormalZ=1 AngleXU=0 Radius=70.5
  constraints (3):
    c: DistanceX(g0) = 75
    c: DistanceY(g0) = -99
    c: Diameter(g0) = 141
FEATURE [Part::Extrusion] Extrude001
  Base = -> Sketch001
  Dir = (0,0,1)
  DirMode = 2
  FaceMakerClass = Part::FaceMakerBullseye
  FaceMakerMode = 3
  LengthFwd = 8.5
  LengthRev = 0
  Solid = true
  Symmetric = false
FEATURE [Sketcher::SketchObject] Sketch002
  ArcFitTolerance = 0
  FullyConstrained = true
  MakeInternals = false
  Placement = pos=(0,0,57) rot=(0,0,1;0rad)
  sketch-geometry (1):
    g0: Circle CenterX=75 CenterY=-99 CenterZ=0 NormalX=0 NormalY=0 NormalZ=1 AngleXU=0 Radius=70.5
  constraints (3):
    c: DistanceX(g0) = 75
    c: DistanceY(g0) = -99
    c: Diameter(g0) = 141
FEATURE [Part::Extrusion] Extrude002
  Base = -> Sketch002
  Dir = (0,0,1)
  DirMode = 2
  FaceMakerClass = Part::FaceMakerBullseye
  FaceMakerMode = 3
  LengthFwd = 8
  LengthRev = 0
  Solid = true
  Symmetric = false
FEATURE [Sketcher::SketchObject] Sketch003
  ArcFitTolerance = 0
  FullyConstrained = true
  MakeInternals = false
  Placement = pos=(0,0,57) rot=(0,0,1;0rad)
  sketch-geometry (1):
    g0: Circle CenterX=75 CenterY=-99 CenterZ=0 NormalX=0 NormalY=0 NormalZ=1 AngleXU=0 Radius=67
  constraints (3):
    c: DistanceX(g0) = 75
    c: DistanceY(g0) = -99
    c: Diameter(g0) = 134
FEATURE [Part::Extrusion] Extrude003
  Base = -> Sketch003
  Dir = (0,0,1)
  DirMode = 2
  FaceMakerClass = Part::FaceMakerBullseye
  FaceMakerMode = 3
  LengthFwd = 45
  LengthRev = 0
  Solid = true
  Symmetric = false
FEATURE [Sketcher::SketchObject] Sketch004
  ArcFitTolerance = 0
  FullyConstrained = true
  MakeInternals = false
  Placement = pos=(0,0,111) rot=(0,0,1;0rad)
  sketch-geometry (1):
    g0: Circle CenterX=75 CenterY=-99 CenterZ=0 NormalX=0 NormalY=0 NormalZ=1 AngleXU=0 Radius=57.5
  constraints (3):
    c: DistanceX(g0) = 75
    c: DistanceY(g0) = -99
    c: Diameter(g0) = 115
FEATURE [Sketcher::SketchObject] Sketch005
  ArcFitTolerance = 0
  FullyConstrained = true
  MakeInternals = false
  Placement = pos=(0,0,102) rot=(0,0,1;0rad)
  sketch-geometry (1):
    g0: Circle CenterX=75 CenterY=-99 CenterZ=0 NormalX=0 NormalY=0 NormalZ=1 AngleXU=0 Radius=67
  constraints (3):
    c: DistanceX(g0) = 75
    c: DistanceY(g0) = -99
    c: Diameter(g0) = 134
FEATURE [Part::Loft] Loft080
  Closed = false
  MaxDegree = 5
  Ruled = false
  Sections = -> [Sketch005,Sketch004]
  Solid = true
FEATURE [Sketcher::SketchObject] Sketch007
  ArcFitTolerance = 0
  FullyConstrained = true
  MakeInternals = false
  Placement = pos=(0,0,12.5) rot=(0,0,1;0rad)
  sketch-geometry (4):
    g0: Circle CenterX=40 CenterY=-64 CenterZ=0 NormalX=0 NormalY=0 NormalZ=1 AngleXU=0 Radius=5
    g1: Circle CenterX=110 CenterY=-64 CenterZ=0 NormalX=0 NormalY=0 NormalZ=1 AngleXU=0 Radius=5
    g2: Circle CenterX=40 CenterY=-134 CenterZ=0 NormalX=0 NormalY=0 NormalZ=1 AngleXU=0 Radius=5
    g3: Circle CenterX=110 CenterY=-134 CenterZ=0 NormalX=0 NormalY=0 NormalZ=1 AngleXU=0 Radius=5
  constraints (12):
    c: Horizontal(g0,g1)
    c: Vertical(g0,g2)
    c: Horizontal(g3,g2)
    c: Vertical(g3,g1)
    c: DistanceX(g2,g3) = 70
    c: DistanceY(g2,g0) = 70
    c: Equal(g2,g3)
    c: Equal(g2,g1)
    c: Equal(g2,g0)
    c: Diameter(g2) = 10
    c: DistanceX(g2) = 40
    c: DistanceY(g2) = -134
FEATURE [Part::Extrusion] Extrude004
  Base = -> Sketch007
  Dir = (0,0,1)
  DirMode = 2
  FaceMakerClass = Part::FaceMakerBullseye
  FaceMakerMode = 3
  LengthFwd = 44.5
  LengthRev = 0
  Solid = true
  Symmetric = false
FEATURE [Sketcher::SketchObject] Sketch008
  ArcFitTolerance = 0
  FullyConstrained = true
  MakeInternals = false
  Placement = pos=(0,0,2.5) rot=(0,0,1;0rad)
  sketch-geometry (3):
    g0: Circle CenterX=40.19 CenterY=-78.9 CenterZ=0 NormalX=0 NormalY=0 NormalZ=1 AngleXU=0 Radius=4.5
    g1: Circle CenterX=109.81 CenterY=-78.9 CenterZ=0 NormalX=0 NormalY=0 NormalZ=1 AngleXU=0 Radius=4.5
    g2: Circle CenterX=75 CenterY=-139.2 CenterZ=0 NormalX=0 NormalY=0 NormalZ=1 AngleXU=0 Radius=4.5
  constraints (9):
    c: Horizontal(g0,g1)
    c: Equal(g2,g1)
    c: Equal(g2,g0)
    c: DistanceX(g2) = 75
    c: DistanceY(g2) = -139.2
    c: Diameter(g0) = 9
    c: DistanceX(g0,g2) = 34.81
    c: DistanceX(g2,g1) = 34.81
    c: DistanceY(g2,g0) = 60.3
FEATURE [Part::Extrusion] Extrude005
  Base = -> Sketch008
  Dir = (0,0,1)
  DirMode = 2
  FaceMakerClass = Part::FaceMakerBullseye
  FaceMakerMode = 3
  LengthFwd = 10
  LengthRev = 0
  Solid = true
  Symmetric = false
FEATURE [Part::MultiFuse] Fusion  label="renke"
  Shapes = -> [Extrude005,Extrude001,Extrude002,Extrude003,Loft080,Extrude004]
FEATURE [Part::Compound] Compound
  Links = -> [Extrude,Fusion]
  Placement = pos=(-285,-8.25,593) rot=(0,0,1;0rad)
FEATURE [Part::Box] Box020  label="Cube012"
  AttacherType = Attacher::AttachEngine3D
  Height = 20
  Length = 30
  Placement = pos=(-72,-155,80) rot=(0,0,1;0rad)
  Width = 10
FEATURE [Part::Box] Box021  label="Cube013"
  AttacherType = Attacher::AttachEngine3D
  Height = 25
  Length = 10
  Placement = pos=(-5,-109.35,75) rot=(0,0,1;0rad)
  Width = 20
FEATURE [Part::Box] Box063  label="Cube016"
  AttacherType = Attacher::AttachEngine3D
  Height = 15
  Length = 15
  Placement = pos=(95,-44,242) rot=(0,0,-1;1.5708rad)
  Width = 50
FEATURE [Part::Box] Box064  label="Cube017"
  AttacherType = Attacher::AttachEngine3D
  Height = 10
  Length = 71
  Placement = pos=(105,-44,244.5) rot=(0,0,-1;1.5708rad)
  Width = 30
FEATURE [Part::Box] Box065  label="Cube018"
  AttacherType = Attacher::AttachEngine3D
  Height = 30
  Length = 10
  Placement = pos=(115,-44,234.5) rot=(0,0,-1;1.5708rad)
  Width = 10
FEATURE [Part::Box] Box066  label="Cube019"
  AttacherType = Attacher::AttachEngine3D
  Height = 15
  Length = 15
  Placement = pos=(170,-44,242.5) rot=(0,0,-1;1.5708rad)
  Width = 80
FEATURE [Part::Box] Box067  label="Cube020"
  AttacherType = Attacher::AttachEngine3D
  Height = 15
  Length = 76
  Placement = pos=(170,-44,215) rot=(0,0,-1;1.5708rad)
  Width = 80
FEATURE [Part::Box] Box068  label="Cube021"
  AttacherType = Attacher::AttachEngine3D
  Height = 23.1
  Length = 91
  Placement = pos=(295,-44,234.4) rot=(0,0,-1;1.5708rad)
  Width = 10
FEATURE [Part::Box] Box069  label="Cube022"
  AttacherType = Attacher::AttachEngine3D
  Height = 15
  Length = 15
  Placement = pos=(270,-44,242.5) rot=(0,0,-1;1.5708rad)
  Width = 60
FEATURE [Part::Cylinder] Cylinder113
  Angle = 360
  AttacherType = Attacher::AttachEngine3D
  FirstAngle = 0
  Height = 76
  Placement = pos=(210,-44,250) rot=(1,0,0;1.5708rad)
  Radius = 27.5
  SecondAngle = 0
FEATURE [Part::Cylinder] Cylinder114
  Angle = 360
  AttacherType = Attacher::AttachEngine3D
  FirstAngle = 0
  Height = 76
  Placement = pos=(210,-44,250) rot=(1,0,0;1.5708rad)
  Radius = 21
  SecondAngle = 0
FEATURE [Part::Cut] Cut031
  Base = -> Cylinder113
  Tool = -> Cylinder114
FEATURE [Sketcher::SketchObject] Sketch144
  ArcFitTolerance = 0
  FullyConstrained = true
  MakeInternals = false
  sketch-geometry (16):
    g0: Circle CenterX=-67 CenterY=-167.5 CenterZ=0 NormalX=0 NormalY=0 NormalZ=1 AngleXU=0 Radius=1.625
    g1: Circle CenterX=-47 CenterY=-167.5 CenterZ=0 NormalX=0 NormalY=0 NormalZ=1 AngleXU=0 Radius=1.625
    g2: Circle CenterX=-67 CenterY=-132.5 CenterZ=0 NormalX=0 NormalY=0 NormalZ=1 AngleXU=0 Radius=1.625
    g3: Circle CenterX=-47 CenterY=-132.5 CenterZ=0 NormalX=0 NormalY=0 NormalZ=1 AngleXU=0 Radius=1.625
    g4: LineSegment StartX=-62 StartY=-129.75 StartZ=0 EndX=-72 EndY=-129.75 EndZ=0
    g5: LineSegment StartX=-52 StartY=-129.75 StartZ=0 EndX=-42 EndY=-129.75 EndZ=0
    g6: LineSegment StartX=-72 StartY=-129.75 StartZ=0 EndX=-72 EndY=-170.25 EndZ=0
    g7: LineSegment StartX=-72 StartY=-170.25 StartZ=0 EndX=-62 EndY=-170.25 EndZ=0
    g8: LineSegment StartX=-62 StartY=-170.25 StartZ=0 EndX=-62 EndY=-155 EndZ=0
    g9: LineSegment StartX=-52 StartY=-155 StartZ=0 EndX=-52 EndY=-170.25 EndZ=0
    g10: LineSegment StartX=-52 StartY=-170.25 StartZ=0 EndX=-42 EndY=-170.25 EndZ=0
    g11: LineSegment StartX=-42 StartY=-170.25 StartZ=0 EndX=-42 EndY=-129.75 EndZ=0
    g12: LineSegment StartX=-62 StartY=-155 StartZ=0 EndX=-52 EndY=-155 EndZ=0
    g13: LineSegment StartX=-62 StartY=-129.75 StartZ=0 EndX=-62 EndY=-145 EndZ=0
    g14: LineSegment StartX=-62 StartY=-145 StartZ=0 EndX=-52 EndY=-145 EndZ=0
    g15: LineSegment StartX=-52 StartY=-145 StartZ=0 EndX=-52 EndY=-129.75 EndZ=0
  constraints (48):
    c: DistanceY(g2,g3) = 0
    c: DistanceX(g0,g2) = 0
    c: DistanceX(g1,g3) = 0
    c: DistanceX(g1) = -47
    c: DistanceY(g1) = -167.5
    c: DistanceX(g0,g1) = 20
    c: Horizontal(g4)
    c: Horizontal(g5)
    c: Vertical(g6)
    c: Coincident(g7,g6)
    c: Horizontal(g7)
    c: Coincident(g8,g7)
    c: Vertical(g9)
    c: Coincident(g10,g9)
    c: Horizontal(g10)
    c: Coincident(g11,g10)
    c: Vertical(g8)
    c: DistanceX(g4,g4) = 10
    c: DistanceX(g5,g5) = 10
    c: DistanceX(g6,g7) = 10
    c: DistanceX(g9,g10) = 10
    c: Vertical(g11)
    c: DistanceY(g7,g9) = 0
    c: DistanceY(g4,g5) = 0
    c: DistanceX(g6,g0) = 5
    c: DistanceX(g9,g1) = 5
    c: DistanceY(g2,g4) = 2.75
    c: Coincident(g4,g6)
    c: Coincident(g12,g8)
    c: Horizontal(g12)
    c: Coincident(g9,g12)
    c: Coincident(g13,g4)
    c: Vertical(g13)
    c: Coincident(g14,g13)
    c: Horizontal(g14)
    c: Coincident(g15,g14)
    c: Coincident(g15,g5)
    c: Vertical(g15)
    c: Coincident(g5,g11)
    c: DistanceY(g8,g13) = 10
    c: DistanceY(g13) = -145
    c: DistanceY(g7,g0) = 2.75
    c: Equal(g1,g0)
    c: Equal(g1,g2)
    c: Equal(g1,g3)
    c: Diameter(g1) = 3.25
    c: DistanceY(g1,g0) = 0
    c: DistanceY(g2) = -132.5
FEATURE [Part::Extrusion] Extrude045  label="as7265Holder002"
  Base = -> Sketch144
  Dir = (0,0,1)
  DirMode = 2
  FaceMakerClass = Part::FaceMakerBullseye
  FaceMakerMode = 3
  LengthFwd = 10
  LengthRev = 0
  Placement = pos=(0,0,100) rot=(0,0,1;0rad)
  Solid = true
  Symmetric = false
FEATURE [Part::MultiFuse] Fusion122  label="as7265Holder003"
  Placement = pos=(177,-35,399.5) rot=(1,0,0;1.5708rad)
  Shapes = -> [Box020,Extrude045]
FEATURE [Part::MultiFuse] Fusion144  label="AS72xHolder"
  Placement = pos=(0,0,0.5) rot=(0,0,1;0rad)
  Shapes = -> [Box063,Box064,Box065,Fusion122]
FEATURE [Sketcher::SketchObject] Sketch146
  ArcFitTolerance = 0
  FullyConstrained = true
  MakeInternals = false
  sketch-geometry (11):
    g0: Circle CenterX=6.5 CenterY=-83 CenterZ=0 NormalX=0 NormalY=0 NormalZ=1 AngleXU=0 Radius=1.125
    g1: Circle CenterX=10.15 CenterY=-91.65 CenterZ=0 NormalX=0 NormalY=0 NormalZ=1 AngleXU=0 Radius=1.125
    g2: Circle CenterX=10.15 CenterY=-104.35 CenterZ=0 NormalX=0 NormalY=0 NormalZ=1 AngleXU=0 Radius=1.125
    g3: Circle CenterX=-10.15 CenterY=-104.35 CenterZ=0 NormalX=0 NormalY=0 NormalZ=1 AngleXU=0 Radius=1.125
    g4: Circle CenterX=-10.15 CenterY=-91.65 CenterZ=0 NormalX=0 NormalY=0 NormalZ=1 AngleXU=0 Radius=1.125
    g5: ArcOfCircle CenterX=-9.5 CenterY=-78 CenterZ=0 NormalX=0 NormalY=0 NormalZ=1 AngleXU=0 Radius=9.5 StartAngle=4.71239 EndAngle=6.28319
    g6: LineSegment StartX=-9.5 StartY=-87.5 StartZ=0 EndX=-15.15 EndY=-87.5 EndZ=0
    g7: LineSegment StartX=-15.15 StartY=-87.5 StartZ=0 EndX=-15.15 EndY=-109.35 EndZ=0
    g8: LineSegment StartX=-15.15 StartY=-109.35 StartZ=0 EndX=15.15 EndY=-109.35 EndZ=0
    g9: LineSegment StartX=15.15 StartY=-109.35 StartZ=0 EndX=15.15 EndY=-78 EndZ=0
    g10: LineSegment StartX=15.15 StartY=-78 StartZ=0 EndX=0 EndY=-78 EndZ=0
  constraints (34):
    c: DistanceX(g4,g3) = 0
    c: DistanceX(g2,g1) = 0
    c: Equal(g2,g3)
    c: Equal(g2,g4)
    c: Equal(g2,g1)
    c: Equal(g2,g0)
    c: Diameter(g2) = 2.25
    c: DistanceX(g2) = 10.15
    c: DistanceY(g2) = -104.35
    c: DistanceY(g2,g1) = 12.7
    c: DistanceY(g3,g2) = 0
    c: DistanceX(g3,g2) = 20.3
    c: DistanceY(g4,g1) = 0
    c: DistanceY(g0) = -83
    c: DistanceX(g0) = 6.5
    c: PointOnObject(g5,g-2)
    c: Coincident(g6,g5)
    c: Horizontal(g6)
    c: Coincident(g7,g6)
    c: Vertical(g7)
    c: Coincident(g8,g7)
    c: Horizontal(g8)
    c: Coincident(g9,g8)
    c: Vertical(g9)
    c: Coincident(g10,g9)
    c: Coincident(g10,g5)
    c: Horizontal(g10)
    c: DistanceY(g5) = -78
    c: DistanceY(g5,g5) = 0
    c: DistanceX(g5,g5) = 9.5
    c: DistanceX(g5,g5) = 0
    c: DistanceX(g1,g9) = 5
    c: DistanceX(g7,g3) = 5
    c: DistanceY(g7,g3) = 5
FEATURE [Part::Extrusion] Extrude047  label="uvHolder002"
  Base = -> Sketch146
  Dir = (0,0,1)
  DirMode = 2
  FaceMakerClass = Part::FaceMakerBullseye
  FaceMakerMode = 3
  LengthFwd = 10
  LengthRev = 0
  Placement = pos=(0,0,100) rot=(0,0,1;0rad)
  Solid = true
  Symmetric = false
FEATURE [Part::MultiFuse] Fusion123  label="uvHolder003"
  Placement = pos=(300,-35,343.75) rot=(1,0,0;1.5708rad)
  Shapes = -> [Box021,Extrude047]
FEATURE [Part::MultiFuse] Fusion148  label="uvHolder"
  Shapes = -> [Box069,Box068,Fusion123]
FEATURE [Sketcher::SketchObject] Sketch174
  ArcFitTolerance = 0
  FullyConstrained = true
  MakeInternals = false
  Placement = pos=(0,-100,0) rot=(1,0,0;1.5708rad)
  sketch-geometry (16):
    g0: ArcOfCircle CenterX=193 CenterY=233 CenterZ=0 NormalX=0 NormalY=0 NormalZ=1 AngleXU=0 Radius=3 StartAngle=5.49779 EndAngle=8.63938
    g1: ArcOfCircle CenterX=227 CenterY=233 CenterZ=0 NormalX=0 NormalY=0 NormalZ=1 AngleXU=0 Radius=3 StartAngle=0.785398 EndAngle=3.92699
    g2: ArcOfCircle CenterX=227 CenterY=267 CenterZ=0 NormalX=0 NormalY=0 NormalZ=1 AngleXU=0 Radius=3 StartAngle=2.35619 EndAngle=5.49779
    g3: ArcOfCircle CenterX=193 CenterY=267 CenterZ=0 NormalX=0 NormalY=0 NormalZ=1 AngleXU=0 Radius=3 StartAngle=3.92699 EndAngle=7.06858
    g4: LineSegment StartX=190.879 StartY=235.121 StartZ=0 EndX=186.636 EndY=230.879 EndZ=0
    g5: LineSegment StartX=186.636 StartY=230.879 StartZ=0 EndX=190.879 EndY=226.636 EndZ=0
    g6: LineSegment StartX=190.879 StartY=226.636 StartZ=0 EndX=195.121 EndY=230.879 EndZ=0
    g7: LineSegment StartX=190.879 StartY=264.879 StartZ=0 EndX=186.636 EndY=269.121 EndZ=0
    g8: LineSegment StartX=190.879 StartY=273.364 StartZ=0 EndX=195.121 EndY=269.121 EndZ=0
    g9: LineSegment StartX=190.879 StartY=273.364 StartZ=0 EndX=186.636 EndY=269.121 EndZ=0
    g10: LineSegment StartX=224.879 StartY=230.879 StartZ=0 EndX=229.121 EndY=226.636 EndZ=0
    g11: LineSegment StartX=229.121 StartY=226.636 StartZ=0 EndX=233.364 EndY=230.879 EndZ=0
    g12: LineSegment StartX=233.364 StartY=230.879 StartZ=0 EndX=229.121 EndY=235.121 EndZ=0
    g13: LineSegment StartX=224.879 StartY=269.121 StartZ=0 EndX=229.121 EndY=273.364 EndZ=0
    g14: LineSegment StartX=229.121 StartY=273.364 StartZ=0 EndX=233.364 EndY=269.121 EndZ=0
    g15: LineSegment StartX=233.364 StartY=269.121 StartZ=0 EndX=229.121 EndY=264.879 EndZ=0
  constraints (52):
    c: Horizontal(g3,g2)
    c: Vertical(g3,g0)
    c: Horizontal(g0,g1)
    c: Vertical(g1,g2)
    c: DistanceX(g0) = 193
    c: DistanceY(g0) = 233
    c: DistanceY(g0,g3) = 34
    c: DistanceX(g3,g2) = 34
    c: Equal(g3,g2)
    c: Equal(g3,g1)
    c: Equal(g3,g0)
    c: Angle(g0) = 3.14159
    c: Angle(g1) = 3.14159
    c: Angle(g2) = 3.14159
    c: Angle(g3) = 3.14159
    c: Vertical(g3,g0)
    c: Horizontal(g0,g1)
    c: Vertical(g1,g2)
    c: Coincident(g5,g4)
    c: Coincident(g5,g6)
    c: Coincident(g0,g6)
    c: Angle(g6,g5) = 1.5708
    c: Angle(g5,g4) = 1.5708
    c: Distance(g5) = 6
    c: Distance(g6) = 6
    c: Coincident(g0,g4)
    c: Distance(g0,g0) = 6
    c: Angle(g6) = 0.785398
    c: Coincident(g7,g3)
    c: Coincident(g8,g3)
    c: Coincident(g9,g8)
    c: Coincident(g9,g7)
    c: Perpendicular(g7,g9)
    c: Perpendicular(g8,g9)
    c: Angle(g7) = 2.35619
    c: Distance(g7) = 6
    c: Coincident(g10,g1)
    c: Coincident(g11,g10)
    c: Coincident(g12,g11)
    c: Coincident(g12,g1)
    c: Perpendicular(g11,g12)
    c: Perpendicular(g11,g10)
    c: Distance(g10) = 6
    c: Distance(g11) = 6
    c: Coincident(g13,g2)
    c: Coincident(g14,g13)
    c: Coincident(g15,g14)
    c: Coincident(g15,g2)
    c: Perpendicular(g14,g15)
    c: Perpendicular(g13,g14)
    c: Distance(g15) = 6
    c: Distance(g14) = 6
FEATURE [Part::Extrusion] Extrude073
  Base = -> Sketch174
  Dir = (0,-1,2e-16)
  DirMode = 2
  FaceMakerClass = Part::FaceMakerBullseye
  FaceMakerMode = 3
  LengthFwd = 20
  LengthRev = 0
  Solid = true
  Symmetric = false
FEATURE [Part::MultiFuse] Fusion177  label="cameraHolderCuts"
  Shapes = -> [Extrude073,Box067]
FEATURE [Sketcher::SketchObject] Sketch185
  ArcFitTolerance = 0
  FullyConstrained = true
  MakeInternals = false
  Placement = pos=(0,-36,0) rot=(1,0,0;1.5708rad)
  sketch-geometry (19):
    g0: Circle CenterX=151 CenterY=387 CenterZ=0 NormalX=0 NormalY=0 NormalZ=1 AngleXU=0 Radius=1.625
    g1: Circle CenterX=151 CenterY=312.5 CenterZ=0 NormalX=0 NormalY=0 NormalZ=1 AngleXU=0 Radius=1.625
    g2: Circle CenterX=240 CenterY=312.5 CenterZ=0 NormalX=0 NormalY=0 NormalZ=1 AngleXU=0 Radius=1.625
    g3: Circle CenterX=260 CenterY=312.5 CenterZ=0 NormalX=0 NormalY=0 NormalZ=1 AngleXU=0 Radius=1.625
    g4: Circle CenterX=303 CenterY=312.5 CenterZ=0 NormalX=0 NormalY=0 NormalZ=1 AngleXU=0 Radius=1.625
    g5: Circle CenterX=312.5 CenterY=312.5 CenterZ=0 NormalX=0 NormalY=0 NormalZ=1 AngleXU=0 Radius=1.625
    g6: Circle CenterX=293 CenterY=405 CenterZ=0 NormalX=0 NormalY=0 NormalZ=1 AngleXU=0 Radius=1.625
    g7: Circle CenterX=323 CenterY=405 CenterZ=0 NormalX=0 NormalY=0 NormalZ=1 AngleXU=0 Radius=1.625
    g8: Circle CenterX=270.5 CenterY=405 CenterZ=0 NormalX=0 NormalY=0 NormalZ=1 AngleXU=0 Radius=1.625
    g9: Circle CenterX=280.5 CenterY=405 CenterZ=0 NormalX=0 NormalY=0 NormalZ=1 AngleXU=0 Radius=1.625
    g10: Circle CenterX=250.5 CenterY=405 CenterZ=0 NormalX=0 NormalY=0 NormalZ=1 AngleXU=0 Radius=1.625
    g11: Circle CenterX=213 CenterY=405 CenterZ=0 NormalX=0 NormalY=0 NormalZ=1 AngleXU=0 Radius=1.625
    g12: Circle CenterX=227 CenterY=405 CenterZ=0 NormalX=0 NormalY=0 NormalZ=1 AngleXU=0 Radius=1.625
    g13: Circle CenterX=100 CenterY=250 CenterZ=0 NormalX=0 NormalY=0 NormalZ=1 AngleXU=0 Radius=1.625
    g14: Circle CenterX=140 CenterY=250 CenterZ=0 NormalX=0 NormalY=0 NormalZ=1 AngleXU=0 Radius=1.625
    g15: Circle CenterX=177 CenterY=250 CenterZ=0 NormalX=0 NormalY=0 NormalZ=1 AngleXU=0 Radius=1.625
    g16: Circle CenterX=243 CenterY=250 CenterZ=0 NormalX=0 NormalY=0 NormalZ=1 AngleXU=0 Radius=1.625
    g17: Circle CenterX=275 CenterY=250 CenterZ=0 NormalX=0 NormalY=0 NormalZ=1 AngleXU=0 Radius=1.625
    g18: Circle CenterX=325 CenterY=250 CenterZ=0 NormalX=0 NormalY=0 NormalZ=1 AngleXU=0 Radius=1.625
  constraints (53):
    c: Vertical(g1,g0)
    c: DistanceY(g1) = 312.5
    c: DistanceY(g1,g0) = 74.5
    c: Equal(g1,g0)
    c: Horizontal(g2,g3)
    c: Horizontal(g3,g4)
    c: Horizontal(g4,g5)
    c: DistanceX(g2) = 240
    c: Horizontal(g2,g1)
    c: DistanceX(g3) = 260
    c: DistanceX(g4) = 303
    c: DistanceX(g4,g5) = 9.5
    c: DistanceX(g11) = 213
    c: Horizontal(g12,g11)
    c: Horizontal(g11,g10)
    c: Horizontal(g10,g8)
    c: Horizontal(g8,g9)
    c: Horizontal(g9,g6)
    c: Horizontal(g6,g7)
    c: DistanceY(g11) = 405
    c: DistanceX(g11,g12) = 14
    c: DistanceX(g12,g10) = 23.5
    c: DistanceX(g8) = 270.5
    c: DistanceX(g8,g9) = 10
    c: DistanceX(g6) = 293
    c: DistanceX(g6,g7) = 30
    c: Horizontal(g16,g17)
    c: Horizontal(g17,g18)
    c: Horizontal(g18,g15)
    c: Horizontal(g15,g14)
    c: Horizontal(g14,g13)
    c: DistanceX(g13) = 100
    c: DistanceY(g13) = 250
    c: DistanceX(g13,g14) = 40
    c: DistanceX(g15) = 177
    c: DistanceX(g15,g16) = 66
    c: DistanceX(g17) = 275
    c: DistanceX(g17,g18) = 50
    c: Equal(g13, g14-g18) x5
    c: Equal(g13,g5)
    c: Equal(g13,g4)
    c: Equal(g13,g3)
    c: Equal(g13,g2)
    c: Equal(g13,g1)
    c: Equal(g13,g11)
    c: Equal(g13,g12)
    c: Equal(g13,g10)
    c: Equal(g13,g8)
    c: Equal(g13,g9)
    c: Equal(g13,g6)
    c: Equal(g13,g7)
    c: Diameter(g13) = 3.25
    c: DistanceX(g1) = 151
FEATURE [Part::Extrusion] Extrude083  label="level2Cuts009"
  Base = -> Sketch185
  Dir = (0,-1,2e-16)
  DirMode = 2
  FaceMakerClass = Part::FaceMakerBullseye
  FaceMakerMode = 3
  LengthFwd = 25
  LengthRev = 0
  Solid = true
  Symmetric = false
FEATURE [Part::Cut] Cut043  label="AS7265xHolder"
  Base = -> Fusion144
  Tool = -> Extrude083
FEATURE [Sketcher::SketchObject] Sketch186
  ArcFitTolerance = 0
  FullyConstrained = true
  MakeInternals = false
  Placement = pos=(0,-36,0) rot=(1,0,0;1.5708rad)
  sketch-geometry (19):
    g0: Circle CenterX=151 CenterY=387 CenterZ=0 NormalX=0 NormalY=0 NormalZ=1 AngleXU=0 Radius=1.625
    g1: Circle CenterX=151 CenterY=312.5 CenterZ=0 NormalX=0 NormalY=0 NormalZ=1 AngleXU=0 Radius=1.625
    g2: Circle CenterX=240 CenterY=312.5 CenterZ=0 NormalX=0 NormalY=0 NormalZ=1 AngleXU=0 Radius=1.625
    g3: Circle CenterX=260 CenterY=312.5 CenterZ=0 NormalX=0 NormalY=0 NormalZ=1 AngleXU=0 Radius=1.625
    g4: Circle CenterX=303 CenterY=312.5 CenterZ=0 NormalX=0 NormalY=0 NormalZ=1 AngleXU=0 Radius=1.625
    g5: Circle CenterX=312.5 CenterY=312.5 CenterZ=0 NormalX=0 NormalY=0 NormalZ=1 AngleXU=0 Radius=1.625
    g6: Circle CenterX=293 CenterY=405 CenterZ=0 NormalX=0 NormalY=0 NormalZ=1 AngleXU=0 Radius=1.625
    g7: Circle CenterX=323 CenterY=405 CenterZ=0 NormalX=0 NormalY=0 NormalZ=1 AngleXU=0 Radius=1.625
    g8: Circle CenterX=270.5 CenterY=405 CenterZ=0 NormalX=0 NormalY=0 NormalZ=1 AngleXU=0 Radius=1.625
    g9: Circle CenterX=280.5 CenterY=405 CenterZ=0 NormalX=0 NormalY=0 NormalZ=1 AngleXU=0 Radius=1.625
    g10: Circle CenterX=250.5 CenterY=405 CenterZ=0 NormalX=0 NormalY=0 NormalZ=1 AngleXU=0 Radius=1.625
    g11: Circle CenterX=213 CenterY=405 CenterZ=0 NormalX=0 NormalY=0 NormalZ=1 AngleXU=0 Radius=1.625
    g12: Circle CenterX=227 CenterY=405 CenterZ=0 NormalX=0 NormalY=0 NormalZ=1 AngleXU=0 Radius=1.625
    g13: Circle CenterX=100 CenterY=250 CenterZ=0 NormalX=0 NormalY=0 NormalZ=1 AngleXU=0 Radius=1.625
    g14: Circle CenterX=140 CenterY=250 CenterZ=0 NormalX=0 NormalY=0 NormalZ=1 AngleXU=0 Radius=1.625
    g15: Circle CenterX=177 CenterY=250 CenterZ=0 NormalX=0 NormalY=0 NormalZ=1 AngleXU=0 Radius=1.625
    g16: Circle CenterX=243 CenterY=250 CenterZ=0 NormalX=0 NormalY=0 NormalZ=1 AngleXU=0 Radius=1.625
    g17: Circle CenterX=275 CenterY=250 CenterZ=0 NormalX=0 NormalY=0 NormalZ=1 AngleXU=0 Radius=1.625
    g18: Circle CenterX=325 CenterY=250 CenterZ=0 NormalX=0 NormalY=0 NormalZ=1 AngleXU=0 Radius=1.625
  constraints (53):
    c: Vertical(g1,g0)
    c: DistanceY(g1) = 312.5
    c: DistanceY(g1,g0) = 74.5
    c: Equal(g1,g0)
    c: Horizontal(g2,g3)
    c: Horizontal(g3,g4)
    c: Horizontal(g4,g5)
    c: DistanceX(g2) = 240
    c: Horizontal(g2,g1)
    c: DistanceX(g3) = 260
    c: DistanceX(g4) = 303
    c: DistanceX(g4,g5) = 9.5
    c: DistanceX(g11) = 213
    c: Horizontal(g12,g11)
    c: Horizontal(g11,g10)
    c: Horizontal(g10,g8)
    c: Horizontal(g8,g9)
    c: Horizontal(g9,g6)
    c: Horizontal(g6,g7)
    c: DistanceY(g11) = 405
    c: DistanceX(g11,g12) = 14
    c: DistanceX(g12,g10) = 23.5
    c: DistanceX(g8) = 270.5
    c: DistanceX(g8,g9) = 10
    c: DistanceX(g6) = 293
    c: DistanceX(g6,g7) = 30
    c: Horizontal(g16,g17)
    c: Horizontal(g17,g18)
    c: Horizontal(g18,g15)
    c: Horizontal(g15,g14)
    c: Horizontal(g14,g13)
    c: DistanceX(g13) = 100
    c: DistanceY(g13) = 250
    c: DistanceX(g13,g14) = 40
    c: DistanceX(g15) = 177
    c: DistanceX(g15,g16) = 66
    c: DistanceX(g17) = 275
    c: DistanceX(g17,g18) = 50
    c: Equal(g13, g14-g18) x5
    c: Equal(g13,g5)
    c: Equal(g13,g4)
    c: Equal(g13,g3)
    c: Equal(g13,g2)
    c: Equal(g13,g1)
    c: Equal(g13,g11)
    c: Equal(g13,g12)
    c: Equal(g13,g10)
    c: Equal(g13,g8)
    c: Equal(g13,g9)
    c: Equal(g13,g6)
    c: Equal(g13,g7)
    c: Diameter(g13) = 3.25
    c: DistanceX(g1) = 151
FEATURE [Part::Extrusion] Extrude084  label="level2Cuts010"
  Base = -> Sketch186
  Dir = (0,-1,2e-16)
  DirMode = 2
  FaceMakerClass = Part::FaceMakerBullseye
  FaceMakerMode = 3
  LengthFwd = 25
  LengthRev = 0
  Solid = true
  Symmetric = false
FEATURE [Sketcher::SketchObject] Sketch187
  ArcFitTolerance = 0
  FullyConstrained = true
  MakeInternals = false
  Placement = pos=(0,-36,0) rot=(1,0,0;1.5708rad)
  sketch-geometry (19):
    g0: Circle CenterX=151 CenterY=387 CenterZ=0 NormalX=0 NormalY=0 NormalZ=1 AngleXU=0 Radius=1.625
    g1: Circle CenterX=151 CenterY=312.5 CenterZ=0 NormalX=0 NormalY=0 NormalZ=1 AngleXU=0 Radius=1.625
    g2: Circle CenterX=240 CenterY=312.5 CenterZ=0 NormalX=0 NormalY=0 NormalZ=1 AngleXU=0 Radius=1.625
    g3: Circle CenterX=260 CenterY=312.5 CenterZ=0 NormalX=0 NormalY=0 NormalZ=1 AngleXU=0 Radius=1.625
    g4: Circle CenterX=303 CenterY=312.5 CenterZ=0 NormalX=0 NormalY=0 NormalZ=1 AngleXU=0 Radius=1.625
    g5: Circle CenterX=312.5 CenterY=312.5 CenterZ=0 NormalX=0 NormalY=0 NormalZ=1 AngleXU=0 Radius=1.625
    g6: Circle CenterX=293 CenterY=405 CenterZ=0 NormalX=0 NormalY=0 NormalZ=1 AngleXU=0 Radius=1.625
    g7: Circle CenterX=323 CenterY=405 CenterZ=0 NormalX=0 NormalY=0 NormalZ=1 AngleXU=0 Radius=1.625
    g8: Circle CenterX=270.5 CenterY=405 CenterZ=0 NormalX=0 NormalY=0 NormalZ=1 AngleXU=0 Radius=1.625
    g9: Circle CenterX=280.5 CenterY=405 CenterZ=0 NormalX=0 NormalY=0 NormalZ=1 AngleXU=0 Radius=1.625
    g10: Circle CenterX=250.5 CenterY=405 CenterZ=0 NormalX=0 NormalY=0 NormalZ=1 AngleXU=0 Radius=1.625
    g11: Circle CenterX=213 CenterY=405 CenterZ=0 NormalX=0 NormalY=0 NormalZ=1 AngleXU=0 Radius=1.625
    g12: Circle CenterX=227 CenterY=405 CenterZ=0 NormalX=0 NormalY=0 NormalZ=1 AngleXU=0 Radius=1.625
    g13: Circle CenterX=100 CenterY=250 CenterZ=0 NormalX=0 NormalY=0 NormalZ=1 AngleXU=0 Radius=1.625
    g14: Circle CenterX=140 CenterY=250 CenterZ=0 NormalX=0 NormalY=0 NormalZ=1 AngleXU=0 Radius=1.625
    g15: Circle CenterX=177 CenterY=250 CenterZ=0 NormalX=0 NormalY=0 NormalZ=1 AngleXU=0 Radius=1.625
    g16: Circle CenterX=243 CenterY=250 CenterZ=0 NormalX=0 NormalY=0 NormalZ=1 AngleXU=0 Radius=1.625
    g17: Circle CenterX=275 CenterY=250 CenterZ=0 NormalX=0 NormalY=0 NormalZ=1 AngleXU=0 Radius=1.625
    g18: Circle CenterX=325 CenterY=250 CenterZ=0 NormalX=0 NormalY=0 NormalZ=1 AngleXU=0 Radius=1.625
  constraints (53):
    c: Vertical(g1,g0)
    c: DistanceY(g1) = 312.5
    c: DistanceY(g1,g0) = 74.5
    c: Equal(g1,g0)
    c: Horizontal(g2,g3)
    c: Horizontal(g3,g4)
    c: Horizontal(g4,g5)
    c: DistanceX(g2) = 240
    c: Horizontal(g2,g1)
    c: DistanceX(g3) = 260
    c: DistanceX(g4) = 303
    c: DistanceX(g4,g5) = 9.5
    c: DistanceX(g11) = 213
    c: Horizontal(g12,g11)
    c: Horizontal(g11,g10)
    c: Horizontal(g10,g8)
    c: Horizontal(g8,g9)
    c: Horizontal(g9,g6)
    c: Horizontal(g6,g7)
    c: DistanceY(g11) = 405
    c: DistanceX(g11,g12) = 14
    c: DistanceX(g12,g10) = 23.5
    c: DistanceX(g8) = 270.5
    c: DistanceX(g8,g9) = 10
    c: DistanceX(g6) = 293
    c: DistanceX(g6,g7) = 30
    c: Horizontal(g16,g17)
    c: Horizontal(g17,g18)
    c: Horizontal(g18,g15)
    c: Horizontal(g15,g14)
    c: Horizontal(g14,g13)
    c: DistanceX(g13) = 100
    c: DistanceY(g13) = 250
    c: DistanceX(g13,g14) = 40
    c: DistanceX(g15) = 177
    c: DistanceX(g15,g16) = 66
    c: DistanceX(g17) = 275
    c: DistanceX(g17,g18) = 50
    c: Equal(g13, g14-g18) x5
    c: Equal(g13,g5)
    c: Equal(g13,g4)
    c: Equal(g13,g3)
    c: Equal(g13,g2)
    c: Equal(g13,g1)
    c: Equal(g13,g11)
    c: Equal(g13,g12)
    c: Equal(g13,g10)
    c: Equal(g13,g8)
    c: Equal(g13,g9)
    c: Equal(g13,g6)
    c: Equal(g13,g7)
    c: Diameter(g13) = 3.25
    c: DistanceX(g1) = 151
FEATURE [Part::Extrusion] Extrude085  label="level2Cuts011"
  Base = -> Sketch187
  Dir = (0,-1,2e-16)
  DirMode = 2
  FaceMakerClass = Part::FaceMakerBullseye
  FaceMakerMode = 3
  LengthFwd = 25
  LengthRev = 0
  Solid = true
  Symmetric = false
FEATURE [Part::Cut] Cut045  label="UVHolder"
  Base = -> Fusion148
  Tool = -> Extrude085
FEATURE [Sketcher::SketchObject] Sketch192
  ArcFitTolerance = 0
  FullyConstrained = true
  MakeInternals = false
  sketch-geometry (6):
    g0: Circle CenterX=74 CenterY=-167 CenterZ=0 NormalX=0 NormalY=0 NormalZ=1 AngleXU=0 Radius=1.125
    g1: Circle CenterX=40 CenterY=-167 CenterZ=0 NormalX=0 NormalY=0 NormalZ=1 AngleXU=0 Radius=1.125
    g2: Circle CenterX=40 CenterY=-133 CenterZ=0 NormalX=0 NormalY=0 NormalZ=1 AngleXU=0 Radius=1.125
    g3: Circle CenterX=74 CenterY=-133 CenterZ=0 NormalX=0 NormalY=0 NormalZ=1 AngleXU=0 Radius=1.125
    g4: Circle CenterX=57 CenterY=-150 CenterZ=0 NormalX=0 NormalY=0 NormalZ=1 AngleXU=0 Radius=27.5
    g5: Circle CenterX=57 CenterY=-150 CenterZ=0 NormalX=0 NormalY=0 NormalZ=1 AngleXU=0 Radius=21
  constraints (17):
    c: Equal(g3,g0)
    c: Equal(g3,g1)
    c: Equal(g3,g2)
    c: Diameter(g3) = 2.25
    c: DistanceX(g1) = 40
    c: DistanceY(g1) = -167
    c: DistanceY(g1,g0) = 0
    c: DistanceX(g2,g1) = 0
    c: DistanceY(g1,g2) = 34
    c: DistanceY(g2,g3) = 0
    c: DistanceX(g2,g3) = 34
    c: DistanceX(g0,g3) = 0
    c: Coincident(g5,g4)
    c: DistanceX(g4) = 57
    c: DistanceY(g4) = -150
    c: Diameter(g5) = 42
    c: Diameter(g4) = 55
FEATURE [Part::Extrusion] Extrude090  label="cameraHolder002"
  Base = -> Sketch192
  Dir = (0,0,1)
  DirMode = 2
  FaceMakerClass = Part::FaceMakerBullseye
  FaceMakerMode = 3
  LengthFwd = 8.25
  LengthRev = 0
  Placement = pos=(153,-120,400) rot=(1,0,0;1.5708rad)
  Solid = true
  Symmetric = false
FEATURE [Part::MultiFuse] Fusion176  label="cameraHolder003"
  Shapes = -> [Box066,Cut031,Extrude090]
FEATURE [Part::Cut] Cut050  label="cameraHolder004"
  Base = -> Fusion176
  Tool = -> Fusion177
FEATURE [Part::Cut] Cut051  label="cameraHolder005"
  Base = -> Cut050
  Tool = -> Extrude084
FEATURE [Part::Box] Box004  label="guva"
  AttacherType = Attacher::AttachEngine3D
  Height = 2
  Length = 19
  Placement = pos=(-9.5,-88,0) rot=(0,0,1;0rad)
  Width = 10
FEATURE [Part::Box] Box005  label="as7265x"
  AttacherType = Attacher::AttachEngine3D
  Height = 2
  Length = 36
  Placement = pos=(-75,-170.5,110) rot=(0,0,1;0rad)
  Width = 41
FEATURE [Part::Cylinder] Cylinder098
  Angle = 360
  AttacherType = Attacher::AttachEngine3D
  FirstAngle = 0
  Height = 10
  Placement = pos=(6.5,-83,0) rot=(0,0,1;0rad)
  Radius = 1.13
  SecondAngle = 0
FEATURE [Part::Cut] Cut018  label="guva001"
  Base = -> Box004
  Placement = pos=(0,0,110) rot=(0,0,1;0rad)
  Tool = -> Cylinder098
FEATURE [Part::Feature] Part__Feature330  label="elpCamera"
  Placement = pos=(57,-150,90) rot=(0,0,1;0rad)
  shape: bbox 38 x 38 x 25.12 mm, 164 faces (baked)
FEATURE [Part::Feature] Part__Feature105  label="Printed Circuit Board"
  shape: bbox 25.4 x 17.78 x 1.6 mm, 42 faces (baked)
FEATURE [Part::Feature] Part__Feature106  label="EAHC2835WD6"
  shape: bbox 3.513 x 2.813 x 0.7485 mm, 108 faces, 4 solids (baked)
FEATURE [Part::Feature] Part__Feature107  label="AS7341 v2"
  Placement = pos=(0,-0.339822,1.6) rot=(0,0,1;0rad)
  shape: bbox 2 x 3.1 x 1.1 mm, 267 faces, 26 solids (baked)
FEATURE [Part::Feature] Part__Feature108  label="CAPC-0805-T0.95-BN v1"
  Placement = pos=(-5.01759,-3.15294,1.6) rot=(0,0,1;0rad)
  shape: bbox 2.1 x 1.35 x 0.95 mm, 42 faces (baked)
FEATURE [Part::Feature] Part__Feature109  label="CAPC-0805-T0.95-BN v002"
  Placement = pos=(-5.48627,2.66154,1.6) rot=(0,0,-1;1.5708rad)
  shape: bbox 1.35 x 2.1 x 0.95 mm, 42 faces (baked)
FEATURE [Part::Feature] Part__Feature110  label="CAPC-0805-T0.95-BN v003"
  Placement = pos=(-3.43627,2.66154,1.6) rot=(0,0,-1;1.5708rad)
  shape: bbox 1.35 x 2.1 x 0.95 mm, 42 faces (baked)
FEATURE [Part::Feature] Part__Feature111  label="CAPC-0603-T0.9-BN v1"
  Placement = pos=(-1.69987,-3.28475,1.6) rot=(0,0,1;0rad)
  shape: bbox 1.7 x 0.9 x 0.9 mm, 42 faces (baked)
FEATURE [Part::Feature] Part__Feature112  label="BODY_MF06A"
  Placement = pos=(0,0,0.762) rot=(0.57735,-0.57735,-0.57735;2.0944rad)
  shape: bbox 1.601 x 2.921 x 1.016 mm, 42 faces (baked)
FEATURE [Part::Feature] Part__Feature113  label="LEAD_MF06A"
  Placement = pos=(-0.9652,-0.9525,0.1016) rot=(0.57735,-0.57735,-0.57735;2.0944rad)
  shape: bbox 0.6223 x 0.3749 x 0.8636 mm, 14 faces (baked)
FEATURE [Part::Feature] Part__Feature114  label="LEAD_MF06A001"
  Placement = pos=(-0.9652,0,0.1016) rot=(0.57735,-0.57735,-0.57735;2.0944rad)
  shape: bbox 0.6223 x 0.3749 x 0.8636 mm, 14 faces (baked)
FEATURE [Part::Feature] Part__Feature115  label="LEAD_MF06A002"
  Placement = pos=(-0.9652,0.9525,0.1016) rot=(0.57735,-0.57735,-0.57735;2.0944rad)
  shape: bbox 0.6223 x 0.3749 x 0.8636 mm, 14 faces (baked)
FEATURE [Part::Feature] Part__Feature116  label="LEAD_MF06A003"
  Placement = pos=(0.9652,-0.9525,0.1016) rot=(0.57735,0.57735,0.57735;2.0944rad)
  shape: bbox 0.6223 x 0.3749 x 0.8636 mm, 14 faces (baked)
FEATURE [Part::Feature] Part__Feature117  label="LEAD_MF06A004"
  Placement = pos=(0.9652,0,0.1016) rot=(0.57735,0.57735,0.57735;2.0944rad)
  shape: bbox 0.6223 x 0.3749 x 0.8636 mm, 14 faces (baked)
FEATURE [Part::Feature] Part__Feature118  label="LEAD_MF06A005"
  Placement = pos=(0.9652,0.9525,0.1016) rot=(0.57735,0.57735,0.57735;2.0944rad)
  shape: bbox 0.6223 x 0.3749 x 0.8636 mm, 14 faces (baked)
FEATURE [Part::Feature] Part__Feature119  label="SOT363 v2"
  Placement = pos=(4.97054,-0.645171,1.675) rot=(0,0,1;3.14159rad)
  shape: bbox 2.1 x 2 x 1.1 mm, 94 faces, 7 solids (baked)
FEATURE [Part::Feature] Part__Feature120  label="LED 0603 single color v1"
  Placement = pos=(-9.18406,3.72778,1.60762) rot=(0,0,1;1.5708rad)
  shape: bbox 1.961 x 0.7932 x 0.7145 mm, 63 faces, 5 solids (baked)
FEATURE [Part::Feature] Part__Feature121  label="RESC-0603 v1"
  Placement = pos=(4.83432,-3.67461,1.6) rot=(0,0,1;0rad)
  shape: bbox 1.7 x 0.9 x 0.55 mm, 52 faces, 3 solids (baked)
FEATURE [Part::Feature] Part__Feature122  label="RESC-0603 v002"
  Placement = pos=(-7.14949,3.61248,1.6) rot=(0,0,-1;1.5708rad)
  shape: bbox 0.9 x 1.7 x 0.55 mm, 52 faces, 3 solids (baked)
FEATURE [Part::Feature] Part__Feature123  label="YC164_RESPACK v1"
  Placement = pos=(2.99591,1.52916,1.6) rot=(0,0,1;0rad)
  shape: bbox 3.2 x 1.6 x 0.61 mm, 172 faces (baked)
FEATURE [Part::Feature] Part__Feature124  label="qwicc v2"
  Placement = pos=(-10.8364,0.0607456,1.65) rot=(0,0,-1;1.5708rad)
  shape: bbox 4.95 x 6 x 2.96 mm, 229 faces, 7 solids (baked)
FEATURE [Part::Feature] Part__Feature125  label="qwicc v003"
  Placement = pos=(10.8256,0.00556102,1.65) rot=(0,0,1;1.5708rad)
  shape: bbox 4.95 x 6 x 2.96 mm, 229 faces, 7 solids (baked)
FEATURE [App::Part] sot_23_6_v2  label="sot-23-6 v2"
  Group = -> [Part__Feature112,Part__Feature113,Part__Feature114,Part__Feature115,Part__Feature116,Part__Feature117,Part__Feature118]
  Origin = -> Origin008
  Placement = pos=(-4.47945,-0.603742,1.69152) rot=(0,0,1;0rad)
FEATURE [App::Part] Adafruit_AS7341_STEMMA_QT_v2  label="ltr390"
  Group = -> [Part__Feature105,Part__Feature106,Part__Feature107,Part__Feature108,Part__Feature109,Part__Feature110,Part__Feature111,sot_23_6_v2,Part__Feature119,Part__Feature120,Part__Feature121,Part__Feature122,Part__Feature123,Part__Feature124,Part__Feature125]
  Origin = -> Origin009
  Placement = pos=(0,-98,110) rot=(0,0,1;0rad)
FEATURE [Part::Cylinder] Cylinder
  Angle = 360
  AttacherType = Attacher::AttachEngine3D
  FirstAngle = 0
  Height = 2.6
  Radius = 40
  SecondAngle = 0
FEATURE [Part::Cylinder] Cylinder001  label="Cylinder_in"
  Angle = 360
  AttacherType = Attacher::AttachEngine3D
  FirstAngle = 0
  Height = 2.6
  Radius = 30
  SecondAngle = 0
FEATURE [Part::Cut] Cut001  label="Base_flat"
  Base = -> Cylinder
  Tool = -> Cylinder001
FEATURE [Part::Cylinder] Cylinder002 .. Cylinder005  x4 (patterned run collapsed; names and placements below)
  Angle = 360
  AttacherType = Attacher::AttachEngine3D
  FirstAngle = 0
  Height = 10
  Radius = 1.6
  SecondAngle = 0
  placements: all 4 at pos=(35.5,0,0) rot=(0,0,1;0rad)
FEATURE [Part::Mirroring] Part__Mirroring  label="Cylinder003 (Mirror #1)"
  Base = (0,0,0)
  Normal = (1,0,0)
  Source = -> Cylinder003
FEATURE [Part::MultiFuse] Fusion178  label="hole01"
  Shapes = -> [Cylinder002,Part__Mirroring]
FEATURE [Part::Mirroring] Part__Mirroring001  label="Cylinder003 (Mirror #1)001"
  Base = (0,0,0)
  Normal = (1,0,0)
  Source = -> Cylinder005
FEATURE [Part::MultiFuse] Fusion001  label="hole002"
  Placement = pos=(0,0,0) rot=(0,0,1;1.5708rad)
  Shapes = -> [Cylinder004,Part__Mirroring001]
FEATURE [Part::MultiFuse] Fusion002  label="Holes"
  Placement = pos=(0,0,-4) rot=(0,0,1;0rad)
  Shapes = -> [Fusion178,Fusion001]
FEATURE [Part::Cut] Cut002
  Base = -> Cut001
  Tool = -> Fusion002
FEATURE [Part::Sphere] Sphere  label="Sphere_out"
  Angle1 = -90
  Angle2 = 90
  Angle3 = 180
  AttacherType = Attacher::AttachEngine3D
  Placement = pos=(0,0,0) rot=(1,0,0;1.5708rad)
  Radius = 30
FEATURE [Part::Sphere] Sphere001  label="Sphere_in"
  Angle1 = -90
  Angle2 = 90
  Angle3 = 180
  AttacherType = Attacher::AttachEngine3D
  Placement = pos=(0,0,0) rot=(1,0,0;1.5708rad)
  Radius = 28.7
FEATURE [Part::Cut] Cut  label="Dome"
  Base = -> Sphere
  Tool = -> Sphere001
FEATURE [Part::MultiFuse] Fusion003  label="lightDome"
  Placement = pos=(0,-323,593) rot=(0,0,1;0rad)
  Shapes = -> [Cut,Cut002]
FEATURE [Part::Feature] Part__Feature331  label="15275A57_Corner Bracket001"
  Placement = pos=(-210,0,592.5) rot=(0,0.707107,0.707107;3.14159rad)
  shape: bbox 50.01 x 54.99 x 45.01 mm, 103 faces (baked)
FEATURE [Part::Box] Box070  label="guva002"
  AttacherType = Attacher::AttachEngine3D
  Height = 2
  Length = 19
  Placement = pos=(-9.5,-88,0) rot=(0,0,1;0rad)
  Width = 10
FEATURE [Part::FeaturePython] Clone002  label="tSlotTop001"  # WARN: FeaturePython — macro-defined, semantics opaque (R4)
  AttacherType = Attacher::AttachEngine3D
  Fuse = false
  Placement = pos=(0,0,-7) rot=(1,0,0;1.5708rad)
  Scale = (1,1,3)
FEATURE [Part::FeaturePython] Clone027  label="M3Nut050"  # WARN: FeaturePython — macro-defined, semantics opaque (R4)
  AttacherType = Attacher::AttachEngine3D
  Fuse = false
  Placement = pos=(0,0,4.5) rot=(0,0,1;0rad)
  Scale = (1.1,1.1,5)
FEATURE [Part::FeaturePython] Clone028  label="M3Nut051"  # WARN: FeaturePython — macro-defined, semantics opaque (R4)
  AttacherType = Attacher::AttachEngine3D
  Fuse = false
  Placement = pos=(0,0,0.9) rot=(0,0,1;0rad)
  Scale = (1.1,1.1,1)
FEATURE [Part::FeaturePython] Clone029  label="M3Nut052"  # WARN: FeaturePython — macro-defined, semantics opaque (R4)
  AttacherType = Attacher::AttachEngine3D
  Fuse = false
  Placement = pos=(0,0,4.5) rot=(0,0,1;0rad)
  Scale = (1.1,1.1,5)
FEATURE [Part::FeaturePython] Clone030  label="M3Nut053"  # WARN: FeaturePython — macro-defined, semantics opaque (R4)
  AttacherType = Attacher::AttachEngine3D
  Fuse = false
  Placement = pos=(0,0,0.9) rot=(0,0,1;0rad)
  Scale = (1.1,1.1,1)
FEATURE [Part::FeaturePython] Clone031  label="M3Nut054"  # WARN: FeaturePython — macro-defined, semantics opaque (R4)
  AttacherType = Attacher::AttachEngine3D
  Fuse = false
  Placement = pos=(0,0,4.5) rot=(0,0,1;0rad)
  Scale = (1.1,1.1,5)
FEATURE [Part::FeaturePython] Clone032  label="M3Nut055"  # WARN: FeaturePython — macro-defined, semantics opaque (R4)
  AttacherType = Attacher::AttachEngine3D
  Fuse = false
  Placement = pos=(0,0,0.9) rot=(0,0,1;0rad)
  Scale = (1.1,1.1,1)
FEATURE [Part::FeaturePython] Clone033  label="M3Nut056"  # WARN: FeaturePython — macro-defined, semantics opaque (R4)
  AttacherType = Attacher::AttachEngine3D
  Fuse = false
  Placement = pos=(0,0,4.5) rot=(0,0,1;0rad)
  Scale = (1.1,1.1,5)
FEATURE [Part::FeaturePython] Clone034  label="M3Nut057"  # WARN: FeaturePython — macro-defined, semantics opaque (R4)
  AttacherType = Attacher::AttachEngine3D
  Fuse = false
  Placement = pos=(0,0,0.9) rot=(0,0,1;0rad)
  Scale = (1.1,1.1,1)
FEATURE [Part::FeaturePython] Clone035  label="M3Nut058"  # WARN: FeaturePython — macro-defined, semantics opaque (R4)
  AttacherType = Attacher::AttachEngine3D
  Fuse = false
  Placement = pos=(0,0,4.5) rot=(0,0,1;0rad)
  Scale = (1.1,1.1,5)
FEATURE [Part::FeaturePython] Clone036  label="M3Nut059"  # WARN: FeaturePython — macro-defined, semantics opaque (R4)
  AttacherType = Attacher::AttachEngine3D
  Fuse = false
  Placement = pos=(0,0,0.9) rot=(0,0,1;0rad)
  Scale = (1.1,1.1,1)
FEATURE [Part::FeaturePython] Clone037  label="M3Nut060"  # WARN: FeaturePython — macro-defined, semantics opaque (R4)
  AttacherType = Attacher::AttachEngine3D
  Fuse = false
  Placement = pos=(0,0,4.5) rot=(0,0,1;0rad)
  Scale = (1.1,1.1,5)
FEATURE [Part::FeaturePython] Clone038  label="M3Nut061"  # WARN: FeaturePython — macro-defined, semantics opaque (R4)
  AttacherType = Attacher::AttachEngine3D
  Fuse = false
  Placement = pos=(0,0,0.9) rot=(0,0,1;0rad)
  Scale = (1.1,1.1,1)
FEATURE [Part::FeaturePython] Clone039  label="M3Nut062"  # WARN: FeaturePython — macro-defined, semantics opaque (R4)
  AttacherType = Attacher::AttachEngine3D
  Fuse = false
  Placement = pos=(0,0,4.5) rot=(0,0,1;0rad)
  Scale = (1.1,1.1,5)
FEATURE [Part::FeaturePython] Clone040  label="M3Nut063"  # WARN: FeaturePython — macro-defined, semantics opaque (R4)
  AttacherType = Attacher::AttachEngine3D
  Fuse = false
  Placement = pos=(0,0,0.9) rot=(0,0,1;0rad)
  Scale = (1.1,1.1,1)
FEATURE [Part::FeaturePython] Clone041  label="M3Nut064"  # WARN: FeaturePython — macro-defined, semantics opaque (R4)
  AttacherType = Attacher::AttachEngine3D
  Fuse = false
  Placement = pos=(0,0,4.5) rot=(0,0,1;0rad)
  Scale = (1.1,1.1,5)
FEATURE [Part::FeaturePython] Clone042  label="M3Nut065"  # WARN: FeaturePython — macro-defined, semantics opaque (R4)
  AttacherType = Attacher::AttachEngine3D
  Fuse = false
  Placement = pos=(0,0,0.9) rot=(0,0,1;0rad)
  Scale = (1.1,1.1,1)
FEATURE [Part::FeaturePython] Clone043  label="M3Nut066"  # WARN: FeaturePython — macro-defined, semantics opaque (R4)
  AttacherType = Attacher::AttachEngine3D
  Fuse = false
  Placement = pos=(0,0,4.5) rot=(0,0,1;0rad)
  Scale = (1.1,1.1,5)
FEATURE [Part::FeaturePython] Clone044  label="M3Nut067"  # WARN: FeaturePython — macro-defined, semantics opaque (R4)
  AttacherType = Attacher::AttachEngine3D
  Fuse = false
  Placement = pos=(0,0,0.9) rot=(0,0,1;0rad)
  Scale = (1.1,1.1,1)
FEATURE [Part::FeaturePython] Clone045  label="M3Nut068"  # WARN: FeaturePython — macro-defined, semantics opaque (R4)
  AttacherType = Attacher::AttachEngine3D
  Fuse = false
  Placement = pos=(0,0,4.5) rot=(0,0,1;0rad)
  Scale = (1.1,1.1,5)
FEATURE [Part::FeaturePython] Clone046  label="M3Nut069"  # WARN: FeaturePython — macro-defined, semantics opaque (R4)
  AttacherType = Attacher::AttachEngine3D
  Fuse = false
  Placement = pos=(0,0,0.9) rot=(0,0,1;0rad)
  Scale = (1.1,1.1,1)
FEATURE [Part::FeaturePython] Clone047  label="M3Nut070"  # WARN: FeaturePython — macro-defined, semantics opaque (R4)
  AttacherType = Attacher::AttachEngine3D
  Fuse = false
  Placement = pos=(0,0,4.5) rot=(0,0,1;0rad)
  Scale = (1.1,1.1,5)
FEATURE [Part::FeaturePython] Clone048  label="M3Nut071"  # WARN: FeaturePython — macro-defined, semantics opaque (R4)
  AttacherType = Attacher::AttachEngine3D
  Fuse = false
  Placement = pos=(0,0,0.9) rot=(0,0,1;0rad)
  Scale = (1.1,1.1,1)
FEATURE [Part::FeaturePython] Clone049  label="M3Nut072"  # WARN: FeaturePython — macro-defined, semantics opaque (R4)
  AttacherType = Attacher::AttachEngine3D
  Fuse = false
  Placement = pos=(0,0,4.5) rot=(0,0,1;0rad)
  Scale = (1.1,1.1,5)
FEATURE [Part::FeaturePython] Clone050  label="M3Nut073"  # WARN: FeaturePython — macro-defined, semantics opaque (R4)
  AttacherType = Attacher::AttachEngine3D
  Fuse = false
  Placement = pos=(0,0,0.9) rot=(0,0,1;0rad)
  Scale = (1.1,1.1,1)
FEATURE [Part::FeaturePython] Clone051  label="M3Nut074"  # WARN: FeaturePython — macro-defined, semantics opaque (R4)
  AttacherType = Attacher::AttachEngine3D
  Fuse = false
  Placement = pos=(0,0,4.5) rot=(0,0,1;0rad)
  Scale = (1.1,1.1,5)
FEATURE [Part::FeaturePython] Clone052  label="M3Nut075"  # WARN: FeaturePython — macro-defined, semantics opaque (R4)
  AttacherType = Attacher::AttachEngine3D
  Fuse = false
  Placement = pos=(0,0,0.9) rot=(0,0,1;0rad)
  Scale = (1.1,1.1,1)
FEATURE [Part::Cylinder] Cylinder199
  Angle = 360
  AttacherType = Attacher::AttachEngine3D
  FirstAngle = 0
  Height = 10
  Placement = pos=(6.5,-83,0) rot=(0,0,1;0rad)
  Radius = 1.13
  SecondAngle = 0
FEATURE [Part::Cut] Cut147  label="guva003"
  Base = -> Box070
  Placement = pos=(80,-176.25,28) rot=(0,0,1;0rad)
  Tool = -> Cylinder199
FEATURE [Part::Cylinder] Cylinder139
  Angle = 360
  AttacherType = Attacher::AttachEngine3D
  FirstAngle = 0
  Height = 2.6
  Radius = 40
  SecondAngle = 0
FEATURE [Part::Cylinder] Cylinder140  label="Cylinder_in005"
  Angle = 360
  AttacherType = Attacher::AttachEngine3D
  FirstAngle = 0
  Height = 2.6
  Radius = 30
  SecondAngle = 0
FEATURE [Part::Cut] Cut066  label="Base_flat005"
  Base = -> Cylinder139
  Tool = -> Cylinder140
FEATURE [Part::Cylinder] Cylinder141
  Angle = 360
  AttacherType = Attacher::AttachEngine3D
  FirstAngle = 0
  Height = 2.6
  Radius = 40
  SecondAngle = 0
FEATURE [Part::Cylinder] Cylinder142  label="Cylinder_in006"
  Angle = 360
  AttacherType = Attacher::AttachEngine3D
  FirstAngle = 0
  Height = 2.6
  Radius = 30
  SecondAngle = 0
FEATURE [Part::Cut] Cut069  label="Base_flat006"
  Base = -> Cylinder141
  Tool = -> Cylinder142
FEATURE [Part::Cylinder] Cylinder143
  Angle = 360
  AttacherType = Attacher::AttachEngine3D
  FirstAngle = 0
  Height = 2.6
  Radius = 40
  SecondAngle = 0
FEATURE [Part::Cylinder] Cylinder144  label="Cylinder_in007"
  Angle = 360
  AttacherType = Attacher::AttachEngine3D
  FirstAngle = 0
  Height = 2.6
  Radius = 30
  SecondAngle = 0
FEATURE [Part::Cut] Cut072  label="Base_flat007"
  Base = -> Cylinder143
  Tool = -> Cylinder144
FEATURE [Part::Cylinder] Cylinder157 .. Cylinder169  x13 (patterned run collapsed; names and placements below)
  Angle = 360
  AttacherType = Attacher::AttachEngine3D
  FirstAngle = 0
  Height = 9
  Radius = 2
  SecondAngle = 0
FEATURE [Part::MultiFuse] Fusion223
  Shapes = -> [Clone027,Cylinder157]
FEATURE [Part::MultiFuse] Fusion224  label="m3NutCut014"
  Placement = pos=(-80,-235,-22.5) rot=(0.707107,-0.707107,0;3.14159rad)
  Shapes = -> [Clone028,Fusion223]
FEATURE [Part::MultiFuse] Fusion227
  Shapes = -> [Clone029,Cylinder158]
FEATURE [Part::MultiFuse] Fusion228  label="m3NutCut015"
  Placement = pos=(-115,-270,-22.5) rot=(1,0,0;3.14159rad)
  Shapes = -> [Clone030,Fusion227]
FEATURE [Part::MultiFuse] Fusion229
  Shapes = -> [Clone031,Cylinder159]
FEATURE [Part::MultiFuse] Fusion230  label="m3NutCut016"
  Placement = pos=(-45,-270,-22.5) rot=(1,0,0;3.14159rad)
  Shapes = -> [Clone032,Fusion229]
FEATURE [Part::MultiFuse] Fusion231
  Shapes = -> [Clone033,Cylinder160]
FEATURE [Part::MultiFuse] Fusion232  label="m3NutCut017"
  Placement = pos=(-35,-270,-22.5) rot=(1,0,0;3.14159rad)
  Shapes = -> [Clone034,Fusion231]
FEATURE [Part::MultiFuse] Fusion233
  Shapes = -> [Clone035,Cylinder161]
FEATURE [Part::MultiFuse] Fusion234  label="m3NutCut018"
  Placement = pos=(35,-270,-22.5) rot=(1,0,0;3.14159rad)
  Shapes = -> [Clone036,Fusion233]
FEATURE [Part::MultiFuse] Fusion235
  Shapes = -> [Clone037,Cylinder162]
FEATURE [Part::MultiFuse] Fusion236  label="m3NutCut019"
  Placement = pos=(45,-270,-22.5) rot=(1,0,0;3.14159rad)
  Shapes = -> [Clone038,Fusion235]
FEATURE [Part::MultiFuse] Fusion237
  Shapes = -> [Clone039,Cylinder163]
FEATURE [Part::MultiFuse] Fusion238  label="m3NutCut020"
  Placement = pos=(115,-270,-22.5) rot=(1,0,0;3.14159rad)
  Shapes = -> [Clone040,Fusion237]
FEATURE [Part::MultiFuse] Fusion239
  Shapes = -> [Clone041,Cylinder164]
FEATURE [Part::MultiFuse] Fusion240  label="m3NutCut021"
  Placement = pos=(-80,-235,-22.5) rot=(0.707107,-0.707107,0;3.14159rad)
  Shapes = -> [Clone042,Fusion239]
FEATURE [Part::MultiFuse] Fusion241
  Shapes = -> [Clone043,Cylinder165]
FEATURE [Part::MultiFuse] Fusion242  label="m3NutCut022"
  Placement = pos=(0,-235,-22.5) rot=(0.707107,-0.707107,0;3.14159rad)
  Shapes = -> [Clone044,Fusion241]
FEATURE [Part::MultiFuse] Fusion243
  Shapes = -> [Clone045,Cylinder166]
FEATURE [Part::MultiFuse] Fusion244  label="m3NutCut023"
  Placement = pos=(80,-235,-22.5) rot=(0.707107,-0.707107,0;3.14159rad)
  Shapes = -> [Clone046,Fusion243]
FEATURE [Part::MultiFuse] Fusion245
  Shapes = -> [Clone047,Cylinder167]
FEATURE [Part::MultiFuse] Fusion246  label="m3NutCut024"
  Placement = pos=(80,-305,-22.5) rot=(0.707107,-0.707107,0;3.14159rad)
  Shapes = -> [Clone048,Fusion245]
FEATURE [Part::MultiFuse] Fusion247
  Shapes = -> [Clone049,Cylinder168]
FEATURE [Part::MultiFuse] Fusion248  label="m3NutCut025"
  Placement = pos=(1.4e-14,-305,-22.5) rot=(0.707107,-0.707107,0;3.14159rad)
  Shapes = -> [Clone050,Fusion247]
FEATURE [Part::MultiFuse] Fusion249
  Shapes = -> [Clone051,Cylinder169]
FEATURE [Part::MultiFuse] Fusion250  label="m3NutCut026"
  Placement = pos=(-80,-305,-22.5) rot=(0.707107,-0.707107,0;3.14159rad)
  Shapes = -> [Clone052,Fusion249]
FEATURE [Part::MultiFuse] Fusion251  label="m3NutCuts"
  Placement = pos=(0,0,-0.5) rot=(0,0,1;0rad)
  Shapes = -> [Fusion224,Fusion228,Fusion230,Fusion232,Fusion234,Fusion236,Fusion238,Fusion240,Fusion242,Fusion244,Fusion246,Fusion248,Fusion250]
FEATURE [Part::Feature] Part__Feature332  label="Printed Circuit Board001"
  shape: bbox 25.4 x 20.32 x 1.65 mm, 39 faces (baked)
FEATURE [Part::Feature] Part__Feature333  label="Printed Circuit Board002"
  shape: bbox 25.4 x 17.78 x 1.6 mm, 42 faces (baked)
FEATURE [Part::Feature] Part__Feature334  label="EAHC2835WD007"
  shape: bbox 3.513 x 2.813 x 0.7485 mm, 108 faces, 4 solids (baked)
FEATURE [Part::Feature] Part__Feature335  label="AS7341 v003"
  Placement = pos=(0,-0.339822,1.6) rot=(0,0,1;0rad)
  shape: bbox 2 x 3.1 x 1.1 mm, 267 faces, 26 solids (baked)
FEATURE [Part::Feature] Part__Feature336  label="CAPC-0805-T0.95-BN v004"
  Placement = pos=(-5.01759,-3.15294,1.6) rot=(0,0,1;0rad)
  shape: bbox 2.1 x 1.35 x 0.95 mm, 42 faces (baked)
FEATURE [Part::Feature] Part__Feature337  label="CAPC-0805-T0.95-BN v005"
  Placement = pos=(-5.48627,2.66154,1.6) rot=(0,0,-1;1.5708rad)
  shape: bbox 1.35 x 2.1 x 0.95 mm, 42 faces (baked)
FEATURE [Part::Feature] Part__Feature338  label="CAPC-0805-T0.95-BN v006"
  Placement = pos=(-3.43627,2.66154,1.6) rot=(0,0,-1;1.5708rad)
  shape: bbox 1.35 x 2.1 x 0.95 mm, 42 faces (baked)
FEATURE [Part::Feature] Part__Feature339  label="CAPC-0603-T0.9-BN v002"
  Placement = pos=(-1.69987,-3.28475,1.6) rot=(0,0,1;0rad)
  shape: bbox 1.7 x 0.9 x 0.9 mm, 42 faces (baked)
FEATURE [Part::Feature] Part__Feature340  label="BODY_MF06A001"
  Placement = pos=(0,0,0.762) rot=(0.57735,-0.57735,-0.57735;2.0944rad)
  shape: bbox 1.601 x 2.921 x 1.016 mm, 42 faces (baked)
FEATURE [Part::Feature] Part__Feature341  label="LEAD_MF06A006"
  Placement = pos=(-0.9652,-0.9525,0.1016) rot=(0.57735,-0.57735,-0.57735;2.0944rad)
  shape: bbox 0.6223 x 0.3749 x 0.8636 mm, 14 faces (baked)
FEATURE [Part::Feature] Part__Feature342  label="LEAD_MF06A007"
  Placement = pos=(-0.9652,0,0.1016) rot=(0.57735,-0.57735,-0.57735;2.0944rad)
  shape: bbox 0.6223 x 0.3749 x 0.8636 mm, 14 faces (baked)
FEATURE [Part::Feature] Part__Feature343  label="LEAD_MF06A008"
  Placement = pos=(-0.9652,0.9525,0.1016) rot=(0.57735,-0.57735,-0.57735;2.0944rad)
  shape: bbox 0.6223 x 0.3749 x 0.8636 mm, 14 faces (baked)
FEATURE [Part::Feature] Part__Feature344  label="LEAD_MF06A009"
  Placement = pos=(0.9652,-0.9525,0.1016) rot=(0.57735,0.57735,0.57735;2.0944rad)
  shape: bbox 0.6223 x 0.3749 x 0.8636 mm, 14 faces (baked)
FEATURE [Part::Feature] Part__Feature345  label="LEAD_MF06A010"
  Placement = pos=(0.9652,0,0.1016) rot=(0.57735,0.57735,0.57735;2.0944rad)
  shape: bbox 0.6223 x 0.3749 x 0.8636 mm, 14 faces (baked)
FEATURE [Part::Feature] Part__Feature346  label="LEAD_MF06A011"
  Placement = pos=(0.9652,0.9525,0.1016) rot=(0.57735,0.57735,0.57735;2.0944rad)
  shape: bbox 0.6223 x 0.3749 x 0.8636 mm, 14 faces (baked)
FEATURE [Part::Feature] Part__Feature347  label="SOT363 v003"
  Placement = pos=(4.97054,-0.645171,1.675) rot=(0,0,1;3.14159rad)
  shape: bbox 2.1 x 2 x 1.1 mm, 94 faces, 7 solids (baked)
FEATURE [Part::Feature] Part__Feature348  label="LED 0603 single color v002"
  Placement = pos=(-9.18406,3.72778,1.60762) rot=(0,0,1;1.5708rad)
  shape: bbox 1.961 x 0.7932 x 0.7145 mm, 63 faces, 5 solids (baked)
FEATURE [Part::Feature] Part__Feature349  label="RESC-0603 v003"
  Placement = pos=(4.83432,-3.67461,1.6) rot=(0,0,1;0rad)
  shape: bbox 1.7 x 0.9 x 0.55 mm, 52 faces, 3 solids (baked)
FEATURE [Part::Feature] Part__Feature350  label="RESC-0603 v004"
  Placement = pos=(-7.14949,3.61248,1.6) rot=(0,0,-1;1.5708rad)
  shape: bbox 0.9 x 1.7 x 0.55 mm, 52 faces, 3 solids (baked)
FEATURE [Part::Feature] Part__Feature351  label="YC164_RESPACK v002"
  Placement = pos=(2.99591,1.52916,1.6) rot=(0,0,1;0rad)
  shape: bbox 3.2 x 1.6 x 0.61 mm, 172 faces (baked)
FEATURE [Part::Feature] Part__Feature352  label="qwicc v004"
  Placement = pos=(-10.8364,0.0607456,1.65) rot=(0,0,-1;1.5708rad)
  shape: bbox 4.95 x 6 x 2.96 mm, 229 faces, 7 solids (baked)
FEATURE [Part::Feature] Part__Feature353  label="qwicc v005"
  Placement = pos=(10.8256,0.00556102,1.65) rot=(0,0,1;1.5708rad)
  shape: bbox 4.95 x 6 x 2.96 mm, 229 faces, 7 solids (baked)
FEATURE [Part::Feature] Part__Feature354  label="elpCamera001"
  Placement = pos=(0,-270,13) rot=(0,0,1;0rad)
  shape: bbox 38 x 38 x 25.12 mm, 164 faces (baked)
FEATURE [Part::Feature] Part__Feature355  label="RESC-2512-R100 v2"
  Placement = pos=(0.0152473,1.04463,1.65) rot=(0,0,1;3.14159rad)
  shape: bbox 6.417 x 3.317 x 0.6674 mm, 219 faces, 7 solids (baked)
FEATURE [Part::Feature] Part__Feature356  label="LED 0603 single color v003"
  Placement = pos=(-9.06678,4.19381,1.65762) rot=(0,0,1;1.5708rad)
  shape: bbox 1.961 x 0.7932 x 0.7145 mm, 63 faces, 5 solids (baked)
FEATURE [Part::Feature] Part__Feature357  label="CAPC-0805-T0.95-BN v007"
  Placement = pos=(-4.32049,-3.03839,1.65) rot=(0,0,-1;1.5708rad)
  shape: bbox 1.35 x 2.1 x 0.95 mm, 42 faces (baked)
FEATURE [Part::Feature] Part__Feature358  label="CAPC-0603-T0.9-BN v003"
  Placement = pos=(-2.53733,-2.97022,1.65) rot=(0,0,-1;1.5708rad)
  shape: bbox 0.9 x 1.7 x 0.9 mm, 42 faces (baked)
FEATURE [Part::Feature] Part__Feature359  label="RESC-0603 v005"
  Placement = pos=(-7.09227,3.55774,1.65) rot=(0,0,-1;1.5708rad)
  shape: bbox 0.9 x 1.7 x 0.55 mm, 52 faces, 3 solids (baked)
FEATURE [Part::Feature] Part__Feature360  label="YC164_RESPACK v003"
  Placement = pos=(2.74348,-1.41846,1.65) rot=(0,0,-1;1.5708rad)
  shape: bbox 1.6 x 3.2 x 0.61 mm, 172 faces (baked)
FEATURE [Part::Feature] Part__Feature361  label="qwicc v1"
  Placement = pos=(-8.57299,-0.000230516,1.345) rot=(0.57735,-0.57735,-0.57735;2.0944rad)
  shape: bbox 4.95 x 6 x 2.96 mm, 229 faces, 7 solids (baked)
FEATURE [Part::Feature] Part__Feature362  label="qwicc v006"
  Placement = pos=(8.61502,0.00281866,1.345) rot=(0.57735,0.57735,0.57735;2.0944rad)
  shape: bbox 4.95 x 6 x 2.96 mm, 229 faces, 7 solids (baked)
FEATURE [Part::Feature] Part__Feature363  label="B219 v2"
  Placement = pos=(0.00220704,-3.21564,1.62965) rot=(0,0,1;3.14159rad)
  shape: bbox 3.008 x 2.843 x 1.194 mm, 338 faces, 14 solids (baked)
FEATURE [Part::Feature] Part__Feature364  label="Screw Terminal 2pin 3.5mm Pitch v11"
  Placement = pos=(0.115254,6.14583,1.45) rot=(0,0,1;3.14159rad)
  shape: bbox 11.43 x 7.244 x 12 mm, 100 faces, 3 solids (baked)
FEATURE [App::Part] Adafruit_INA219_STEMMA_QT_v7  label="ina219"
  Group = -> [Part__Feature332,Part__Feature355,Part__Feature356,Part__Feature357,Part__Feature358,Part__Feature359,Part__Feature360,Part__Feature361,Part__Feature362,Part__Feature363,Part__Feature364]
  Origin = -> Origin
  Placement = pos=(58,-270,9) rot=(0,-1,0;4.71239rad)
FEATURE [Part::Feature] Part__Feature365  label="Body"
  shape: bbox 15.5 x 16.75 x 29 mm, 21 faces (baked)
FEATURE [Part::Feature] Part__Feature366  label="Body001"
  Placement = pos=(0,0,2) rot=(0,0,1;0rad)
  shape: bbox 17.44 x 17.44 x 14.25 mm, 14 faces (baked)
FEATURE [Part::Feature] Part__Feature367  label="Body002"
  Placement = pos=(0,0,-2.9) rot=(0,0,1;0rad)
  shape: bbox 19 x 19 x 4.75 mm, 25 faces (baked)
FEATURE [Part::Feature] Part__Feature368  label="Body003"
  shape: bbox 16.75 x 16.75 x 0.9 mm, 4 faces (baked)
FEATURE [App::Part] PG7_Gland1
  Group = -> [Part__Feature365,Part__Feature366,Part__Feature367,Part__Feature368]
  Origin = -> Origin012
  Placement = pos=(72,-256,-26) rot=(0,-1,0;3.14159rad)
FEATURE [Part::Feature] Part__Feature369  label="Body004"
  shape: bbox 15.5 x 16.75 x 29 mm, 21 faces (baked)
FEATURE [Part::Feature] Part__Feature370  label="Body005"
  Placement = pos=(0,0,2) rot=(0,0,1;0rad)
  shape: bbox 17.44 x 17.44 x 14.25 mm, 14 faces (baked)
FEATURE [Part::Feature] Part__Feature371  label="Body006"
  Placement = pos=(0,0,-2.9) rot=(0,0,1;0rad)
  shape: bbox 19 x 19 x 4.75 mm, 25 faces (baked)
FEATURE [Part::Feature] Part__Feature372  label="Body007"
  shape: bbox 16.75 x 16.75 x 0.9 mm, 4 faces (baked)
FEATURE [App::Part] PG7_Gland002
  Group = -> [Part__Feature369,Part__Feature370,Part__Feature371,Part__Feature372]
  Origin = -> Origin013
  Placement = pos=(0,-256,-26) rot=(0,-1,0;3.14159rad)
FEATURE [Part::Part2DObjectPython] ShapeString001  # Draft 2D object (typed FeaturePython)
  FontFile = <userpath>/gitHubRepos/3DMints2024/msclns/fonts/montserrat/Montserrat-Regular.otf
  Fuse = false
  Justification = 6
  JustificationReference = 0
  KeepLeftMargin = false
  MakeFace = true
  ObliqueAngle = 0
  Placement = pos=(-15.5,-310,-21) rot=(1,0,0;1.5708rad)
  ScaleToSize = true
  Size = 15
  String = MINTS-AI
  Tracking = 0
FEATURE [Part::Extrusion] Extrude129  label="text"
  Base = -> ShapeString001
  Dir = (0,-1,2e-16)
  DirMode = 2
  FaceMakerClass = Part::FaceMakerBullseye
  FaceMakerMode = 3
  LengthFwd = 2
  LengthRev = 0
  Solid = false
  Symmetric = false
FEATURE [Sketcher::SketchObject] Sketch401
  ArcFitTolerance = 0
  FullyConstrained = true
  MakeInternals = false
  Placement = pos=(0,0,27.5) rot=(0,0,1;0rad)
  sketch-geometry (2):
    g0: Circle CenterX=0 CenterY=-270 CenterZ=0 NormalX=0 NormalY=0 NormalZ=1 AngleXU=0 Radius=37
    g1: Circle CenterX=0 CenterY=-270 CenterZ=0 NormalX=0 NormalY=0 NormalZ=1 AngleXU=0 Radius=26.5
  constraints (5):
    c: Diameter(g0) = 74
    c: Coincident(g1,g0)
    c: Diameter(g1) = 53
    c: DistanceX(g0) = 0
    c: DistanceY(g0) = -270
FEATURE [Part::Extrusion] Extrude094  label="rubberSeals"
  Base = -> Sketch401
  Dir = (0,0,1)
  DirMode = 2
  FaceMakerClass = Part::FaceMakerBullseye
  FaceMakerMode = 3
  LengthFwd = 3
  LengthRev = 0
  Solid = true
  Symmetric = false
FEATURE [Sketcher::SketchObject] Sketch194
  ArcFitTolerance = 0
  FullyConstrained = true
  MakeInternals = false
  sketch-geometry (4):
    g0: Circle CenterX=0 CenterY=35 CenterZ=0 NormalX=0 NormalY=0 NormalZ=1 AngleXU=0 Radius=1.625
    g1: Circle CenterX=35 CenterY=0 CenterZ=0 NormalX=0 NormalY=0 NormalZ=1 AngleXU=0 Radius=1.625
    g2: Circle CenterX=-35 CenterY=0 CenterZ=0 NormalX=0 NormalY=0 NormalZ=1 AngleXU=0 Radius=1.625
    g3: Circle CenterX=0 CenterY=-35 CenterZ=0 NormalX=0 NormalY=0 NormalZ=1 AngleXU=0 Radius=1.625
  constraints (12):
    c: PointOnObject(g0,g-2)
    c: PointOnObject(g1,g-1)
    c: PointOnObject(g2,g-1)
    c: PointOnObject(g3,g-2)
    c: DistanceY(g3,g-1) = 35
    c: DistanceX(g-1,g1) = 35
    c: DistanceX(g2,g-1) = 35
    c: DistanceY(g-1,g0) = 35
    c: Equal(g1,g3)
    c: Equal(g1,g2)
    c: Equal(g1,g0)
    c: Diameter(g1) = 3.25
FEATURE [Part::Extrusion] Extrude091
  Base = -> Sketch194
  Dir = (0,0,1)
  DirMode = 2
  FaceMakerClass = Part::FaceMakerBullseye
  FaceMakerMode = 3
  LengthFwd = 10
  LengthRev = 0
  Solid = true
  Symmetric = false
FEATURE [Sketcher::SketchObject] Sketch195
  ArcFitTolerance = 0
  FullyConstrained = true
  MakeInternals = false
  sketch-geometry (4):
    g0: Circle CenterX=0 CenterY=35 CenterZ=0 NormalX=0 NormalY=0 NormalZ=1 AngleXU=0 Radius=1.625
    g1: Circle CenterX=35 CenterY=0 CenterZ=0 NormalX=0 NormalY=0 NormalZ=1 AngleXU=0 Radius=1.625
    g2: Circle CenterX=-35 CenterY=0 CenterZ=0 NormalX=0 NormalY=0 NormalZ=1 AngleXU=0 Radius=1.625
    g3: Circle CenterX=0 CenterY=-35 CenterZ=0 NormalX=0 NormalY=0 NormalZ=1 AngleXU=0 Radius=1.625
  constraints (12):
    c: PointOnObject(g0,g-2)
    c: PointOnObject(g1,g-1)
    c: PointOnObject(g2,g-1)
    c: PointOnObject(g3,g-2)
    c: DistanceY(g3,g-1) = 35
    c: DistanceX(g-1,g1) = 35
    c: DistanceX(g2,g-1) = 35
    c: DistanceY(g-1,g0) = 35
    c: Equal(g1,g3)
    c: Equal(g1,g2)
    c: Equal(g1,g0)
    c: Diameter(g1) = 3.25
FEATURE [Part::Extrusion] Extrude092
  Base = -> Sketch195
  Dir = (0,0,1)
  DirMode = 2
  FaceMakerClass = Part::FaceMakerBullseye
  FaceMakerMode = 3
  LengthFwd = 10
  LengthRev = 0
  Solid = true
  Symmetric = false
FEATURE [Sketcher::SketchObject] Sketch196
  ArcFitTolerance = 0
  FullyConstrained = true
  MakeInternals = false
  sketch-geometry (4):
    g0: Circle CenterX=0 CenterY=35 CenterZ=0 NormalX=0 NormalY=0 NormalZ=1 AngleXU=0 Radius=1.625
    g1: Circle CenterX=35 CenterY=0 CenterZ=0 NormalX=0 NormalY=0 NormalZ=1 AngleXU=0 Radius=1.625
    g2: Circle CenterX=-35 CenterY=0 CenterZ=0 NormalX=0 NormalY=0 NormalZ=1 AngleXU=0 Radius=1.625
    g3: Circle CenterX=0 CenterY=-35 CenterZ=0 NormalX=0 NormalY=0 NormalZ=1 AngleXU=0 Radius=1.625
  constraints (12):
    c: PointOnObject(g0,g-2)
    c: PointOnObject(g1,g-1)
    c: PointOnObject(g2,g-1)
    c: PointOnObject(g3,g-2)
    c: DistanceY(g3,g-1) = 35
    c: DistanceX(g-1,g1) = 35
    c: DistanceX(g2,g-1) = 35
    c: DistanceY(g-1,g0) = 35
    c: Equal(g1,g3)
    c: Equal(g1,g2)
    c: Equal(g1,g0)
    c: Diameter(g1) = 3.25
FEATURE [Part::Extrusion] Extrude093
  Base = -> Sketch196
  Dir = (0,0,1)
  DirMode = 2
  FaceMakerClass = Part::FaceMakerBullseye
  FaceMakerMode = 3
  LengthFwd = 10
  LengthRev = 0
  Solid = true
  Symmetric = false
FEATURE [Sketcher::SketchObject] Sketch197
  ArcFitTolerance = 0
  FullyConstrained = true
  MakeInternals = false
  Placement = pos=(0,0,27.5) rot=(0,0,1;0rad)
  sketch-geometry (2):
    g0: Circle CenterX=0 CenterY=-270 CenterZ=0 NormalX=0 NormalY=0 NormalZ=1 AngleXU=0 Radius=37
    g1: Circle CenterX=0 CenterY=-270 CenterZ=0 NormalX=0 NormalY=0 NormalZ=1 AngleXU=0 Radius=26.5
  constraints (5):
    c: Diameter(g0) = 74
    c: Coincident(g1,g0)
    c: Diameter(g1) = 53
    c: DistanceX(g0) = 0
    c: DistanceY(g0) = -270
FEATURE [Part::Extrusion] Extrude095  label="rubberSeals001"
  Base = -> Sketch197
  Dir = (0,0,1)
  DirMode = 2
  FaceMakerClass = Part::FaceMakerBullseye
  FaceMakerMode = 3
  LengthFwd = 3
  LengthRev = 0
  Placement = pos=(-80,0,0) rot=(0,0,1;0rad)
  Solid = true
  Symmetric = false
FEATURE [Sketcher::SketchObject] Sketch198
  ArcFitTolerance = 0
  FullyConstrained = true
  MakeInternals = false
  Placement = pos=(0,0,27.5) rot=(0,0,1;0rad)
  sketch-geometry (2):
    g0: Circle CenterX=0 CenterY=-270 CenterZ=0 NormalX=0 NormalY=0 NormalZ=1 AngleXU=0 Radius=37
    g1: Circle CenterX=0 CenterY=-270 CenterZ=0 NormalX=0 NormalY=0 NormalZ=1 AngleXU=0 Radius=26.5
  constraints (5):
    c: Diameter(g0) = 74
    c: Coincident(g1,g0)
    c: Diameter(g1) = 53
    c: DistanceX(g0) = 0
    c: DistanceY(g0) = -270
FEATURE [Part::Extrusion] Extrude096  label="rubberSeals002"
  Base = -> Sketch198
  Dir = (0,0,1)
  DirMode = 2
  FaceMakerClass = Part::FaceMakerBullseye
  FaceMakerMode = 3
  LengthFwd = 3
  LengthRev = 0
  Placement = pos=(80,0,0) rot=(0,0,1;0rad)
  Solid = true
  Symmetric = false
FEATURE [Sketcher::SketchObject] Sketch199
  ArcFitTolerance = 0
  FullyConstrained = true
  MakeInternals = false
  sketch-geometry (8):
    g0: LineSegment StartX=-98 StartY=-249.5 StartZ=0 EndX=-62 EndY=-249.5 EndZ=0
    g1: LineSegment StartX=-62 StartY=-249.5 StartZ=0 EndX=-62 EndY=-290.5 EndZ=0
    g2: LineSegment StartX=-62 StartY=-290.5 StartZ=0 EndX=-98 EndY=-290.5 EndZ=0
    g3: LineSegment StartX=-98 StartY=-290.5 StartZ=0 EndX=-98 EndY=-249.5 EndZ=0
    g4: Circle CenterX=-90 CenterY=-252.5 CenterZ=0 NormalX=0 NormalY=0 NormalZ=1 AngleXU=0 Radius=1.625
    g5: Circle CenterX=-70 CenterY=-252.5 CenterZ=0 NormalX=0 NormalY=0 NormalZ=1 AngleXU=0 Radius=1.625
    g6: Circle CenterX=-90 CenterY=-287.5 CenterZ=0 NormalX=0 NormalY=0 NormalZ=1 AngleXU=0 Radius=1.625
    g7: Circle CenterX=-70 CenterY=-287.5 CenterZ=0 NormalX=0 NormalY=0 NormalZ=1 AngleXU=0 Radius=1.625
  constraints (24):
    c: Coincident(g0,g1)
    c: Coincident(g1,g2)
    c: Coincident(g2,g3)
    c: Coincident(g3,g0)
    c: Horizontal(g0)
    c: Horizontal(g2)
    c: Vertical(g1)
    c: Vertical(g3)
    c: DistanceY(g2) = -290.5
    c: DistanceY(g2,g0) = 41
    c: Horizontal(g6,g7)
    c: Horizontal(g4,g5)
    c: Vertical(g4,g6)
    c: Vertical(g7,g5)
    c: DistanceY(g6) = -287.5
    c: DistanceY(g6,g4) = 35
    c: DistanceX(g6,g7) = 20
    c: Equal(g5,g7)
    c: Equal(g5,g6)
    c: Equal(g5,g4)
    c: Diameter(g5) = 3.25
    c: DistanceX(g2,g1) = 36
    c: DistanceX(g1) = -62
    c: DistanceX(g7,g1) = 8
FEATURE [Part::Extrusion] Extrude097  label="as7265x001"
  Base = -> Sketch199
  Dir = (0,0,1)
  DirMode = 2
  FaceMakerClass = Part::FaceMakerBullseye
  FaceMakerMode = 3
  LengthFwd = 2
  LengthRev = 0
  Placement = pos=(0,0,28) rot=(0,0,1;0rad)
  Solid = true
  Symmetric = false
FEATURE [Sketcher::SketchObject] Sketch220
  ArcFitTolerance = 0
  FullyConstrained = true
  MakeInternals = false
  Placement = pos=(0,0,-25) rot=(0,0,1;0rad)
  sketch-geometry (12):
    g0: Circle CenterX=-115 CenterY=-270 CenterZ=0 NormalX=0 NormalY=0 NormalZ=1 AngleXU=0 Radius=1.625
    g1: Circle CenterX=-80 CenterY=-235 CenterZ=0 NormalX=0 NormalY=0 NormalZ=1 AngleXU=0 Radius=1.625
    g2: Circle CenterX=-80 CenterY=-305 CenterZ=0 NormalX=0 NormalY=0 NormalZ=1 AngleXU=0 Radius=1.625
    g3: Circle CenterX=-45 CenterY=-270 CenterZ=0 NormalX=0 NormalY=0 NormalZ=1 AngleXU=0 Radius=1.625
    g4: Circle CenterX=-35 CenterY=-270 CenterZ=0 NormalX=0 NormalY=0 NormalZ=1 AngleXU=0 Radius=1.625
    g5: Circle CenterX=0 CenterY=-305 CenterZ=0 NormalX=0 NormalY=0 NormalZ=1 AngleXU=0 Radius=1.625
    g6: Circle CenterX=0 CenterY=-235 CenterZ=0 NormalX=0 NormalY=0 NormalZ=1 AngleXU=0 Radius=1.625
    g7: Circle CenterX=35 CenterY=-270 CenterZ=0 NormalX=0 NormalY=0 NormalZ=1 AngleXU=0 Radius=1.625
    g8: Circle CenterX=45 CenterY=-270 CenterZ=0 NormalX=0 NormalY=0 NormalZ=1 AngleXU=0 Radius=1.625
    g9: Circle CenterX=80 CenterY=-235 CenterZ=0 NormalX=0 NormalY=0 NormalZ=1 AngleXU=0 Radius=1.625
    g10: Circle CenterX=115 CenterY=-270 CenterZ=0 NormalX=0 NormalY=0 NormalZ=1 AngleXU=0 Radius=1.625
    g11: Circle CenterX=80 CenterY=-305 CenterZ=0 NormalX=0 NormalY=0 NormalZ=1 AngleXU=0 Radius=1.625
  constraints (36):
    c: PointOnObject(g5,g-2)
    c: PointOnObject(g6,g-2)
    c: Equal(g8,g1)
    c: Equal(g8,g6)
    c: Equal(g8,g9)
    c: Equal(g8,g2)
    c: Equal(g8,g5)
    c: Equal(g8,g11)
    c: Equal(g8,g0)
    c: Equal(g8,g3)
    c: Equal(g8,g4)
    c: Equal(g8,g7)
    c: Equal(g8,g10)
    c: Diameter(g8) = 3.25
    c: Horizontal(g0,g3)
    c: Horizontal(g3,g4)
    c: Horizontal(g4,g7)
    c: Horizontal(g7,g8)
    c: Horizontal(g8,g10)
    c: Horizontal(g2,g5)
    c: Horizontal(g5,g11)
    c: Horizontal(g6,g9)
    c: Horizontal(g1,g6)
    c: Vertical(g2,g1)
    c: Vertical(g9,g11)
    c: DistanceY(g0) = -270
    c: DistanceX(g0) = -115
    c: DistanceX(g0,g2) = 35
    c: DistanceY(g2,g0) = 35
    c: DistanceY(g0,g1) = 35
    c: DistanceX(g0,g3) = 70
    c: DistanceX(g4) = -35
    c: DistanceX(g7) = 35
    c: DistanceX(g8) = 45
    c: DistanceX(g8,g10) = 70
    c: DistanceX(g8,g11) = 35
FEATURE [Part::Extrusion] Extrude119  label="m3Cuts"
  Base = -> Sketch220
  Dir = (0,0,1)
  DirMode = 2
  FaceMakerClass = Part::FaceMakerBullseye
  FaceMakerMode = 3
  LengthFwd = 60
  LengthRev = 0
  Solid = true
  Symmetric = false
FEATURE [Sketcher::SketchObject] Sketch224
  ArcFitTolerance = 0
  FullyConstrained = true
  MakeInternals = false
  Placement = pos=(24,0,0) rot=(0.57735,0.57735,0.57735;2.0944rad)
  sketch-geometry (2):
    g0: Circle CenterX=-277.6 CenterY=19.15 CenterZ=0 NormalX=0 NormalY=0 NormalZ=1 AngleXU=0 Radius=1.6
    g1: Circle CenterX=-262.4 CenterY=19.15 CenterZ=0 NormalX=0 NormalY=0 NormalZ=1 AngleXU=0 Radius=1.6
  constraints (6):
    c: Horizontal(g1,g0)
    c: Equal(g1,g0)
    c: Diameter(g1) = 3.2
    c: DistanceX(g0) = -277.6
    c: DistanceY(g0) = 19.15
    c: DistanceX(g0,g1) = 15.2
FEATURE [Part::Extrusion] Extrude123
  Base = -> Sketch224
  Dir = (1,0,0)
  DirMode = 2
  FaceMakerClass = Part::FaceMakerBullseye
  FaceMakerMode = 3
  LengthFwd = 30
  LengthRev = 0
  Solid = true
  Symmetric = false
FEATURE [Sketcher::SketchObject] Sketch225
  ArcFitTolerance = 0
  FullyConstrained = true
  MakeInternals = false
  Placement = pos=(0,0,-22) rot=(0,0,1;0rad)
  sketch-geometry (14):
    g0: LineSegment StartX=-2e-16 StartY=-267 StartZ=0 EndX=9.52628 EndY=-261.5 EndZ=0
    g1: LineSegment StartX=9.52628 StartY=-261.5 StartZ=0 EndX=9.52628 EndY=-250.5 EndZ=0
    g2: LineSegment StartX=9.52628 StartY=-250.5 StartZ=0 EndX=2e-16 EndY=-245 EndZ=0
    g3: LineSegment StartX=0 StartY=-245 StartZ=0 EndX=-9.52628 EndY=-250.5 EndZ=0
    g4: LineSegment StartX=-9.52628 StartY=-250.5 StartZ=0 EndX=-9.52628 EndY=-261.5 EndZ=0
    g5: LineSegment StartX=-9.52628 StartY=-261.5 StartZ=0 EndX=-2e-16 EndY=-267 EndZ=0
    g6: Circle [constr] CenterX=0 CenterY=-256 CenterZ=0 NormalX=0 NormalY=0 NormalZ=1 AngleXU=0 Radius=11
    g7: LineSegment StartX=67 StartY=-267 StartZ=0 EndX=76.5263 EndY=-261.5 EndZ=0
    g8: LineSegment StartX=76.5263 StartY=-261.5 StartZ=0 EndX=76.5263 EndY=-250.5 EndZ=0
    g9: LineSegment StartX=76.5263 StartY=-250.5 StartZ=0 EndX=67 EndY=-245 EndZ=0
    g10: LineSegment StartX=67 StartY=-245 StartZ=0 EndX=57.4737 EndY=-250.5 EndZ=0
    g11: LineSegment StartX=57.4737 StartY=-250.5 StartZ=0 EndX=57.4737 EndY=-261.5 EndZ=0
    g12: LineSegment StartX=57.4737 StartY=-261.5 StartZ=0 EndX=67 EndY=-267 EndZ=0
    g13: Circle [constr] CenterX=67 CenterY=-256 CenterZ=0 NormalX=0 NormalY=0 NormalZ=1 AngleXU=0 Radius=11
  constraints (34):
    c: Coincident(g0,g1)
    c: Coincident(g1,g2)
    c: Coincident(g2,g3)
    c: Coincident(g3,g4)
    c: Coincident(g4,g5)
    c: Coincident(g5,g0)
    c: Equal(g0, g1-g5) x5
    c: PointOnObject(g0,g6)
    c: PointOnObject(g1,g6)
    c: PointOnObject(g2,g6)
    c: PointOnObject(g3,g6)
    c: PointOnObject(g4,g6)
    c: PointOnObject(g5,g6)
    c: Coincident(g7,g8)
    c: Coincident(g8,g9)
    c: Coincident(g9,g10)
    c: Coincident(g10,g11)
    c: Coincident(g11,g12)
    c: Coincident(g12,g7)
    c: Equal(g7, g8-g12) x5
    c: PointOnObject(g7,g13)
    c: PointOnObject(g8,g13)
    c: PointOnObject(g9,g13)
    c: PointOnObject(g10,g13)
    c: PointOnObject(g11,g13)
    c: PointOnObject(g12,g13)
    c: Horizontal(g6,g13)
    c: Vertical(g6,g2)
    c: DistanceX(g6) = 0
    c: DistanceY(g6) = -256
    c: Diameter(g6) = 22
    c: Vertical(g13,g7)
    c: Diameter(g13) = 22
    c: DistanceX(g13) = 67
FEATURE [Part::Extrusion] Extrude124
  Base = -> Sketch225
  Dir = (0,0,1)
  DirMode = 2
  FaceMakerClass = Part::FaceMakerBullseye
  FaceMakerMode = 3
  LengthFwd = 6
  LengthRev = 0
  Solid = true
  Symmetric = false
FEATURE [Part::MultiFuse] Fusion253  label="pg7Cuts"
  Shapes = -> [Extrude123,Extrude124]
FEATURE [Sketcher::SketchObject] Sketch226
  ArcFitTolerance = 0
  FullyConstrained = true
  MakeInternals = false
  Placement = pos=(0,-232,0) rot=(1,0,0;1.5708rad)
  sketch-geometry (8):
    g0: LineSegment StartX=-13 StartY=6 StartZ=0 EndX=13 EndY=6 EndZ=0
    g1: LineSegment StartX=13 StartY=6 StartZ=0 EndX=13 EndY=-20 EndZ=0
    g2: LineSegment StartX=13 StartY=-20 StartZ=0 EndX=-13 EndY=-20 EndZ=0
    g3: LineSegment StartX=-13 StartY=-20 StartZ=0 EndX=-13 EndY=6 EndZ=0
    g4: LineSegment StartX=-18 StartY=11 StartZ=0 EndX=18 EndY=11 EndZ=0
    g5: LineSegment StartX=18 StartY=11 StartZ=0 EndX=18 EndY=-25 EndZ=0
    g6: LineSegment StartX=18 StartY=-25 StartZ=0 EndX=-18 EndY=-25 EndZ=0
    g7: LineSegment StartX=-18 StartY=-25 StartZ=0 EndX=-18 EndY=11 EndZ=0
  constraints (24):
    c: Coincident(g0,g1)
    c: Coincident(g1,g2)
    c: Coincident(g2,g3)
    c: Coincident(g3,g0)
    c: Horizontal(g0)
    c: Horizontal(g2)
    c: Vertical(g1)
    c: Vertical(g3)
    c: Coincident(g4,g5)
    c: Coincident(g5,g6)
    c: Coincident(g6,g7)
    c: Coincident(g7,g4)
    c: Horizontal(g4)
    c: Horizontal(g6)
    c: Vertical(g5)
    c: Vertical(g7)
    c: DistanceY(g6) = -25
    c: DistanceX(g2,g1) = 26
    c: DistanceX(g6) = -18
    c: DistanceX(g6,g2) = 5
    c: DistanceX(g5) = 18
    c: DistanceY(g2,g0) = 26
    c: DistanceY(g6,g2) = 5
    c: DistanceY(g0,g4) = 5
FEATURE [Part::Extrusion] Extrude125
  Base = -> Sketch226
  Dir = (0,-1,2e-16)
  DirMode = 2
  FaceMakerClass = Part::FaceMakerBullseye
  FaceMakerMode = 3
  LengthFwd = 32
  LengthRev = 0
  Reversed = true
  Solid = true
  Symmetric = false
FEATURE [Sketcher::SketchObject] Sketch227
  ArcFitTolerance = 0
  FullyConstrained = true
  MakeInternals = false
  Placement = pos=(0,0,11) rot=(0,0,1;0rad)
  sketch-geometry (1):
    g0: Circle CenterX=0 CenterY=-215 CenterZ=0 NormalX=0 NormalY=0 NormalZ=1 AngleXU=0 Radius=3.125
  constraints (3):
    c: DistanceX(g0) = 0
    c: DistanceY(g0) = -215
    c: Diameter(g0) = 6.25
FEATURE [Part::Extrusion] Extrude127
  Base = -> Sketch227
  Dir = (0,0,1)
  DirMode = 2
  FaceMakerClass = Part::FaceMakerBullseye
  FaceMakerMode = 3
  LengthFwd = 36
  LengthRev = 0
  Reversed = true
  Solid = true
  Symmetric = false
FEATURE [Sketcher::SketchObject] Sketch228
  ArcFitTolerance = 0
  FullyConstrained = true
  MakeInternals = false
  Placement = pos=(-18,0,0) rot=(0.57735,0.57735,0.57735;2.0944rad)
  sketch-geometry (1):
    g0: Circle CenterX=-215 CenterY=-7 CenterZ=0 NormalX=0 NormalY=0 NormalZ=1 AngleXU=0 Radius=3.25
  constraints (3):
    c: DistanceX(g0) = -215
    c: DistanceY(g0) = -7
    c: Diameter(g0) = 6.5
FEATURE [Part::Extrusion] Extrude126
  Base = -> Sketch228
  Dir = (1,0,0)
  DirMode = 2
  FaceMakerClass = Part::FaceMakerBullseye
  FaceMakerMode = 3
  LengthFwd = 36
  LengthRev = 0
  Solid = true
  Symmetric = false
FEATURE [Part::MultiFuse] Fusion252
  Shapes = -> [Extrude127,Extrude126]
FEATURE [Part::Cut] Cut082  label="in003"
  Base = -> Extrude125
  Tool = -> Fusion252
FEATURE [Part::Fillet] Fillet005
  Base = -> Cut082
  EdgeLinks = -> Cut082 [?Edge1,?Edge4,?Edge6,?Edge22]
  Edges = 4 edges r=2: [Edge1,Edge4,Edge6,Edge22]
FEATURE [Part::Fillet] Fillet006  label="tSlotHolder"
  Base = -> Fillet005
  EdgeLinks = -> Fillet005 [Edge4,Edge18,Edge20,Edge21,Edge22,Edge23,Edge24,Edge25,Edge26,Edge27,Edge28,Edge29]
  Edges = 12 edges r=2: [Edge4,Edge18,Edge20,Edge21,Edge22,Edge23,Edge24,Edge25,Edge26,Edge27,Edge28,Edge29]
FEATURE [Sketcher::SketchObject] Sketch229
  ArcFitTolerance = 0
  FullyConstrained = true
  MakeInternals = false
  Placement = pos=(0,0,-25) rot=(0,0,1;0rad)
  sketch-geometry (2):
    g0: Circle CenterX=0 CenterY=-256 CenterZ=0 NormalX=0 NormalY=0 NormalZ=1 AngleXU=0 Radius=6
    g1: Circle CenterX=67 CenterY=-256 CenterZ=0 NormalX=0 NormalY=0 NormalZ=1 AngleXU=0 Radius=6
  constraints (6):
    c: DistanceY(g0) = -256
    c: Horizontal(g0,g1)
    c: DistanceX(g0,g1) = 67
    c: DistanceX(g0) = 0
    c: Equal(g0,g1)
    c: Diameter(g0) = 12
FEATURE [Part::Extrusion] Extrude128  label="outCut"
  Base = -> Sketch229
  Dir = (0,0,1)
  DirMode = 2
  FaceMakerClass = Part::FaceMakerBullseye
  FaceMakerMode = 3
  LengthFwd = 5
  LengthRev = 0
  Solid = true
  Symmetric = false
FEATURE [Part::MultiFuse] Fusion260  label="mainCuts"
  Shapes = -> [Fusion253,Fusion251,Extrude128,Extrude119]
FEATURE [Sketcher::SketchObject] Sketch233
  ArcFitTolerance = 0
  FullyConstrained = true
  MakeInternals = false
  Placement = pos=(0,0,-25) rot=(0,0,1;0rad)
  sketch-geometry (8):
    g0: ArcOfCircle CenterX=-80 CenterY=-270 CenterZ=0 NormalX=0 NormalY=0 NormalZ=1 AngleXU=0 Radius=40 StartAngle=1.5708 EndAngle=4.71239
    g1: ArcOfCircle CenterX=80 CenterY=-270 CenterZ=0 NormalX=0 NormalY=0 NormalZ=1 AngleXU=0 Radius=40 StartAngle=4.71239 EndAngle=7.85398
    g2: LineSegment StartX=-80 StartY=-310 StartZ=0 EndX=80 EndY=-310 EndZ=0
    g3: LineSegment StartX=80 StartY=-230 StartZ=0 EndX=-80 EndY=-230 EndZ=0
    g4: ArcOfCircle CenterX=-80 CenterY=-270 CenterZ=0 NormalX=0 NormalY=0 NormalZ=1 AngleXU=0 Radius=30 StartAngle=1.5708 EndAngle=4.71239
    g5: ArcOfCircle CenterX=80 CenterY=-270 CenterZ=0 NormalX=0 NormalY=0 NormalZ=1 AngleXU=0 Radius=30 StartAngle=4.71239 EndAngle=7.85398
    g6: LineSegment StartX=-80 StartY=-300 StartZ=0 EndX=80 EndY=-300 EndZ=0
    g7: LineSegment StartX=80 StartY=-240 StartZ=0 EndX=-80 EndY=-240 EndZ=0
  constraints (18):
    c: Tangent(g0,g2) = -1.5708
    c: Tangent(g2,g1) = -1.5708
    c: Tangent(g1,g3) = -1.5708
    c: Tangent(g3,g0) = -1.5708
    c: Equal(g0,g1)
    c: Horizontal(g2)
    c: DistanceY(g0) = -270
    c: DistanceX(g0) = -80
    c: DistanceX(g1) = 80
    c: Diameter(g0) = 80
    c: Tangent(g4,g6) = -1.5708
    c: Tangent(g6,g5) = -1.5708
    c: Tangent(g5,g7) = -1.5708
    c: Tangent(g7,g4) = -1.5708
    c: Equal(g4,g5)
    c: Coincident(g4,g0)
    c: Coincident(g5,g1)
    c: Diameter(g4) = 60
FEATURE [Part::Extrusion] Extrude133  label="outerBorder001"
  Base = -> Sketch233
  Dir = (0,0,1)
  DirMode = 2
  FaceMakerClass = Part::FaceMakerBullseye
  FaceMakerMode = 3
  LengthFwd = 53
  LengthRev = 0
  Solid = true
  Symmetric = false
FEATURE [Part::Fillet] Fillet013  label="outerHold001"
  Base = -> Extrude133
  EdgeLinks = -> Extrude133 [Edge9]
  Edges = 1 edges r=4: [Edge9]
FEATURE [Sketcher::SketchObject] Sketch234
  ArcFitTolerance = 0
  FullyConstrained = true
  MakeInternals = false
  Placement = pos=(0,0,-25) rot=(0,0,1;0rad)
  sketch-geometry (8):
    g0: ArcOfCircle CenterX=-80 CenterY=-270 CenterZ=0 NormalX=0 NormalY=0 NormalZ=1 AngleXU=0 Radius=30 StartAngle=5.55346 EndAngle=7.01291
    g1: LineSegment StartX=-57.6393 StartY=-250 StartZ=0 EndX=-22.3607 EndY=-250 EndZ=0
    g2: LineSegment StartX=-57.6393 StartY=-290 StartZ=0 EndX=-22.3607 EndY=-290 EndZ=0
    g3: ArcOfCircle CenterX=0 CenterY=-270 CenterZ=0 NormalX=0 NormalY=0 NormalZ=1 AngleXU=0 Radius=30 StartAngle=2.41186 EndAngle=3.87132
    g4: ArcOfCircle CenterX=0 CenterY=-270 CenterZ=0 NormalX=0 NormalY=0 NormalZ=1 AngleXU=0 Radius=30 StartAngle=5.55346 EndAngle=7.01291
    g5: ArcOfCircle CenterX=80 CenterY=-270 CenterZ=0 NormalX=0 NormalY=0 NormalZ=1 AngleXU=0 Radius=30 StartAngle=2.41186 EndAngle=3.87132
    g6: LineSegment StartX=22.3607 StartY=-250 StartZ=0 EndX=57.6393 EndY=-250 EndZ=0
    g7: LineSegment StartX=57.6393 StartY=-290 StartZ=0 EndX=22.3607 EndY=-290 EndZ=0
  constraints (27):
    c: Coincident(g1,g0)
    c: Horizontal(g1)
    c: Coincident(g2,g0)
    c: Horizontal(g2)
    c: PointOnObject(g3,g-2)
    c: Coincident(g3,g2)
    c: Coincident(g3,g1)
    c: Coincident(g4,g3)
    c: Coincident(g6,g4)
    c: Coincident(g6,g5)
    c: Horizontal(g6)
    c: Coincident(g7,g5)
    c: Coincident(g7,g4)
    c: Horizontal(g7)
    c: Horizontal(g0,g4)
    c: Horizontal(g2,g4)
    c: Equal(g3,g0)
    c: Equal(g3,g5)
    c: Equal(g3,g4)
    c: Diameter(g3) = 60
    c: DistanceY(g3) = -270
    c: Vertical(g0,g0)
    c: Vertical(g2,g1)
    c: Vertical(g5,g5)
    c: DistanceX(g5) = 80
    c: DistanceX(g0) = -80
    c: DistanceY(g4) = -250
FEATURE [Part::Extrusion] Extrude134  label="3WayHolds001"
  Base = -> Sketch234
  Dir = (0,0,1)
  DirMode = 2
  FaceMakerClass = Part::FaceMakerBullseye
  FaceMakerMode = 3
  LengthFwd = 53
  LengthRev = 0
  Solid = true
  Symmetric = false
FEATURE [Sketcher::SketchObject] Sketch235
  ArcFitTolerance = 0
  FullyConstrained = true
  MakeInternals = false
  Placement = pos=(0,0,-20) rot=(0,0,1;0rad)
  sketch-geometry (18):
    g0: ArcOfCircle CenterX=-80 CenterY=-240 CenterZ=0 NormalX=0 NormalY=0 NormalZ=1 AngleXU=0 Radius=20 StartAngle=3.48143 EndAngle=5.94335
    g1: ArcOfCircle CenterX=-80 CenterY=-300 CenterZ=0 NormalX=0 NormalY=0 NormalZ=1 AngleXU=0 Radius=20 StartAngle=0.339837 EndAngle=2.80176
    g2: ArcOfCircle CenterX=-80 CenterY=-270 CenterZ=0 NormalX=0 NormalY=0 NormalZ=1 AngleXU=0 Radius=30 StartAngle=0.891123 EndAngle=2.25047
    g3: ArcOfCircle CenterX=-80 CenterY=-270 CenterZ=0 NormalX=0 NormalY=0 NormalZ=1 AngleXU=0 Radius=30 StartAngle=4.03272 EndAngle=5.39206
    g4: LineSegment StartX=65 StartY=-286 StartZ=0 EndX=95 EndY=-286 EndZ=0
    g5: LineSegment StartX=95 StartY=-286 StartZ=0 EndX=95 EndY=-254 EndZ=0
    g6: LineSegment StartX=95 StartY=-254 StartZ=0 EndX=77 EndY=-254 EndZ=0
    g7: LineSegment StartX=77 StartY=-254 StartZ=0 EndX=77 EndY=-274 EndZ=0
    g8: LineSegment StartX=77 StartY=-274 StartZ=0 EndX=65 EndY=-274 EndZ=0
    g9: LineSegment StartX=65 StartY=-274 StartZ=0 EndX=65 EndY=-286 EndZ=0
    g10: Circle CenterX=-90 CenterY=-252.5 CenterZ=0 NormalX=0 NormalY=0 NormalZ=1 AngleXU=0 Radius=2
    g11: Circle CenterX=-70 CenterY=-252.5 CenterZ=0 NormalX=0 NormalY=0 NormalZ=1 AngleXU=0 Radius=2
    g12: Circle CenterX=-90 CenterY=-287.5 CenterZ=0 NormalX=0 NormalY=0 NormalZ=1 AngleXU=0 Radius=2
    g13: Circle CenterX=-70 CenterY=-287.5 CenterZ=0 NormalX=0 NormalY=0 NormalZ=1 AngleXU=0 Radius=2
    g14: Circle CenterX=69.84 CenterY=-280.6 CenterZ=0 NormalX=0 NormalY=0 NormalZ=1 AngleXU=0 Radius=1.6
    g15: Circle CenterX=90.16 CenterY=-280.6 CenterZ=0 NormalX=0 NormalY=0 NormalZ=1 AngleXU=0 Radius=1.6
    g16: Circle CenterX=90.16 CenterY=-267.9 CenterZ=0 NormalX=0 NormalY=0 NormalZ=1 AngleXU=0 Radius=1.6
    g17: Circle CenterX=86.5 CenterY=-259.25 CenterZ=0 NormalX=0 NormalY=0 NormalZ=1 AngleXU=0 Radius=1.6
  constraints (57):
    c: Vertical(g0,g1)
    c: Coincident(g2,g0)
    c: Coincident(g3,g2)
    c: Coincident(g3,g1)
    c: Coincident(g0,g2)
    c: Coincident(g1,g3)
    c: DistanceX(g2) = -80
    c: DistanceY(g2) = -270
    c: Equal(g3,g2)
    c: Diameter(g3) = 60
    c: Equal(g0,g1)
    c: Diameter(g0) = 40
    c: Vertical(g0,g2)
    c: DistanceY(g0) = -240
    c: DistanceY(g1) = -300
    c: Horizontal(g4)
    c: Coincident(g5,g4)
    c: Vertical(g5)
    c: Coincident(g6,g5)
    c: Horizontal(g6)
    c: Coincident(g7,g6)
    c: Vertical(g7)
    c: Coincident(g8,g7)
    c: Horizontal(g8)
    c: Coincident(g9,g8)
    c: Coincident(g9,g4)
    c: Vertical(g9)
    c: DistanceY(g4) = -286
    c: DistanceX(g4) = 65
    c: DistanceY(g4,g8) = 12
    c: DistanceX(g4,g4) = 30
    c: DistanceX(g6,g6) = 18
    c: DistanceY(g5,g5) = 32
    c: Horizontal(g13,g12)
    c: Horizontal(g10,g11)
    c: Vertical(g12,g10)
    c: Vertical(g13,g11)
    c: DistanceX(g12,g2) = 10
    c: DistanceY(g12) = -287.5
    c: DistanceX(g12,g13) = 20
    c: DistanceY(g12,g10) = 35
    c: Equal(g10,g11)
    c: Equal(g10,g13)
    c: Equal(g10,g12)
    c: Diameter(g10) = 4
    c: Horizontal(g14,g15)
    c: Vertical(g15,g16)
    c: DistanceX(g14,g15) = 20.32
    c: DistanceY(g14) = -280.6
    c: DistanceY(g15,g16) = 12.7
    c: DistanceX(g17,g16) = 3.66
    c: DistanceY(g16,g17) = 8.65
    c: Equal(g15,g16)
    c: Equal(g15,g17)
    c: Equal(g15,g14)
    c: Diameter(g15) = 3.2
    c: DistanceX(g4,g14) = 4.84
FEATURE [Part::Extrusion] Extrude135  label="i2cHolds001"
  Base = -> Sketch235
  Dir = (0,0,1)
  DirMode = 2
  FaceMakerClass = Part::FaceMakerBullseye
  FaceMakerMode = 3
  LengthFwd = 48
  LengthRev = 0
  Solid = true
  Symmetric = false
FEATURE [Sketcher::SketchObject] Sketch236
  ArcFitTolerance = 0
  FullyConstrained = true
  MakeInternals = false
  Placement = pos=(0,0,-20) rot=(0,0,1;0rad)
  sketch-geometry (12):
    g0: ArcOfCircle CenterX=-20 CenterY=-290 CenterZ=0 NormalX=0 NormalY=0 NormalZ=1 AngleXU=0 Radius=10 StartAngle=5.49779 EndAngle=8.63938
    g1: ArcOfCircle CenterX=20 CenterY=-290 CenterZ=0 NormalX=0 NormalY=0 NormalZ=1 AngleXU=0 Radius=10 StartAngle=0.785398 EndAngle=3.92699
    g2: ArcOfCircle CenterX=20 CenterY=-250 CenterZ=0 NormalX=0 NormalY=0 NormalZ=1 AngleXU=0 Radius=10 StartAngle=2.35619 EndAngle=5.49779
    g3: ArcOfCircle CenterX=-20 CenterY=-250 CenterZ=0 NormalX=0 NormalY=0 NormalZ=1 AngleXU=0 Radius=10 StartAngle=3.92699 EndAngle=7.06858
    g4: ArcOfCircle CenterX=0 CenterY=-270 CenterZ=0 NormalX=0 NormalY=0 NormalZ=1 AngleXU=0 Radius=30 StartAngle=2.01636 EndAngle=2.69603
    g5: ArcOfCircle CenterX=0 CenterY=-270 CenterZ=0 NormalX=0 NormalY=0 NormalZ=1 AngleXU=0 Radius=30 StartAngle=0.445561 EndAngle=1.12524
    g6: ArcOfCircle CenterX=0 CenterY=-270 CenterZ=0 NormalX=0 NormalY=0 NormalZ=1 AngleXU=0 Radius=30 StartAngle=5.15795 EndAngle=5.83762
    g7: ArcOfCircle CenterX=0 CenterY=-270 CenterZ=0 NormalX=0 NormalY=0 NormalZ=1 AngleXU=0 Radius=30 StartAngle=3.58715 EndAngle=4.26683
    g8: Circle CenterX=-17 CenterY=-253 CenterZ=0 NormalX=0 NormalY=0 NormalZ=1 AngleXU=0 Radius=1.6
    g9: Circle CenterX=17 CenterY=-253 CenterZ=0 NormalX=0 NormalY=0 NormalZ=1 AngleXU=0 Radius=1.6
    g10: Circle CenterX=17 CenterY=-287 CenterZ=0 NormalX=0 NormalY=0 NormalZ=1 AngleXU=0 Radius=1.6
    g11: Circle CenterX=-17 CenterY=-287 CenterZ=0 NormalX=0 NormalY=0 NormalZ=1 AngleXU=0 Radius=1.6
  constraints (41):
    c: Vertical(g0,g3)
    c: Vertical(g1,g2)
    c: Horizontal(g2,g3)
    c: Horizontal(g1,g0)
    c: Equal(g2,g3)
    c: Equal(g2,g0)
    c: Equal(g2,g1)
    c: Diameter(g2) = 20
    c: Horizontal(g0,g1)
    c: Horizontal(g1,g0)
    c: Angle(g0) = 3.14159
    c: Vertical(g0,g3)
    c: Vertical(g0,g3)
    c: Angle(g2) = 3.14159
    c: DistanceY(g0) = -290
    c: Coincident(g4,g3)
    c: Coincident(g4,g3)
    c: Coincident(g5,g4)
    c: Coincident(g5,g2)
    c: Coincident(g5,g2)
    c: Coincident(g6,g4)
    c: Coincident(g6,g1)
    c: Coincident(g6,g1)
    c: Coincident(g7,g4)
    c: Coincident(g7,g0)
    c: Coincident(g7,g0)
    c: DistanceX(g4) = 0
    c: DistanceY(g4) = -270
    c: DistanceX(g0,g4) = 20
    c: DistanceX(g11,g4) = 17
    c: DistanceY(g11,g4) = 17
    c: DistanceX(g4,g10) = 17
    c: DistanceY(g10,g4) = 17
    c: DistanceX(g4,g9) = 17
    c: Vertical(g8,g11)
    c: Horizontal(g8,g9)
    c: DistanceY(g4,g8) = 17
    c: Equal(g10,g9)
    c: Equal(g10,g8)
    c: Equal(g10,g11)
    c: Diameter(g10) = 3.2
FEATURE [Part::Extrusion] Extrude136  label="cameraHold001"
  Base = -> Sketch236
  Dir = (0,0,1)
  DirMode = 2
  FaceMakerClass = Part::FaceMakerBullseye
  FaceMakerMode = 3
  LengthFwd = 31
  LengthRev = 0
  Solid = true
  Symmetric = false
FEATURE [Sketcher::SketchObject] Sketch237
  ArcFitTolerance = 0
  FullyConstrained = true
  MakeInternals = false
  Placement = pos=(85,0,0) rot=(0.57735,0.57735,0.57735;2.0944rad)
  sketch-geometry (2):
    g0: ArcOfCircle CenterX=-270 CenterY=-20 CenterZ=0 NormalX=0 NormalY=0 NormalZ=1 AngleXU=0 Radius=15 StartAngle=0 EndAngle=3.14159
    g1: LineSegment StartX=-285 StartY=-20 StartZ=0 EndX=-255 EndY=-20 EndZ=0
  constraints (7):
    c: Horizontal(g0,g0)
    c: Horizontal(g0,g0)
    c: DistanceX(g0) = -270
    c: DistanceY(g0) = -20
    c: Diameter(g0) = 30
    c: Coincident(g1,g0)
    c: Coincident(g1,g0)
FEATURE [Part::Extrusion] Extrude172  label="WireCutcut003"
  Base = -> Sketch237
  Dir = (1,0,0)
  DirMode = 2
  FaceMakerClass = Part::FaceMakerBullseye
  FaceMakerMode = 3
  LengthFwd = 170
  LengthRev = 0
  Reversed = true
  Solid = true
  Symmetric = false
FEATURE [Sketcher::SketchObject] Sketch238
  ArcFitTolerance = 0
  FullyConstrained = true
  MakeInternals = false
  Placement = pos=(0,0,-25) rot=(0,0,1;0rad)
  sketch-geometry (3):
    g0: Circle CenterX=-80 CenterY=-270.2 CenterZ=0 NormalX=0 NormalY=0 NormalZ=1 AngleXU=0 Radius=40
    g1: Circle CenterX=0 CenterY=-270.2 CenterZ=0 NormalX=0 NormalY=0 NormalZ=1 AngleXU=0 Radius=40
    g2: Circle CenterX=80 CenterY=-270.2 CenterZ=0 NormalX=0 NormalY=0 NormalZ=1 AngleXU=0 Radius=40
  constraints (9):
    c: PointOnObject(g1,g-2)
    c: Diameter(g1) = 80
    c: Diameter(g0) = 80
    c: Horizontal(g1,g0)
    c: DistanceY(g0) = -270.2
    c: DistanceX(g0) = -80
    c: Horizontal(g2,g1)
    c: Diameter(g2) = 80
    c: DistanceX(g1,g2) = 80
FEATURE [Part::Extrusion] Extrude173  label="base006"
  Base = -> Sketch238
  Dir = (0,0,1)
  DirMode = 2
  FaceMakerClass = Part::FaceMakerBullseye
  FaceMakerMode = 3
  LengthFwd = 5
  LengthRev = 0
  Solid = true
  Symmetric = false
FEATURE [Part::Fillet] Fillet014  label="base007"
  Base = -> Extrude173
  EdgeLinks = -> Extrude173 [Edge2,Edge5,Edge8]
  Edges = 3 edges r=4: [Edge2,Edge5,Edge8]
FEATURE [Sketcher::SketchObject] Sketch239
  ArcFitTolerance = 0
  FullyConstrained = true
  MakeInternals = false
  Placement = pos=(0,0,-20) rot=(0,0,1;0rad)
  sketch-geometry (2):
    g0: Circle CenterX=0 CenterY=-270 CenterZ=0 NormalX=0 NormalY=0 NormalZ=1 AngleXU=0 Radius=30
    g1: Circle CenterX=0 CenterY=-270 CenterZ=0 NormalX=0 NormalY=0 NormalZ=1 AngleXU=0 Radius=40
  constraints (5):
    c: PointOnObject(g0,g-2)
    c: Coincident(g1,g0)
    c: DistanceY(g0) = -270
    c: Diameter(g0) = 60
    c: Diameter(g1) = 80
FEATURE [Part::Extrusion] Extrude174  label="domeHolds004"
  Base = -> Sketch239
  Dir = (0,0,1)
  DirMode = 2
  FaceMakerClass = Part::FaceMakerBullseye
  FaceMakerMode = 3
  LengthFwd = 48
  LengthRev = 0
  Solid = true
  Symmetric = false
FEATURE [Sketcher::SketchObject] Sketch240
  ArcFitTolerance = 0
  FullyConstrained = true
  MakeInternals = false
  Placement = pos=(0,0,-20) rot=(0,0,1;0rad)
  sketch-geometry (2):
    g0: Circle CenterX=0 CenterY=-270 CenterZ=0 NormalX=0 NormalY=0 NormalZ=1 AngleXU=0 Radius=30
    g1: Circle CenterX=0 CenterY=-270 CenterZ=0 NormalX=0 NormalY=0 NormalZ=1 AngleXU=0 Radius=40
  constraints (5):
    c: PointOnObject(g0,g-2)
    c: Coincident(g1,g0)
    c: DistanceY(g0) = -270
    c: Diameter(g0) = 60
    c: Diameter(g1) = 80
FEATURE [Part::Extrusion] Extrude175  label="domeHolds005"
  Base = -> Sketch240
  Dir = (0,0,1)
  DirMode = 2
  FaceMakerClass = Part::FaceMakerBullseye
  FaceMakerMode = 3
  LengthFwd = 48
  LengthRev = 0
  Placement = pos=(80,0,0) rot=(0,0,1;0rad)
  Solid = true
  Symmetric = false
FEATURE [Sketcher::SketchObject] Sketch241
  ArcFitTolerance = 0
  FullyConstrained = true
  MakeInternals = false
  Placement = pos=(0,0,-20) rot=(0,0,1;0rad)
  sketch-geometry (2):
    g0: Circle CenterX=0 CenterY=-270 CenterZ=0 NormalX=0 NormalY=0 NormalZ=1 AngleXU=0 Radius=30
    g1: Circle CenterX=0 CenterY=-270 CenterZ=0 NormalX=0 NormalY=0 NormalZ=1 AngleXU=0 Radius=40
  constraints (5):
    c: PointOnObject(g0,g-2)
    c: Coincident(g1,g0)
    c: DistanceY(g0) = -270
    c: Diameter(g0) = 60
    c: Diameter(g1) = 80
FEATURE [Part::Extrusion] Extrude176  label="domeHolds006"
  Base = -> Sketch241
  Dir = (0,0,1)
  DirMode = 2
  FaceMakerClass = Part::FaceMakerBullseye
  FaceMakerMode = 3
  LengthFwd = 48
  LengthRev = 0
  Placement = pos=(-80,0,0) rot=(0,0,1;0rad)
  Solid = true
  Symmetric = false
FEATURE [Part::MultiFuse] Fusion257  label="domeHolds007"
  Shapes = -> [Extrude174,Extrude175,Extrude176]
FEATURE [Part::MultiFuse] Fusion258  label="mainLightModule007"
  Shapes = -> [Fillet014,Fillet013,Fusion257,Extrude134]
FEATURE [Part::Fillet] Fillet015  label="mainLightModule006"
  Base = -> Fusion258
  EdgeLinks = -> Fusion258 [Edge124,Edge127,Edge206,Edge218,Edge219,Edge220,Edge265,Edge268,Edge277,Edge279,Edge280,Edge281,Edge295,Edge297,Edge301,Edge302,Edge303]
  Edges = 17 edges r=4: [Edge124,Edge127,Edge206,Edge218,Edge219,Edge220,Edge265,Edge268,Edge277,Edge279,Edge280,Edge281,Edge295,Edge297,Edge301,Edge302,Edge303]
FEATURE [Part::Cut] Cut084  label="mainLightModule005"
  Base = -> Fillet015
  Tool = -> Extrude172
FEATURE [Part::MultiFuse] Fusion259  label="mainLightModule008"
  Shapes = -> [Cut084,Extrude135,Extrude136]
FEATURE [Part::Cut] Cut085  label="mainLightModule"
  Base = -> Fusion259
  Tool = -> Fusion260
FEATURE [Part::MultiFuse] Fusion261  label="mainLightModule009"
  Shapes = -> [Extrude129,Cut085,Fillet006]
FEATURE [Part::Fillet] Fillet016
  Base = -> Fusion261
  EdgeLinks = -> Fusion261 [Edge277,Edge279,Edge489,Edge491]
  Edges = 4 edges r=4: [Edge277,Edge279,Edge489,Edge491]
FEATURE [Part::Fillet] Fillet017  label="mainLightModule010"
  Base = -> Fillet016
  EdgeLinks = -> Fillet016 [Edge555,Edge744,Edge745,Edge897,Edge898,Edge1054]
  Edges = 6 edges r=1: [Edge555,Edge744,Edge745,Edge897,Edge898,Edge1054]
FEATURE [Part::Sphere] Sphere011  label="Sphere_out005"
  Angle1 = -90
  Angle2 = 90
  Angle3 = 180
  AttacherType = Attacher::AttachEngine3D
  Placement = pos=(0,0,0) rot=(1,0,0;1.5708rad)
  Radius = 30
FEATURE [Part::Sphere] Sphere012  label="Sphere_in005"
  Angle1 = -90
  Angle2 = 90
  Angle3 = 180
  AttacherType = Attacher::AttachEngine3D
  Placement = pos=(0,0,0) rot=(1,0,0;1.5708rad)
  Radius = 28.7
FEATURE [Part::Cut] Cut065  label="Dome005"
  Base = -> Sphere011
  Tool = -> Sphere012
FEATURE [Part::MultiFuse] Fusion179  label="dome"
  Shapes = -> [Cut065,Cut066]
FEATURE [Part::Cut] Cut067  label="dome001"
  Base = -> Fusion179
  Placement = pos=(0,-270,30.5) rot=(0,0,1;0rad)
  Tool = -> Extrude091
FEATURE [Part::Sphere] Sphere013  label="Sphere_out006"
  Angle1 = -90
  Angle2 = 90
  Angle3 = 180
  AttacherType = Attacher::AttachEngine3D
  Placement = pos=(0,0,0) rot=(1,0,0;1.5708rad)
  Radius = 30
FEATURE [Part::Sphere] Sphere014  label="Sphere_in006"
  Angle1 = -90
  Angle2 = 90
  Angle3 = 180
  AttacherType = Attacher::AttachEngine3D
  Placement = pos=(0,0,0) rot=(1,0,0;1.5708rad)
  Radius = 28.7
FEATURE [Part::Cut] Cut068  label="Dome006"
  Base = -> Sphere013
  Tool = -> Sphere014
FEATURE [Part::MultiFuse] Fusion187  label="dome003"
  Shapes = -> [Cut068,Cut069]
FEATURE [Part::Cut] Cut070  label="dome002"
  Base = -> Fusion187
  Placement = pos=(-80,-270,30.5) rot=(0,0,1;0rad)
  Tool = -> Extrude092
FEATURE [Part::Sphere] Sphere015  label="Sphere_out007"
  Angle1 = -90
  Angle2 = 90
  Angle3 = 180
  AttacherType = Attacher::AttachEngine3D
  Placement = pos=(0,0,0) rot=(1,0,0;1.5708rad)
  Radius = 30
FEATURE [Part::Sphere] Sphere016  label="Sphere_in007"
  Angle1 = -90
  Angle2 = 90
  Angle3 = 180
  AttacherType = Attacher::AttachEngine3D
  Placement = pos=(0,0,0) rot=(1,0,0;1.5708rad)
  Radius = 28.7
FEATURE [Part::Cut] Cut071  label="Dome007"
  Base = -> Sphere015
  Tool = -> Sphere016
FEATURE [Part::MultiFuse] Fusion188  label="dome005"
  Shapes = -> [Cut071,Cut072]
FEATURE [Part::Cut] Cut073  label="dome004"
  Base = -> Fusion188
  Placement = pos=(80,-270,30.5) rot=(0,0,1;0rad)
  Tool = -> Extrude093
FEATURE [Part::Compound] Compound002  label="domesAndSeals"
  Links = -> [Cut067,Cut070,Cut073,Extrude094,Extrude095,Extrude096]
FEATURE [App::Part] sot_23_6_v003  label="sot-23-6 v003"
  Group = -> [Part__Feature340,Part__Feature341,Part__Feature342,Part__Feature343,Part__Feature344,Part__Feature345,Part__Feature346]
  Origin = -> Origin010
  Placement = pos=(-4.47945,-0.603742,1.69152) rot=(0,0,1;0rad)
FEATURE [App::Part] Adafruit_AS7341_STEMMA_QT_v003  label="ltr391"
  Group = -> [Part__Feature333,Part__Feature334,Part__Feature335,Part__Feature336,Part__Feature337,Part__Feature338,Part__Feature339,sot_23_6_v003,Part__Feature347,Part__Feature348,Part__Feature349,Part__Feature350,Part__Feature351,Part__Feature352,Part__Feature353]
  Origin = -> Origin011
  Placement = pos=(80,-274.25,28) rot=(0,0,1;0rad)
FEATURE [Part::Compound] Compound001  label="setItems"
  Links = -> [Part__Feature354,Cut147,Adafruit_AS7341_STEMMA_QT_v003,Clone002,Compound002,Extrude097,Adafruit_INA219_STEMMA_QT_v7,PG7_Gland1,PG7_Gland002]
FEATURE [Part::Box] Box071  label="guva004"
  AttacherType = Attacher::AttachEngine3D
  Height = 2
  Length = 19
  Placement = pos=(-9.5,-88,0) rot=(0,0,1;0rad)
  Width = 10
FEATURE [Part::FeaturePython] Clone053  label="tSlotTop002"  # WARN: FeaturePython — macro-defined, semantics opaque (R4)
  AttacherType = Attacher::AttachEngine3D
  Fuse = false
  Placement = pos=(0,0,-7) rot=(1,0,0;1.5708rad)
  Scale = (1,1,3)
FEATURE [Part::FeaturePython] Clone054  label="M3Nut076"  # WARN: FeaturePython — macro-defined, semantics opaque (R4)
  AttacherType = Attacher::AttachEngine3D
  Fuse = false
  Placement = pos=(0,0,4.5) rot=(0,0,1;0rad)
  Scale = (1.1,1.1,5)
FEATURE [Part::FeaturePython] Clone055  label="M3Nut077"  # WARN: FeaturePython — macro-defined, semantics opaque (R4)
  AttacherType = Attacher::AttachEngine3D
  Fuse = false
  Placement = pos=(0,0,0.9) rot=(0,0,1;0rad)
  Scale = (1.1,1.1,1)
FEATURE [Part::FeaturePython] Clone056  label="M3Nut078"  # WARN: FeaturePython — macro-defined, semantics opaque (R4)
  AttacherType = Attacher::AttachEngine3D
  Fuse = false
  Placement = pos=(0,0,4.5) rot=(0,0,1;0rad)
  Scale = (1.1,1.1,5)
FEATURE [Part::FeaturePython] Clone057  label="M3Nut079"  # WARN: FeaturePython — macro-defined, semantics opaque (R4)
  AttacherType = Attacher::AttachEngine3D
  Fuse = false
  Placement = pos=(0,0,0.9) rot=(0,0,1;0rad)
  Scale = (1.1,1.1,1)
FEATURE [Part::FeaturePython] Clone058  label="M3Nut080"  # WARN: FeaturePython — macro-defined, semantics opaque (R4)
  AttacherType = Attacher::AttachEngine3D
  Fuse = false
  Placement = pos=(0,0,4.5) rot=(0,0,1;0rad)
  Scale = (1.1,1.1,5)
FEATURE [Part::FeaturePython] Clone059  label="M3Nut081"  # WARN: FeaturePython — macro-defined, semantics opaque (R4)
  AttacherType = Attacher::AttachEngine3D
  Fuse = false
  Placement = pos=(0,0,0.9) rot=(0,0,1;0rad)
  Scale = (1.1,1.1,1)
FEATURE [Part::FeaturePython] Clone060  label="M3Nut082"  # WARN: FeaturePython — macro-defined, semantics opaque (R4)
  AttacherType = Attacher::AttachEngine3D
  Fuse = false
  Placement = pos=(0,0,4.5) rot=(0,0,1;0rad)
  Scale = (1.1,1.1,5)
FEATURE [Part::FeaturePython] Clone061  label="M3Nut083"  # WARN: FeaturePython — macro-defined, semantics opaque (R4)
  AttacherType = Attacher::AttachEngine3D
  Fuse = false
  Placement = pos=(0,0,0.9) rot=(0,0,1;0rad)
  Scale = (1.1,1.1,1)
FEATURE [Part::FeaturePython] Clone062  label="M3Nut084"  # WARN: FeaturePython — macro-defined, semantics opaque (R4)
  AttacherType = Attacher::AttachEngine3D
  Fuse = false
  Placement = pos=(0,0,4.5) rot=(0,0,1;0rad)
  Scale = (1.1,1.1,5)
FEATURE [Part::FeaturePython] Clone063  label="M3Nut085"  # WARN: FeaturePython — macro-defined, semantics opaque (R4)
  AttacherType = Attacher::AttachEngine3D
  Fuse = false
  Placement = pos=(0,0,0.9) rot=(0,0,1;0rad)
  Scale = (1.1,1.1,1)
FEATURE [Part::FeaturePython] Clone064  label="M3Nut086"  # WARN: FeaturePython — macro-defined, semantics opaque (R4)
  AttacherType = Attacher::AttachEngine3D
  Fuse = false
  Placement = pos=(0,0,4.5) rot=(0,0,1;0rad)
  Scale = (1.1,1.1,5)
FEATURE [Part::FeaturePython] Clone065  label="M3Nut087"  # WARN: FeaturePython — macro-defined, semantics opaque (R4)
  AttacherType = Attacher::AttachEngine3D
  Fuse = false
  Placement = pos=(0,0,0.9) rot=(0,0,1;0rad)
  Scale = (1.1,1.1,1)
FEATURE [Part::FeaturePython] Clone066  label="M3Nut088"  # WARN: FeaturePython — macro-defined, semantics opaque (R4)
  AttacherType = Attacher::AttachEngine3D
  Fuse = false
  Placement = pos=(0,0,4.5) rot=(0,0,1;0rad)
  Scale = (1.1,1.1,5)
FEATURE [Part::FeaturePython] Clone067  label="M3Nut089"  # WARN: FeaturePython — macro-defined, semantics opaque (R4)
  AttacherType = Attacher::AttachEngine3D
  Fuse = false
  Placement = pos=(0,0,0.9) rot=(0,0,1;0rad)
  Scale = (1.1,1.1,1)
FEATURE [Part::FeaturePython] Clone068  label="M3Nut090"  # WARN: FeaturePython — macro-defined, semantics opaque (R4)
  AttacherType = Attacher::AttachEngine3D
  Fuse = false
  Placement = pos=(0,0,4.5) rot=(0,0,1;0rad)
  Scale = (1.1,1.1,5)
FEATURE [Part::FeaturePython] Clone069  label="M3Nut091"  # WARN: FeaturePython — macro-defined, semantics opaque (R4)
  AttacherType = Attacher::AttachEngine3D
  Fuse = false
  Placement = pos=(0,0,0.9) rot=(0,0,1;0rad)
  Scale = (1.1,1.1,1)
FEATURE [Part::FeaturePython] Clone070  label="M3Nut092"  # WARN: FeaturePython — macro-defined, semantics opaque (R4)
  AttacherType = Attacher::AttachEngine3D
  Fuse = false
  Placement = pos=(0,0,4.5) rot=(0,0,1;0rad)
  Scale = (1.1,1.1,5)
FEATURE [Part::FeaturePython] Clone071  label="M3Nut093"  # WARN: FeaturePython — macro-defined, semantics opaque (R4)
  AttacherType = Attacher::AttachEngine3D
  Fuse = false
  Placement = pos=(0,0,0.9) rot=(0,0,1;0rad)
  Scale = (1.1,1.1,1)
FEATURE [Part::FeaturePython] Clone072  label="M3Nut094"  # WARN: FeaturePython — macro-defined, semantics opaque (R4)
  AttacherType = Attacher::AttachEngine3D
  Fuse = false
  Placement = pos=(0,0,4.5) rot=(0,0,1;0rad)
  Scale = (1.1,1.1,5)
FEATURE [Part::FeaturePython] Clone073  label="M3Nut095"  # WARN: FeaturePython — macro-defined, semantics opaque (R4)
  AttacherType = Attacher::AttachEngine3D
  Fuse = false
  Placement = pos=(0,0,0.9) rot=(0,0,1;0rad)
  Scale = (1.1,1.1,1)
FEATURE [Part::FeaturePython] Clone074  label="M3Nut096"  # WARN: FeaturePython — macro-defined, semantics opaque (R4)
  AttacherType = Attacher::AttachEngine3D
  Fuse = false
  Placement = pos=(0,0,4.5) rot=(0,0,1;0rad)
  Scale = (1.1,1.1,5)
FEATURE [Part::FeaturePython] Clone075  label="M3Nut097"  # WARN: FeaturePython — macro-defined, semantics opaque (R4)
  AttacherType = Attacher::AttachEngine3D
  Fuse = false
  Placement = pos=(0,0,0.9) rot=(0,0,1;0rad)
  Scale = (1.1,1.1,1)
FEATURE [Part::FeaturePython] Clone076  label="M3Nut098"  # WARN: FeaturePython — macro-defined, semantics opaque (R4)
  AttacherType = Attacher::AttachEngine3D
  Fuse = false
  Placement = pos=(0,0,4.5) rot=(0,0,1;0rad)
  Scale = (1.1,1.1,5)
FEATURE [Part::FeaturePython] Clone077  label="M3Nut099"  # WARN: FeaturePython — macro-defined, semantics opaque (R4)
  AttacherType = Attacher::AttachEngine3D
  Fuse = false
  Placement = pos=(0,0,0.9) rot=(0,0,1;0rad)
  Scale = (1.1,1.1,1)
FEATURE [Part::FeaturePython] Clone078  label="M3Nut100"  # WARN: FeaturePython — macro-defined, semantics opaque (R4)
  AttacherType = Attacher::AttachEngine3D
  Fuse = false
  Placement = pos=(0,0,4.5) rot=(0,0,1;0rad)
  Scale = (1.1,1.1,5)
FEATURE [Part::FeaturePython] Clone079  label="M3Nut101"  # WARN: FeaturePython — macro-defined, semantics opaque (R4)
  AttacherType = Attacher::AttachEngine3D
  Fuse = false
  Placement = pos=(0,0,0.9) rot=(0,0,1;0rad)
  Scale = (1.1,1.1,1)
FEATURE [Part::Cylinder] Cylinder200
  Angle = 360
  AttacherType = Attacher::AttachEngine3D
  FirstAngle = 0
  Height = 10
  Placement = pos=(6.5,-83,0) rot=(0,0,1;0rad)
  Radius = 1.13
  SecondAngle = 0
FEATURE [Part::Cut] Cut148  label="guva005"
  Base = -> Box071
  Placement = pos=(80,-176.25,28) rot=(0,0,1;0rad)
  Tool = -> Cylinder200
FEATURE [Part::Cylinder] Cylinder201
  Angle = 360
  AttacherType = Attacher::AttachEngine3D
  FirstAngle = 0
  Height = 2.6
  Radius = 40
  SecondAngle = 0
FEATURE [Part::Cylinder] Cylinder202  label="Cylinder_in008"
  Angle = 360
  AttacherType = Attacher::AttachEngine3D
  FirstAngle = 0
  Height = 2.6
  Radius = 30
  SecondAngle = 0
FEATURE [Part::Cut] Cut150  label="Base_flat008"
  Base = -> Cylinder201
  Tool = -> Cylinder202
FEATURE [Part::Cylinder] Cylinder203
  Angle = 360
  AttacherType = Attacher::AttachEngine3D
  FirstAngle = 0
  Height = 2.6
  Radius = 40
  SecondAngle = 0
FEATURE [Part::Cylinder] Cylinder204  label="Cylinder_in009"
  Angle = 360
  AttacherType = Attacher::AttachEngine3D
  FirstAngle = 0
  Height = 2.6
  Radius = 30
  SecondAngle = 0
FEATURE [Part::Cut] Cut153  label="Base_flat009"
  Base = -> Cylinder203
  Tool = -> Cylinder204
FEATURE [Part::Cylinder] Cylinder205
  Angle = 360
  AttacherType = Attacher::AttachEngine3D
  FirstAngle = 0
  Height = 2.6
  Radius = 40
  SecondAngle = 0
FEATURE [Part::Cylinder] Cylinder206  label="Cylinder_in010"
  Angle = 360
  AttacherType = Attacher::AttachEngine3D
  FirstAngle = 0
  Height = 2.6
  Radius = 30
  SecondAngle = 0
FEATURE [Part::Cut] Cut156  label="Base_flat010"
  Base = -> Cylinder205
  Tool = -> Cylinder206
FEATURE [Part::Cylinder] Cylinder207 .. Cylinder219  x13 (patterned run collapsed; names and placements below)
  Angle = 360
  AttacherType = Attacher::AttachEngine3D
  FirstAngle = 0
  Height = 9
  Radius = 2
  SecondAngle = 0
FEATURE [Part::MultiFuse] Fusion265
  Shapes = -> [Clone054,Cylinder207]
FEATURE [Part::MultiFuse] Fusion266  label="m3NutCut027"
  Placement = pos=(-80,-235,-22.5) rot=(0.707107,-0.707107,0;3.14159rad)
  Shapes = -> [Clone055,Fusion265]
FEATURE [Part::MultiFuse] Fusion267
  Shapes = -> [Clone056,Cylinder208]
FEATURE [Part::MultiFuse] Fusion268  label="m3NutCut028"
  Placement = pos=(-115,-270,-22.5) rot=(1,0,0;3.14159rad)
  Shapes = -> [Clone057,Fusion267]
FEATURE [Part::MultiFuse] Fusion269
  Shapes = -> [Clone058,Cylinder209]
FEATURE [Part::MultiFuse] Fusion270  label="m3NutCut029"
  Placement = pos=(-45,-270,-22.5) rot=(1,0,0;3.14159rad)
  Shapes = -> [Clone059,Fusion269]
FEATURE [Part::MultiFuse] Fusion271
  Shapes = -> [Clone060,Cylinder210]
FEATURE [Part::MultiFuse] Fusion272  label="m3NutCut030"
  Placement = pos=(-35,-270,-22.5) rot=(1,0,0;3.14159rad)
  Shapes = -> [Clone061,Fusion271]
FEATURE [Part::MultiFuse] Fusion273
  Shapes = -> [Clone062,Cylinder211]
FEATURE [Part::MultiFuse] Fusion274  label="m3NutCut031"
  Placement = pos=(35,-270,-22.5) rot=(1,0,0;3.14159rad)
  Shapes = -> [Clone063,Fusion273]
FEATURE [Part::MultiFuse] Fusion275
  Shapes = -> [Clone064,Cylinder212]
FEATURE [Part::MultiFuse] Fusion276  label="m3NutCut032"
  Placement = pos=(45,-270,-22.5) rot=(1,0,0;3.14159rad)
  Shapes = -> [Clone065,Fusion275]
FEATURE [Part::MultiFuse] Fusion277
  Shapes = -> [Clone066,Cylinder213]
FEATURE [Part::MultiFuse] Fusion278  label="m3NutCut033"
  Placement = pos=(115,-270,-22.5) rot=(1,0,0;3.14159rad)
  Shapes = -> [Clone067,Fusion277]
FEATURE [Part::MultiFuse] Fusion279
  Shapes = -> [Clone068,Cylinder214]
FEATURE [Part::MultiFuse] Fusion280  label="m3NutCut034"
  Placement = pos=(-80,-235,-22.5) rot=(0.707107,-0.707107,0;3.14159rad)
  Shapes = -> [Clone069,Fusion279]
FEATURE [Part::MultiFuse] Fusion281
  Shapes = -> [Clone070,Cylinder215]
FEATURE [Part::MultiFuse] Fusion282  label="m3NutCut035"
  Placement = pos=(0,-235,-22.5) rot=(0.707107,-0.707107,0;3.14159rad)
  Shapes = -> [Clone071,Fusion281]
FEATURE [Part::MultiFuse] Fusion283
  Shapes = -> [Clone072,Cylinder216]
FEATURE [Part::MultiFuse] Fusion284  label="m3NutCut036"
  Placement = pos=(80,-235,-22.5) rot=(0.707107,-0.707107,0;3.14159rad)
  Shapes = -> [Clone073,Fusion283]
FEATURE [Part::MultiFuse] Fusion285
  Shapes = -> [Clone074,Cylinder217]
FEATURE [Part::MultiFuse] Fusion286  label="m3NutCut037"
  Placement = pos=(80,-305,-22.5) rot=(0.707107,-0.707107,0;3.14159rad)
  Shapes = -> [Clone075,Fusion285]
FEATURE [Part::MultiFuse] Fusion287
  Shapes = -> [Clone076,Cylinder218]
FEATURE [Part::MultiFuse] Fusion288  label="m3NutCut038"
  Placement = pos=(1.4e-14,-305,-22.5) rot=(0.707107,-0.707107,0;3.14159rad)
  Shapes = -> [Clone077,Fusion287]
FEATURE [Part::MultiFuse] Fusion289
  Shapes = -> [Clone078,Cylinder219]
FEATURE [Part::MultiFuse] Fusion290  label="m3NutCut039"
  Placement = pos=(-80,-305,-22.5) rot=(0.707107,-0.707107,0;3.14159rad)
  Shapes = -> [Clone079,Fusion289]
FEATURE [Part::MultiFuse] Fusion291  label="m3NutCuts001"
  Placement = pos=(0,0,-0.5) rot=(0,0,1;0rad)
  Shapes = -> [Fusion266,Fusion268,Fusion270,Fusion272,Fusion274,Fusion276,Fusion278,Fusion280,Fusion282,Fusion284,Fusion286,Fusion288,Fusion290]
FEATURE [Part::Feature] Part__Feature373  label="Printed Circuit Board003"
  shape: bbox 25.4 x 20.32 x 1.65 mm, 39 faces (baked)
FEATURE [Part::Feature] Part__Feature374  label="Printed Circuit Board004"
  shape: bbox 25.4 x 17.78 x 1.6 mm, 42 faces (baked)
FEATURE [Part::Feature] Part__Feature375  label="EAHC2835WD008"
  shape: bbox 3.513 x 2.813 x 0.7485 mm, 108 faces, 4 solids (baked)
FEATURE [Part::Feature] Part__Feature376  label="AS7341 v004"
  Placement = pos=(0,-0.339822,1.6) rot=(0,0,1;0rad)
  shape: bbox 2 x 3.1 x 1.1 mm, 267 faces, 26 solids (baked)
FEATURE [Part::Feature] Part__Feature377  label="CAPC-0805-T0.95-BN v008"
  Placement = pos=(-5.01759,-3.15294,1.6) rot=(0,0,1;0rad)
  shape: bbox 2.1 x 1.35 x 0.95 mm, 42 faces (baked)
FEATURE [Part::Feature] Part__Feature378  label="CAPC-0805-T0.95-BN v009"
  Placement = pos=(-5.48627,2.66154,1.6) rot=(0,0,-1;1.5708rad)
  shape: bbox 1.35 x 2.1 x 0.95 mm, 42 faces (baked)
FEATURE [Part::Feature] Part__Feature379  label="CAPC-0805-T0.95-BN v010"
  Placement = pos=(-3.43627,2.66154,1.6) rot=(0,0,-1;1.5708rad)
  shape: bbox 1.35 x 2.1 x 0.95 mm, 42 faces (baked)
FEATURE [Part::Feature] Part__Feature380  label="CAPC-0603-T0.9-BN v004"
  Placement = pos=(-1.69987,-3.28475,1.6) rot=(0,0,1;0rad)
  shape: bbox 1.7 x 0.9 x 0.9 mm, 42 faces (baked)
FEATURE [Part::Feature] Part__Feature381  label="BODY_MF06A002"
  Placement = pos=(0,0,0.762) rot=(0.57735,-0.57735,-0.57735;2.0944rad)
  shape: bbox 1.601 x 2.921 x 1.016 mm, 42 faces (baked)
FEATURE [Part::Feature] Part__Feature382  label="LEAD_MF06A012"
  Placement = pos=(-0.9652,-0.9525,0.1016) rot=(0.57735,-0.57735,-0.57735;2.0944rad)
  shape: bbox 0.6223 x 0.3749 x 0.8636 mm, 14 faces (baked)
FEATURE [Part::Feature] Part__Feature383  label="LEAD_MF06A013"
  Placement = pos=(-0.9652,0,0.1016) rot=(0.57735,-0.57735,-0.57735;2.0944rad)
  shape: bbox 0.6223 x 0.3749 x 0.8636 mm, 14 faces (baked)
FEATURE [Part::Feature] Part__Feature384  label="LEAD_MF06A014"
  Placement = pos=(-0.9652,0.9525,0.1016) rot=(0.57735,-0.57735,-0.57735;2.0944rad)
  shape: bbox 0.6223 x 0.3749 x 0.8636 mm, 14 faces (baked)
FEATURE [Part::Feature] Part__Feature385  label="LEAD_MF06A015"
  Placement = pos=(0.9652,-0.9525,0.1016) rot=(0.57735,0.57735,0.57735;2.0944rad)
  shape: bbox 0.6223 x 0.3749 x 0.8636 mm, 14 faces (baked)
FEATURE [Part::Feature] Part__Feature386  label="LEAD_MF06A016"
  Placement = pos=(0.9652,0,0.1016) rot=(0.57735,0.57735,0.57735;2.0944rad)
  shape: bbox 0.6223 x 0.3749 x 0.8636 mm, 14 faces (baked)
FEATURE [Part::Feature] Part__Feature387  label="LEAD_MF06A017"
  Placement = pos=(0.9652,0.9525,0.1016) rot=(0.57735,0.57735,0.57735;2.0944rad)
  shape: bbox 0.6223 x 0.3749 x 0.8636 mm, 14 faces (baked)
FEATURE [Part::Feature] Part__Feature388  label="SOT363 v004"
  Placement = pos=(4.97054,-0.645171,1.675) rot=(0,0,1;3.14159rad)
  shape: bbox 2.1 x 2 x 1.1 mm, 94 faces, 7 solids (baked)
FEATURE [Part::Feature] Part__Feature389  label="LED 0603 single color v004"
  Placement = pos=(-9.18406,3.72778,1.60762) rot=(0,0,1;1.5708rad)
  shape: bbox 1.961 x 0.7932 x 0.7145 mm, 63 faces, 5 solids (baked)
FEATURE [Part::Feature] Part__Feature390  label="RESC-0603 v006"
  Placement = pos=(4.83432,-3.67461,1.6) rot=(0,0,1;0rad)
  shape: bbox 1.7 x 0.9 x 0.55 mm, 52 faces, 3 solids (baked)
FEATURE [Part::Feature] Part__Feature391  label="RESC-0603 v007"
  Placement = pos=(-7.14949,3.61248,1.6) rot=(0,0,-1;1.5708rad)
  shape: bbox 0.9 x 1.7 x 0.55 mm, 52 faces, 3 solids (baked)
FEATURE [Part::Feature] Part__Feature392  label="YC164_RESPACK v004"
  Placement = pos=(2.99591,1.52916,1.6) rot=(0,0,1;0rad)
  shape: bbox 3.2 x 1.6 x 0.61 mm, 172 faces (baked)
FEATURE [Part::Feature] Part__Feature393  label="qwicc v007"
  Placement = pos=(-10.8364,0.0607456,1.65) rot=(0,0,-1;1.5708rad)
  shape: bbox 4.95 x 6 x 2.96 mm, 229 faces, 7 solids (baked)
FEATURE [Part::Feature] Part__Feature394  label="qwicc v008"
  Placement = pos=(10.8256,0.00556102,1.65) rot=(0,0,1;1.5708rad)
  shape: bbox 4.95 x 6 x 2.96 mm, 229 faces, 7 solids (baked)
FEATURE [Part::Feature] Part__Feature395  label="elpCamera002"
  Placement = pos=(0,-270,13) rot=(0,0,1;0rad)
  shape: bbox 38 x 38 x 25.12 mm, 164 faces (baked)
FEATURE [Part::Feature] Part__Feature396  label="RESC-2512-R100 v003"
  Placement = pos=(0.0152473,1.04463,1.65) rot=(0,0,1;3.14159rad)
  shape: bbox 6.417 x 3.317 x 0.6674 mm, 219 faces, 7 solids (baked)
FEATURE [Part::Feature] Part__Feature397  label="LED 0603 single color v005"
  Placement = pos=(-9.06678,4.19381,1.65762) rot=(0,0,1;1.5708rad)
  shape: bbox 1.961 x 0.7932 x 0.7145 mm, 63 faces, 5 solids (baked)
FEATURE [Part::Feature] Part__Feature398  label="CAPC-0805-T0.95-BN v011"
  Placement = pos=(-4.32049,-3.03839,1.65) rot=(0,0,-1;1.5708rad)
  shape: bbox 1.35 x 2.1 x 0.95 mm, 42 faces (baked)
FEATURE [Part::Feature] Part__Feature399  label="CAPC-0603-T0.9-BN v005"
  Placement = pos=(-2.53733,-2.97022,1.65) rot=(0,0,-1;1.5708rad)
  shape: bbox 0.9 x 1.7 x 0.9 mm, 42 faces (baked)
FEATURE [Part::Feature] Part__Feature400  label="RESC-0603 v008"
  Placement = pos=(-7.09227,3.55774,1.65) rot=(0,0,-1;1.5708rad)
  shape: bbox 0.9 x 1.7 x 0.55 mm, 52 faces, 3 solids (baked)
FEATURE [Part::Feature] Part__Feature401  label="YC164_RESPACK v005"
  Placement = pos=(2.74348,-1.41846,1.65) rot=(0,0,-1;1.5708rad)
  shape: bbox 1.6 x 3.2 x 0.61 mm, 172 faces (baked)
FEATURE [Part::Feature] Part__Feature402  label="qwicc v009"
  Placement = pos=(-8.57299,-0.000230516,1.345) rot=(0.57735,-0.57735,-0.57735;2.0944rad)
  shape: bbox 4.95 x 6 x 2.96 mm, 229 faces, 7 solids (baked)
FEATURE [Part::Feature] Part__Feature403  label="qwicc v010"
  Placement = pos=(8.61502,0.00281866,1.345) rot=(0.57735,0.57735,0.57735;2.0944rad)
  shape: bbox 4.95 x 6 x 2.96 mm, 229 faces, 7 solids (baked)
FEATURE [Part::Feature] Part__Feature404  label="B219 v003"
  Placement = pos=(0.00220704,-3.21564,1.62965) rot=(0,0,1;3.14159rad)
  shape: bbox 3.008 x 2.843 x 1.194 mm, 338 faces, 14 solids (baked)
FEATURE [Part::Feature] Part__Feature405  label="Screw Terminal 2pin 3.5mm Pitch v012"
  Placement = pos=(0.115254,6.14583,1.45) rot=(0,0,1;3.14159rad)
  shape: bbox 11.43 x 7.244 x 12 mm, 100 faces, 3 solids (baked)
FEATURE [App::Part] Adafruit_INA219_STEMMA_QT_v008  label="ina220"
  Group = -> [Part__Feature373,Part__Feature396,Part__Feature397,Part__Feature398,Part__Feature399,Part__Feature400,Part__Feature401,Part__Feature402,Part__Feature403,Part__Feature404,Part__Feature405]
  Origin = -> Origin014
  Placement = pos=(58,-270,9) rot=(0,-1,0;4.71239rad)
FEATURE [Part::Feature] Part__Feature406  label="Body008"
  shape: bbox 15.5 x 16.75 x 29 mm, 21 faces (baked)
FEATURE [Part::Feature] Part__Feature407  label="Body009"
  Placement = pos=(0,0,2) rot=(0,0,1;0rad)
  shape: bbox 17.44 x 17.44 x 14.25 mm, 14 faces (baked)
FEATURE [Part::Feature] Part__Feature408  label="Body010"
  Placement = pos=(0,0,-2.9) rot=(0,0,1;0rad)
  shape: bbox 19 x 19 x 4.75 mm, 25 faces (baked)
FEATURE [Part::Feature] Part__Feature409  label="Body011"
  shape: bbox 16.75 x 16.75 x 0.9 mm, 4 faces (baked)
FEATURE [App::Part] PG7_Gland004
  Group = -> [Part__Feature406,Part__Feature407,Part__Feature408,Part__Feature409]
  Origin = -> Origin017
  Placement = pos=(72,-256,-26) rot=(0,-1,0;3.14159rad)
FEATURE [Part::Feature] Part__Feature410  label="Body012"
  shape: bbox 15.5 x 16.75 x 29 mm, 21 faces (baked)
FEATURE [Part::Feature] Part__Feature411  label="Body013"
  Placement = pos=(0,0,2) rot=(0,0,1;0rad)
  shape: bbox 17.44 x 17.44 x 14.25 mm, 14 faces (baked)
FEATURE [Part::Feature] Part__Feature412  label="Body014"
  Placement = pos=(0,0,-2.9) rot=(0,0,1;0rad)
  shape: bbox 19 x 19 x 4.75 mm, 25 faces (baked)
FEATURE [Part::Feature] Part__Feature413  label="Body015"
  shape: bbox 16.75 x 16.75 x 0.9 mm, 4 faces (baked)
FEATURE [App::Part] PG7_Gland003
  Group = -> [Part__Feature410,Part__Feature411,Part__Feature412,Part__Feature413]
  Origin = -> Origin018
  Placement = pos=(0,-256,-26) rot=(0,-1,0;3.14159rad)
FEATURE [Part::Part2DObjectPython] ShapeString002  # Draft 2D object (typed FeaturePython)
  FontFile = <userpath>/gitHubRepos/3DMints2024/msclns/fonts/montserrat/Montserrat-Regular.otf
  Fuse = false
  Justification = 6
  JustificationReference = 0
  KeepLeftMargin = false
  MakeFace = true
  ObliqueAngle = 0
  Placement = pos=(-15.5,-310,-21) rot=(1,0,0;1.5708rad)
  ScaleToSize = true
  Size = 15
  String = MINTS-AI
  Tracking = 0
FEATURE [Part::Extrusion] Extrude191  label="text001"
  Base = -> ShapeString002
  Dir = (0,-1,2e-16)
  DirMode = 2
  FaceMakerClass = Part::FaceMakerBullseye
  FaceMakerMode = 3
  LengthFwd = 2
  LengthRev = 0
  Solid = false
  Symmetric = false
FEATURE [Sketcher::SketchObject] Sketch402
  ArcFitTolerance = 0
  FullyConstrained = true
  MakeInternals = false
  Placement = pos=(0,0,27.5) rot=(0,0,1;0rad)
  sketch-geometry (2):
    g0: Circle CenterX=0 CenterY=-270 CenterZ=0 NormalX=0 NormalY=0 NormalZ=1 AngleXU=0 Radius=37
    g1: Circle CenterX=0 CenterY=-270 CenterZ=0 NormalX=0 NormalY=0 NormalZ=1 AngleXU=0 Radius=26.5
  constraints (5):
    c: Diameter(g0) = 74
    c: Coincident(g1,g0)
    c: Diameter(g1) = 53
    c: DistanceX(g0) = 0
    c: DistanceY(g0) = -270
FEATURE [Part::Extrusion] Extrude180  label="rubberSeals003"
  Base = -> Sketch402
  Dir = (0,0,1)
  DirMode = 2
  FaceMakerClass = Part::FaceMakerBullseye
  FaceMakerMode = 3
  LengthFwd = 3
  LengthRev = 0
  Solid = true
  Symmetric = false
FEATURE [Sketcher::SketchObject] Sketch403
  ArcFitTolerance = 0
  FullyConstrained = true
  MakeInternals = false
  sketch-geometry (4):
    g0: Circle CenterX=0 CenterY=35 CenterZ=0 NormalX=0 NormalY=0 NormalZ=1 AngleXU=0 Radius=1.625
    g1: Circle CenterX=35 CenterY=0 CenterZ=0 NormalX=0 NormalY=0 NormalZ=1 AngleXU=0 Radius=1.625
    g2: Circle CenterX=-35 CenterY=0 CenterZ=0 NormalX=0 NormalY=0 NormalZ=1 AngleXU=0 Radius=1.625
    g3: Circle CenterX=0 CenterY=-35 CenterZ=0 NormalX=0 NormalY=0 NormalZ=1 AngleXU=0 Radius=1.625
  constraints (12):
    c: PointOnObject(g0,g-2)
    c: PointOnObject(g1,g-1)
    c: PointOnObject(g2,g-1)
    c: PointOnObject(g3,g-2)
    c: DistanceY(g3,g-1) = 35
    c: DistanceX(g-1,g1) = 35
    c: DistanceX(g2,g-1) = 35
    c: DistanceY(g-1,g0) = 35
    c: Equal(g1,g3)
    c: Equal(g1,g2)
    c: Equal(g1,g0)
    c: Diameter(g1) = 3.25
FEATURE [Part::Extrusion] Extrude177
  Base = -> Sketch403
  Dir = (0,0,1)
  DirMode = 2
  FaceMakerClass = Part::FaceMakerBullseye
  FaceMakerMode = 3
  LengthFwd = 10
  LengthRev = 0
  Solid = true
  Symmetric = false
FEATURE [Sketcher::SketchObject] Sketch404
  ArcFitTolerance = 0
  FullyConstrained = true
  MakeInternals = false
  sketch-geometry (4):
    g0: Circle CenterX=0 CenterY=35 CenterZ=0 NormalX=0 NormalY=0 NormalZ=1 AngleXU=0 Radius=1.625
    g1: Circle CenterX=35 CenterY=0 CenterZ=0 NormalX=0 NormalY=0 NormalZ=1 AngleXU=0 Radius=1.625
    g2: Circle CenterX=-35 CenterY=0 CenterZ=0 NormalX=0 NormalY=0 NormalZ=1 AngleXU=0 Radius=1.625
    g3: Circle CenterX=0 CenterY=-35 CenterZ=0 NormalX=0 NormalY=0 NormalZ=1 AngleXU=0 Radius=1.625
  constraints (12):
    c: PointOnObject(g0,g-2)
    c: PointOnObject(g1,g-1)
    c: PointOnObject(g2,g-1)
    c: PointOnObject(g3,g-2)
    c: DistanceY(g3,g-1) = 35
    c: DistanceX(g-1,g1) = 35
    c: DistanceX(g2,g-1) = 35
    c: DistanceY(g-1,g0) = 35
    c: Equal(g1,g3)
    c: Equal(g1,g2)
    c: Equal(g1,g0)
    c: Diameter(g1) = 3.25
FEATURE [Part::Extrusion] Extrude178
  Base = -> Sketch404
  Dir = (0,0,1)
  DirMode = 2
  FaceMakerClass = Part::FaceMakerBullseye
  FaceMakerMode = 3
  LengthFwd = 10
  LengthRev = 0
  Solid = true
  Symmetric = false
FEATURE [Sketcher::SketchObject] Sketch405
  ArcFitTolerance = 0
  FullyConstrained = true
  MakeInternals = false
  sketch-geometry (4):
    g0: Circle CenterX=0 CenterY=35 CenterZ=0 NormalX=0 NormalY=0 NormalZ=1 AngleXU=0 Radius=1.625
    g1: Circle CenterX=35 CenterY=0 CenterZ=0 NormalX=0 NormalY=0 NormalZ=1 AngleXU=0 Radius=1.625
    g2: Circle CenterX=-35 CenterY=0 CenterZ=0 NormalX=0 NormalY=0 NormalZ=1 AngleXU=0 Radius=1.625
    g3: Circle CenterX=0 CenterY=-35 CenterZ=0 NormalX=0 NormalY=0 NormalZ=1 AngleXU=0 Radius=1.625
  constraints (12):
    c: PointOnObject(g0,g-2)
    c: PointOnObject(g1,g-1)
    c: PointOnObject(g2,g-1)
    c: PointOnObject(g3,g-2)
    c: DistanceY(g3,g-1) = 35
    c: DistanceX(g-1,g1) = 35
    c: DistanceX(g2,g-1) = 35
    c: DistanceY(g-1,g0) = 35
    c: Equal(g1,g3)
    c: Equal(g1,g2)
    c: Equal(g1,g0)
    c: Diameter(g1) = 3.25
FEATURE [Part::Extrusion] Extrude179
  Base = -> Sketch405
  Dir = (0,0,1)
  DirMode = 2
  FaceMakerClass = Part::FaceMakerBullseye
  FaceMakerMode = 3
  LengthFwd = 10
  LengthRev = 0
  Solid = true
  Symmetric = false
FEATURE [Sketcher::SketchObject] Sketch406
  ArcFitTolerance = 0
  FullyConstrained = true
  MakeInternals = false
  Placement = pos=(0,0,27.5) rot=(0,0,1;0rad)
  sketch-geometry (2):
    g0: Circle CenterX=0 CenterY=-270 CenterZ=0 NormalX=0 NormalY=0 NormalZ=1 AngleXU=0 Radius=37
    g1: Circle CenterX=0 CenterY=-270 CenterZ=0 NormalX=0 NormalY=0 NormalZ=1 AngleXU=0 Radius=26.5
  constraints (5):
    c: Diameter(g0) = 74
    c: Coincident(g1,g0)
    c: Diameter(g1) = 53
    c: DistanceX(g0) = 0
    c: DistanceY(g0) = -270
FEATURE [Part::Extrusion] Extrude181  label="rubberSeals004"
  Base = -> Sketch406
  Dir = (0,0,1)
  DirMode = 2
  FaceMakerClass = Part::FaceMakerBullseye
  FaceMakerMode = 3
  LengthFwd = 3
  LengthRev = 0
  Placement = pos=(-80,0,0) rot=(0,0,1;0rad)
  Solid = true
  Symmetric = false
FEATURE [Sketcher::SketchObject] Sketch407
  ArcFitTolerance = 0
  FullyConstrained = true
  MakeInternals = false
  Placement = pos=(0,0,27.5) rot=(0,0,1;0rad)
  sketch-geometry (2):
    g0: Circle CenterX=0 CenterY=-270 CenterZ=0 NormalX=0 NormalY=0 NormalZ=1 AngleXU=0 Radius=37
    g1: Circle CenterX=0 CenterY=-270 CenterZ=0 NormalX=0 NormalY=0 NormalZ=1 AngleXU=0 Radius=26.5
  constraints (5):
    c: Diameter(g0) = 74
    c: Coincident(g1,g0)
    c: Diameter(g1) = 53
    c: DistanceX(g0) = 0
    c: DistanceY(g0) = -270
FEATURE [Part::Extrusion] Extrude182  label="rubberSeals005"
  Base = -> Sketch407
  Dir = (0,0,1)
  DirMode = 2
  FaceMakerClass = Part::FaceMakerBullseye
  FaceMakerMode = 3
  LengthFwd = 3
  LengthRev = 0
  Placement = pos=(80,0,0) rot=(0,0,1;0rad)
  Solid = true
  Symmetric = false
FEATURE [Sketcher::SketchObject] Sketch408
  ArcFitTolerance = 0
  FullyConstrained = true
  MakeInternals = false
  sketch-geometry (8):
    g0: LineSegment StartX=-98 StartY=-249.5 StartZ=0 EndX=-62 EndY=-249.5 EndZ=0
    g1: LineSegment StartX=-62 StartY=-249.5 StartZ=0 EndX=-62 EndY=-290.5 EndZ=0
    g2: LineSegment StartX=-62 StartY=-290.5 StartZ=0 EndX=-98 EndY=-290.5 EndZ=0
    g3: LineSegment StartX=-98 StartY=-290.5 StartZ=0 EndX=-98 EndY=-249.5 EndZ=0
    g4: Circle CenterX=-90 CenterY=-252.5 CenterZ=0 NormalX=0 NormalY=0 NormalZ=1 AngleXU=0 Radius=1.625
    g5: Circle CenterX=-70 CenterY=-252.5 CenterZ=0 NormalX=0 NormalY=0 NormalZ=1 AngleXU=0 Radius=1.625
    g6: Circle CenterX=-90 CenterY=-287.5 CenterZ=0 NormalX=0 NormalY=0 NormalZ=1 AngleXU=0 Radius=1.625
    g7: Circle CenterX=-70 CenterY=-287.5 CenterZ=0 NormalX=0 NormalY=0 NormalZ=1 AngleXU=0 Radius=1.625
  constraints (24):
    c: Coincident(g0,g1)
    c: Coincident(g1,g2)
    c: Coincident(g2,g3)
    c: Coincident(g3,g0)
    c: Horizontal(g0)
    c: Horizontal(g2)
    c: Vertical(g1)
    c: Vertical(g3)
    c: DistanceY(g2) = -290.5
    c: DistanceY(g2,g0) = 41
    c: Horizontal(g6,g7)
    c: Horizontal(g4,g5)
    c: Vertical(g4,g6)
    c: Vertical(g7,g5)
    c: DistanceY(g6) = -287.5
    c: DistanceY(g6,g4) = 35
    c: DistanceX(g6,g7) = 20
    c: Equal(g5,g7)
    c: Equal(g5,g6)
    c: Equal(g5,g4)
    c: Diameter(g5) = 3.25
    c: DistanceX(g2,g1) = 36
    c: DistanceX(g1) = -62
    c: DistanceX(g7,g1) = 8
FEATURE [Part::Extrusion] Extrude183  label="as7265x002"
  Base = -> Sketch408
  Dir = (0,0,1)
  DirMode = 2
  FaceMakerClass = Part::FaceMakerBullseye
  FaceMakerMode = 3
  LengthFwd = 2
  LengthRev = 0
  Placement = pos=(0,0,28) rot=(0,0,1;0rad)
  Solid = true
  Symmetric = false
FEATURE [Sketcher::SketchObject] Sketch409
  ArcFitTolerance = 0
  FullyConstrained = true
  MakeInternals = false
  Placement = pos=(0,0,-25) rot=(0,0,1;0rad)
  sketch-geometry (12):
    g0: Circle CenterX=-115 CenterY=-270 CenterZ=0 NormalX=0 NormalY=0 NormalZ=1 AngleXU=0 Radius=1.625
    g1: Circle CenterX=-80 CenterY=-235 CenterZ=0 NormalX=0 NormalY=0 NormalZ=1 AngleXU=0 Radius=1.625
    g2: Circle CenterX=-80 CenterY=-305 CenterZ=0 NormalX=0 NormalY=0 NormalZ=1 AngleXU=0 Radius=1.625
    g3: Circle CenterX=-45 CenterY=-270 CenterZ=0 NormalX=0 NormalY=0 NormalZ=1 AngleXU=0 Radius=1.625
    g4: Circle CenterX=-35 CenterY=-270 CenterZ=0 NormalX=0 NormalY=0 NormalZ=1 AngleXU=0 Radius=1.625
    g5: Circle CenterX=0 CenterY=-305 CenterZ=0 NormalX=0 NormalY=0 NormalZ=1 AngleXU=0 Radius=1.625
    g6: Circle CenterX=0 CenterY=-235 CenterZ=0 NormalX=0 NormalY=0 NormalZ=1 AngleXU=0 Radius=1.625
    g7: Circle CenterX=35 CenterY=-270 CenterZ=0 NormalX=0 NormalY=0 NormalZ=1 AngleXU=0 Radius=1.625
    g8: Circle CenterX=45 CenterY=-270 CenterZ=0 NormalX=0 NormalY=0 NormalZ=1 AngleXU=0 Radius=1.625
    g9: Circle CenterX=80 CenterY=-235 CenterZ=0 NormalX=0 NormalY=0 NormalZ=1 AngleXU=0 Radius=1.625
    g10: Circle CenterX=115 CenterY=-270 CenterZ=0 NormalX=0 NormalY=0 NormalZ=1 AngleXU=0 Radius=1.625
    g11: Circle CenterX=80 CenterY=-305 CenterZ=0 NormalX=0 NormalY=0 NormalZ=1 AngleXU=0 Radius=1.625
  constraints (36):
    c: PointOnObject(g5,g-2)
    c: PointOnObject(g6,g-2)
    c: Equal(g8,g1)
    c: Equal(g8,g6)
    c: Equal(g8,g9)
    c: Equal(g8,g2)
    c: Equal(g8,g5)
    c: Equal(g8,g11)
    c: Equal(g8,g0)
    c: Equal(g8,g3)
    c: Equal(g8,g4)
    c: Equal(g8,g7)
    c: Equal(g8,g10)
    c: Diameter(g8) = 3.25
    c: Horizontal(g0,g3)
    c: Horizontal(g3,g4)
    c: Horizontal(g4,g7)
    c: Horizontal(g7,g8)
    c: Horizontal(g8,g10)
    c: Horizontal(g2,g5)
    c: Horizontal(g5,g11)
    c: Horizontal(g6,g9)
    c: Horizontal(g1,g6)
    c: Vertical(g2,g1)
    c: Vertical(g9,g11)
    c: DistanceY(g0) = -270
    c: DistanceX(g0) = -115
    c: DistanceX(g0,g2) = 35
    c: DistanceY(g2,g0) = 35
    c: DistanceY(g0,g1) = 35
    c: DistanceX(g0,g3) = 70
    c: DistanceX(g4) = -35
    c: DistanceX(g7) = 35
    c: DistanceX(g8) = 45
    c: DistanceX(g8,g10) = 70
    c: DistanceX(g8,g11) = 35
FEATURE [Part::Extrusion] Extrude184  label="m3Cuts001"
  Base = -> Sketch409
  Dir = (0,0,1)
  DirMode = 2
  FaceMakerClass = Part::FaceMakerBullseye
  FaceMakerMode = 3
  LengthFwd = 60
  LengthRev = 0
  Solid = true
  Symmetric = false
FEATURE [Sketcher::SketchObject] Sketch410
  ArcFitTolerance = 0
  FullyConstrained = true
  MakeInternals = false
  Placement = pos=(24,0,0) rot=(0.57735,0.57735,0.57735;2.0944rad)
  sketch-geometry (2):
    g0: Circle CenterX=-277.6 CenterY=19.15 CenterZ=0 NormalX=0 NormalY=0 NormalZ=1 AngleXU=0 Radius=1.6
    g1: Circle CenterX=-262.4 CenterY=19.15 CenterZ=0 NormalX=0 NormalY=0 NormalZ=1 AngleXU=0 Radius=1.6
  constraints (6):
    c: Horizontal(g1,g0)
    c: Equal(g1,g0)
    c: Diameter(g1) = 3.2
    c: DistanceX(g0) = -277.6
    c: DistanceY(g0) = 19.15
    c: DistanceX(g0,g1) = 15.2
FEATURE [Part::Extrusion] Extrude185
  Base = -> Sketch410
  Dir = (1,0,0)
  DirMode = 2
  FaceMakerClass = Part::FaceMakerBullseye
  FaceMakerMode = 3
  LengthFwd = 30
  LengthRev = 0
  Solid = true
  Symmetric = false
FEATURE [Sketcher::SketchObject] Sketch411
  ArcFitTolerance = 0
  FullyConstrained = true
  MakeInternals = false
  Placement = pos=(0,0,-22) rot=(0,0,1;0rad)
  sketch-geometry (14):
    g0: LineSegment StartX=-2e-16 StartY=-267 StartZ=0 EndX=9.52628 EndY=-261.5 EndZ=0
    g1: LineSegment StartX=9.52628 StartY=-261.5 StartZ=0 EndX=9.52628 EndY=-250.5 EndZ=0
    g2: LineSegment StartX=9.52628 StartY=-250.5 StartZ=0 EndX=2e-16 EndY=-245 EndZ=0
    g3: LineSegment StartX=0 StartY=-245 StartZ=0 EndX=-9.52628 EndY=-250.5 EndZ=0
    g4: LineSegment StartX=-9.52628 StartY=-250.5 StartZ=0 EndX=-9.52628 EndY=-261.5 EndZ=0
    g5: LineSegment StartX=-9.52628 StartY=-261.5 StartZ=0 EndX=-2e-16 EndY=-267 EndZ=0
    g6: Circle [constr] CenterX=0 CenterY=-256 CenterZ=0 NormalX=0 NormalY=0 NormalZ=1 AngleXU=0 Radius=11
    g7: LineSegment StartX=67 StartY=-267 StartZ=0 EndX=76.5263 EndY=-261.5 EndZ=0
    g8: LineSegment StartX=76.5263 StartY=-261.5 StartZ=0 EndX=76.5263 EndY=-250.5 EndZ=0
    g9: LineSegment StartX=76.5263 StartY=-250.5 StartZ=0 EndX=67 EndY=-245 EndZ=0
    g10: LineSegment StartX=67 StartY=-245 StartZ=0 EndX=57.4737 EndY=-250.5 EndZ=0
    g11: LineSegment StartX=57.4737 StartY=-250.5 StartZ=0 EndX=57.4737 EndY=-261.5 EndZ=0
    g12: LineSegment StartX=57.4737 StartY=-261.5 StartZ=0 EndX=67 EndY=-267 EndZ=0
    g13: Circle [constr] CenterX=67 CenterY=-256 CenterZ=0 NormalX=0 NormalY=0 NormalZ=1 AngleXU=0 Radius=11
  constraints (34):
    c: Coincident(g0,g1)
    c: Coincident(g1,g2)
    c: Coincident(g2,g3)
    c: Coincident(g3,g4)
    c: Coincident(g4,g5)
    c: Coincident(g5,g0)
    c: Equal(g0, g1-g5) x5
    c: PointOnObject(g0,g6)
    c: PointOnObject(g1,g6)
    c: PointOnObject(g2,g6)
    c: PointOnObject(g3,g6)
    c: PointOnObject(g4,g6)
    c: PointOnObject(g5,g6)
    c: Coincident(g7,g8)
    c: Coincident(g8,g9)
    c: Coincident(g9,g10)
    c: Coincident(g10,g11)
    c: Coincident(g11,g12)
    c: Coincident(g12,g7)
    c: Equal(g7, g8-g12) x5
    c: PointOnObject(g7,g13)
    c: PointOnObject(g8,g13)
    c: PointOnObject(g9,g13)
    c: PointOnObject(g10,g13)
    c: PointOnObject(g11,g13)
    c: PointOnObject(g12,g13)
    c: Horizontal(g6,g13)
    c: Vertical(g6,g2)
    c: DistanceX(g6) = 0
    c: DistanceY(g6) = -256
    c: Diameter(g6) = 22
    c: Vertical(g13,g7)
    c: Diameter(g13) = 22
    c: DistanceX(g13) = 67
FEATURE [Part::Extrusion] Extrude186
  Base = -> Sketch411
  Dir = (0,0,1)
  DirMode = 2
  FaceMakerClass = Part::FaceMakerBullseye
  FaceMakerMode = 3
  LengthFwd = 6
  LengthRev = 0
  Solid = true
  Symmetric = false
FEATURE [Part::MultiFuse] Fusion293  label="pg7Cuts001"
  Shapes = -> [Extrude185,Extrude186]
FEATURE [Sketcher::SketchObject] Sketch412
  ArcFitTolerance = 0
  FullyConstrained = true
  MakeInternals = false
  Placement = pos=(0,-232,0) rot=(1,0,0;1.5708rad)
  sketch-geometry (8):
    g0: LineSegment StartX=-13 StartY=6 StartZ=0 EndX=13 EndY=6 EndZ=0
    g1: LineSegment StartX=13 StartY=6 StartZ=0 EndX=13 EndY=-20 EndZ=0
    g2: LineSegment StartX=13 StartY=-20 StartZ=0 EndX=-13 EndY=-20 EndZ=0
    g3: LineSegment StartX=-13 StartY=-20 StartZ=0 EndX=-13 EndY=6 EndZ=0
    g4: LineSegment StartX=-18 StartY=11 StartZ=0 EndX=18 EndY=11 EndZ=0
    g5: LineSegment StartX=18 StartY=11 StartZ=0 EndX=18 EndY=-25 EndZ=0
    g6: LineSegment StartX=18 StartY=-25 StartZ=0 EndX=-18 EndY=-25 EndZ=0
    g7: LineSegment StartX=-18 StartY=-25 StartZ=0 EndX=-18 EndY=11 EndZ=0
  constraints (24):
    c: Coincident(g0,g1)
    c: Coincident(g1,g2)
    c: Coincident(g2,g3)
    c: Coincident(g3,g0)
    c: Horizontal(g0)
    c: Horizontal(g2)
    c: Vertical(g1)
    c: Vertical(g3)
    c: Coincident(g4,g5)
    c: Coincident(g5,g6)
    c: Coincident(g6,g7)
    c: Coincident(g7,g4)
    c: Horizontal(g4)
    c: Horizontal(g6)
    c: Vertical(g5)
    c: Vertical(g7)
    c: DistanceY(g6) = -25
    c: DistanceX(g2,g1) = 26
    c: DistanceX(g6) = -18
    c: DistanceX(g6,g2) = 5
    c: DistanceX(g5) = 18
    c: DistanceY(g2,g0) = 26
    c: DistanceY(g6,g2) = 5
    c: DistanceY(g0,g4) = 5
FEATURE [Part::Extrusion] Extrude187
  Base = -> Sketch412
  Dir = (0,-1,2e-16)
  DirMode = 2
  FaceMakerClass = Part::FaceMakerBullseye
  FaceMakerMode = 3
  LengthFwd = 32
  LengthRev = 0
  Reversed = true
  Solid = true
  Symmetric = false
FEATURE [Sketcher::SketchObject] Sketch413
  ArcFitTolerance = 0
  FullyConstrained = true
  MakeInternals = false
  Placement = pos=(0,0,11) rot=(0,0,1;0rad)
  sketch-geometry (1):
    g0: Circle CenterX=0 CenterY=-215 CenterZ=0 NormalX=0 NormalY=0 NormalZ=1 AngleXU=0 Radius=3.125
  constraints (3):
    c: DistanceX(g0) = 0
    c: DistanceY(g0) = -215
    c: Diameter(g0) = 6.25
FEATURE [Part::Extrusion] Extrude189
  Base = -> Sketch413
  Dir = (0,0,1)
  DirMode = 2
  FaceMakerClass = Part::FaceMakerBullseye
  FaceMakerMode = 3
  LengthFwd = 36
  LengthRev = 0
  Reversed = true
  Solid = true
  Symmetric = false
FEATURE [Sketcher::SketchObject] Sketch414
  ArcFitTolerance = 0
  FullyConstrained = true
  MakeInternals = false
  Placement = pos=(-18,0,0) rot=(0.57735,0.57735,0.57735;2.0944rad)
  sketch-geometry (1):
    g0: Circle CenterX=-215 CenterY=-7 CenterZ=0 NormalX=0 NormalY=0 NormalZ=1 AngleXU=0 Radius=3.25
  constraints (3):
    c: DistanceX(g0) = -215
    c: DistanceY(g0) = -7
    c: Diameter(g0) = 6.5
FEATURE [Part::Extrusion] Extrude188
  Base = -> Sketch414
  Dir = (1,0,0)
  DirMode = 2
  FaceMakerClass = Part::FaceMakerBullseye
  FaceMakerMode = 3
  LengthFwd = 36
  LengthRev = 0
  Solid = true
  Symmetric = false
FEATURE [Part::MultiFuse] Fusion292
  Shapes = -> [Extrude189,Extrude188]
FEATURE [Part::Cut] Cut158  label="in004"
  Base = -> Extrude187
  Tool = -> Fusion292
FEATURE [Part::Fillet] Fillet262
  Base = -> Cut158
  EdgeLinks = -> Cut158 [?Edge1,?Edge4,?Edge6,?Edge22]
  Edges = 4 edges r=2: [Edge1,Edge4,Edge6,Edge22]
FEATURE [Part::Fillet] Fillet263  label="tSlotHolder001"
  Base = -> Fillet262
  EdgeLinks = -> Fillet262 [Edge4,Edge18,Edge20,Edge21,Edge22,Edge23,Edge24,Edge25,Edge26,Edge27,Edge28,Edge29]
  Edges = 12 edges r=2: [Edge4,Edge18,Edge20,Edge21,Edge22,Edge23,Edge24,Edge25,Edge26,Edge27,Edge28,Edge29]
FEATURE [Sketcher::SketchObject] Sketch415
  ArcFitTolerance = 0
  FullyConstrained = true
  MakeInternals = false
  Placement = pos=(0,0,-25) rot=(0,0,1;0rad)
  sketch-geometry (2):
    g0: Circle CenterX=0 CenterY=-256 CenterZ=0 NormalX=0 NormalY=0 NormalZ=1 AngleXU=0 Radius=6
    g1: Circle CenterX=67 CenterY=-256 CenterZ=0 NormalX=0 NormalY=0 NormalZ=1 AngleXU=0 Radius=6
  constraints (6):
    c: DistanceY(g0) = -256
    c: Horizontal(g0,g1)
    c: DistanceX(g0,g1) = 67
    c: DistanceX(g0) = 0
    c: Equal(g0,g1)
    c: Diameter(g0) = 12
FEATURE [Part::Extrusion] Extrude190  label="outCut001"
  Base = -> Sketch415
  Dir = (0,0,1)
  DirMode = 2
  FaceMakerClass = Part::FaceMakerBullseye
  FaceMakerMode = 3
  LengthFwd = 5
  LengthRev = 0
  Solid = true
  Symmetric = false
FEATURE [Part::MultiFuse] Fusion297  label="mainCuts001"
  Shapes = -> [Fusion293,Fusion291,Extrude190,Extrude184]
FEATURE [Sketcher::SketchObject] Sketch416
  ArcFitTolerance = 0
  FullyConstrained = true
  MakeInternals = false
  Placement = pos=(0,0,-25) rot=(0,0,1;0rad)
  sketch-geometry (8):
    g0: ArcOfCircle CenterX=-80 CenterY=-270 CenterZ=0 NormalX=0 NormalY=0 NormalZ=1 AngleXU=0 Radius=40 StartAngle=1.5708 EndAngle=4.71239
    g1: ArcOfCircle CenterX=80 CenterY=-270 CenterZ=0 NormalX=0 NormalY=0 NormalZ=1 AngleXU=0 Radius=40 StartAngle=4.71239 EndAngle=7.85398
    g2: LineSegment StartX=-80 StartY=-310 StartZ=0 EndX=80 EndY=-310 EndZ=0
    g3: LineSegment StartX=80 StartY=-230 StartZ=0 EndX=-80 EndY=-230 EndZ=0
    g4: ArcOfCircle CenterX=-80 CenterY=-270 CenterZ=0 NormalX=0 NormalY=0 NormalZ=1 AngleXU=0 Radius=30 StartAngle=1.5708 EndAngle=4.71239
    g5: ArcOfCircle CenterX=80 CenterY=-270 CenterZ=0 NormalX=0 NormalY=0 NormalZ=1 AngleXU=0 Radius=30 StartAngle=4.71239 EndAngle=7.85398
    g6: LineSegment StartX=-80 StartY=-300 StartZ=0 EndX=80 EndY=-300 EndZ=0
    g7: LineSegment StartX=80 StartY=-240 StartZ=0 EndX=-80 EndY=-240 EndZ=0
  constraints (18):
    c: Tangent(g0,g2) = -1.5708
    c: Tangent(g2,g1) = -1.5708
    c: Tangent(g1,g3) = -1.5708
    c: Tangent(g3,g0) = -1.5708
    c: Equal(g0,g1)
    c: Horizontal(g2)
    c: DistanceY(g0) = -270
    c: DistanceX(g0) = -80
    c: DistanceX(g1) = 80
    c: Diameter(g0) = 80
    c: Tangent(g4,g6) = -1.5708
    c: Tangent(g6,g5) = -1.5708
    c: Tangent(g5,g7) = -1.5708
    c: Tangent(g7,g4) = -1.5708
    c: Equal(g4,g5)
    c: Coincident(g4,g0)
    c: Coincident(g5,g1)
    c: Diameter(g4) = 60
FEATURE [Part::Extrusion] Extrude192  label="outerBorder002"
  Base = -> Sketch416
  Dir = (0,0,1)
  DirMode = 2
  FaceMakerClass = Part::FaceMakerBullseye
  FaceMakerMode = 3
  LengthFwd = 53
  LengthRev = 0
  Solid = true
  Symmetric = false
FEATURE [Part::Fillet] Fillet264  label="outerHold002"
  Base = -> Extrude192
  EdgeLinks = -> Extrude192 [Edge9]
  Edges = 1 edges r=4: [Edge9]
FEATURE [Sketcher::SketchObject] Sketch417
  ArcFitTolerance = 0
  FullyConstrained = true
  MakeInternals = false
  Placement = pos=(0,0,-25) rot=(0,0,1;0rad)
  sketch-geometry (8):
    g0: ArcOfCircle CenterX=-80 CenterY=-270 CenterZ=0 NormalX=0 NormalY=0 NormalZ=1 AngleXU=0 Radius=30 StartAngle=5.55346 EndAngle=7.01291
    g1: LineSegment StartX=-57.6393 StartY=-250 StartZ=0 EndX=-22.3607 EndY=-250 EndZ=0
    g2: LineSegment StartX=-57.6393 StartY=-290 StartZ=0 EndX=-22.3607 EndY=-290 EndZ=0
    g3: ArcOfCircle CenterX=0 CenterY=-270 CenterZ=0 NormalX=0 NormalY=0 NormalZ=1 AngleXU=0 Radius=30 StartAngle=2.41186 EndAngle=3.87132
    g4: ArcOfCircle CenterX=0 CenterY=-270 CenterZ=0 NormalX=0 NormalY=0 NormalZ=1 AngleXU=0 Radius=30 StartAngle=5.55346 EndAngle=7.01291
    g5: ArcOfCircle CenterX=80 CenterY=-270 CenterZ=0 NormalX=0 NormalY=0 NormalZ=1 AngleXU=0 Radius=30 StartAngle=2.41186 EndAngle=3.87132
    g6: LineSegment StartX=22.3607 StartY=-250 StartZ=0 EndX=57.6393 EndY=-250 EndZ=0
    g7: LineSegment StartX=57.6393 StartY=-290 StartZ=0 EndX=22.3607 EndY=-290 EndZ=0
  constraints (27):
    c: Coincident(g1,g0)
    c: Horizontal(g1)
    c: Coincident(g2,g0)
    c: Horizontal(g2)
    c: PointOnObject(g3,g-2)
    c: Coincident(g3,g2)
    c: Coincident(g3,g1)
    c: Coincident(g4,g3)
    c: Coincident(g6,g4)
    c: Coincident(g6,g5)
    c: Horizontal(g6)
    c: Coincident(g7,g5)
    c: Coincident(g7,g4)
    c: Horizontal(g7)
    c: Horizontal(g0,g4)
    c: Horizontal(g2,g4)
    c: Equal(g3,g0)
    c: Equal(g3,g5)
    c: Equal(g3,g4)
    c: Diameter(g3) = 60
    c: DistanceY(g3) = -270
    c: Vertical(g0,g0)
    c: Vertical(g2,g1)
    c: Vertical(g5,g5)
    c: DistanceX(g5) = 80
    c: DistanceX(g0) = -80
    c: DistanceY(g4) = -250
FEATURE [Part::Extrusion] Extrude193  label="3WayHolds002"
  Base = -> Sketch417
  Dir = (0,0,1)
  DirMode = 2
  FaceMakerClass = Part::FaceMakerBullseye
  FaceMakerMode = 3
  LengthFwd = 53
  LengthRev = 0
  Solid = true
  Symmetric = false
FEATURE [Sketcher::SketchObject] Sketch418
  ArcFitTolerance = 0
  FullyConstrained = true
  MakeInternals = false
  Placement = pos=(0,0,-20) rot=(0,0,1;0rad)
  sketch-geometry (18):
    g0: ArcOfCircle CenterX=-80 CenterY=-240 CenterZ=0 NormalX=0 NormalY=0 NormalZ=1 AngleXU=0 Radius=20 StartAngle=3.48143 EndAngle=5.94335
    g1: ArcOfCircle CenterX=-80 CenterY=-300 CenterZ=0 NormalX=0 NormalY=0 NormalZ=1 AngleXU=0 Radius=20 StartAngle=0.339837 EndAngle=2.80176
    g2: ArcOfCircle CenterX=-80 CenterY=-270 CenterZ=0 NormalX=0 NormalY=0 NormalZ=1 AngleXU=0 Radius=30 StartAngle=0.891123 EndAngle=2.25047
    g3: ArcOfCircle CenterX=-80 CenterY=-270 CenterZ=0 NormalX=0 NormalY=0 NormalZ=1 AngleXU=0 Radius=30 StartAngle=4.03272 EndAngle=5.39206
    g4: LineSegment StartX=65 StartY=-286 StartZ=0 EndX=95 EndY=-286 EndZ=0
    g5: LineSegment StartX=95 StartY=-286 StartZ=0 EndX=95 EndY=-254 EndZ=0
    g6: LineSegment StartX=95 StartY=-254 StartZ=0 EndX=77 EndY=-254 EndZ=0
    g7: LineSegment StartX=77 StartY=-254 StartZ=0 EndX=77 EndY=-274 EndZ=0
    g8: LineSegment StartX=77 StartY=-274 StartZ=0 EndX=65 EndY=-274 EndZ=0
    g9: LineSegment StartX=65 StartY=-274 StartZ=0 EndX=65 EndY=-286 EndZ=0
    g10: Circle CenterX=-90 CenterY=-252.5 CenterZ=0 NormalX=0 NormalY=0 NormalZ=1 AngleXU=0 Radius=2
    g11: Circle CenterX=-70 CenterY=-252.5 CenterZ=0 NormalX=0 NormalY=0 NormalZ=1 AngleXU=0 Radius=2
    g12: Circle CenterX=-90 CenterY=-287.5 CenterZ=0 NormalX=0 NormalY=0 NormalZ=1 AngleXU=0 Radius=2
    g13: Circle CenterX=-70 CenterY=-287.5 CenterZ=0 NormalX=0 NormalY=0 NormalZ=1 AngleXU=0 Radius=2
    g14: Circle CenterX=69.84 CenterY=-280.6 CenterZ=0 NormalX=0 NormalY=0 NormalZ=1 AngleXU=0 Radius=1.6
    g15: Circle CenterX=90.16 CenterY=-280.6 CenterZ=0 NormalX=0 NormalY=0 NormalZ=1 AngleXU=0 Radius=1.6
    g16: Circle CenterX=90.16 CenterY=-267.9 CenterZ=0 NormalX=0 NormalY=0 NormalZ=1 AngleXU=0 Radius=1.6
    g17: Circle CenterX=86.5 CenterY=-259.25 CenterZ=0 NormalX=0 NormalY=0 NormalZ=1 AngleXU=0 Radius=1.6
  constraints (57):
    c: Vertical(g0,g1)
    c: Coincident(g2,g0)
    c: Coincident(g3,g2)
    c: Coincident(g3,g1)
    c: Coincident(g0,g2)
    c: Coincident(g1,g3)
    c: DistanceX(g2) = -80
    c: DistanceY(g2) = -270
    c: Equal(g3,g2)
    c: Diameter(g3) = 60
    c: Equal(g0,g1)
    c: Diameter(g0) = 40
    c: Vertical(g0,g2)
    c: DistanceY(g0) = -240
    c: DistanceY(g1) = -300
    c: Horizontal(g4)
    c: Coincident(g5,g4)
    c: Vertical(g5)
    c: Coincident(g6,g5)
    c: Horizontal(g6)
    c: Coincident(g7,g6)
    c: Vertical(g7)
    c: Coincident(g8,g7)
    c: Horizontal(g8)
    c: Coincident(g9,g8)
    c: Coincident(g9,g4)
    c: Vertical(g9)
    c: DistanceY(g4) = -286
    c: DistanceX(g4) = 65
    c: DistanceY(g4,g8) = 12
    c: DistanceX(g4,g4) = 30
    c: DistanceX(g6,g6) = 18
    c: DistanceY(g5,g5) = 32
    c: Horizontal(g13,g12)
    c: Horizontal(g10,g11)
    c: Vertical(g12,g10)
    c: Vertical(g13,g11)
    c: DistanceX(g12,g2) = 10
    c: DistanceY(g12) = -287.5
    c: DistanceX(g12,g13) = 20
    c: DistanceY(g12,g10) = 35
    c: Equal(g10,g11)
    c: Equal(g10,g13)
    c: Equal(g10,g12)
    c: Diameter(g10) = 4
    c: Horizontal(g14,g15)
    c: Vertical(g15,g16)
    c: DistanceX(g14,g15) = 20.32
    c: DistanceY(g14) = -280.6
    c: DistanceY(g15,g16) = 12.7
    c: DistanceX(g17,g16) = 3.66
    c: DistanceY(g16,g17) = 8.65
    c: Equal(g15,g16)
    c: Equal(g15,g17)
    c: Equal(g15,g14)
    c: Diameter(g15) = 3.2
    c: DistanceX(g4,g14) = 4.84
FEATURE [Part::Extrusion] Extrude194  label="i2cHolds002"
  Base = -> Sketch418
  Dir = (0,0,1)
  DirMode = 2
  FaceMakerClass = Part::FaceMakerBullseye
  FaceMakerMode = 3
  LengthFwd = 48
  LengthRev = 0
  Solid = true
  Symmetric = false
FEATURE [Sketcher::SketchObject] Sketch419
  ArcFitTolerance = 0
  FullyConstrained = true
  MakeInternals = false
  Placement = pos=(0,0,-20) rot=(0,0,1;0rad)
  sketch-geometry (12):
    g0: ArcOfCircle CenterX=-20 CenterY=-290 CenterZ=0 NormalX=0 NormalY=0 NormalZ=1 AngleXU=0 Radius=10 StartAngle=5.49779 EndAngle=8.63938
    g1: ArcOfCircle CenterX=20 CenterY=-290 CenterZ=0 NormalX=0 NormalY=0 NormalZ=1 AngleXU=0 Radius=10 StartAngle=0.785398 EndAngle=3.92699
    g2: ArcOfCircle CenterX=20 CenterY=-250 CenterZ=0 NormalX=0 NormalY=0 NormalZ=1 AngleXU=0 Radius=10 StartAngle=2.35619 EndAngle=5.49779
    g3: ArcOfCircle CenterX=-20 CenterY=-250 CenterZ=0 NormalX=0 NormalY=0 NormalZ=1 AngleXU=0 Radius=10 StartAngle=3.92699 EndAngle=7.06858
    g4: ArcOfCircle CenterX=0 CenterY=-270 CenterZ=0 NormalX=0 NormalY=0 NormalZ=1 AngleXU=0 Radius=30 StartAngle=2.01636 EndAngle=2.69603
    g5: ArcOfCircle CenterX=0 CenterY=-270 CenterZ=0 NormalX=0 NormalY=0 NormalZ=1 AngleXU=0 Radius=30 StartAngle=0.445561 EndAngle=1.12524
    g6: ArcOfCircle CenterX=0 CenterY=-270 CenterZ=0 NormalX=0 NormalY=0 NormalZ=1 AngleXU=0 Radius=30 StartAngle=5.15795 EndAngle=5.83762
    g7: ArcOfCircle CenterX=0 CenterY=-270 CenterZ=0 NormalX=0 NormalY=0 NormalZ=1 AngleXU=0 Radius=30 StartAngle=3.58715 EndAngle=4.26683
    g8: Circle CenterX=-17 CenterY=-253 CenterZ=0 NormalX=0 NormalY=0 NormalZ=1 AngleXU=0 Radius=1.6
    g9: Circle CenterX=17 CenterY=-253 CenterZ=0 NormalX=0 NormalY=0 NormalZ=1 AngleXU=0 Radius=1.6
    g10: Circle CenterX=17 CenterY=-287 CenterZ=0 NormalX=0 NormalY=0 NormalZ=1 AngleXU=0 Radius=1.6
    g11: Circle CenterX=-17 CenterY=-287 CenterZ=0 NormalX=0 NormalY=0 NormalZ=1 AngleXU=0 Radius=1.6
  constraints (41):
    c: Vertical(g0,g3)
    c: Vertical(g1,g2)
    c: Horizontal(g2,g3)
    c: Horizontal(g1,g0)
    c: Equal(g2,g3)
    c: Equal(g2,g0)
    c: Equal(g2,g1)
    c: Diameter(g2) = 20
    c: Horizontal(g0,g1)
    c: Horizontal(g1,g0)
    c: Angle(g0) = 3.14159
    c: Vertical(g0,g3)
    c: Vertical(g0,g3)
    c: Angle(g2) = 3.14159
    c: DistanceY(g0) = -290
    c: Coincident(g4,g3)
    c: Coincident(g4,g3)
    c: Coincident(g5,g4)
    c: Coincident(g5,g2)
    c: Coincident(g5,g2)
    c: Coincident(g6,g4)
    c: Coincident(g6,g1)
    c: Coincident(g6,g1)
    c: Coincident(g7,g4)
    c: Coincident(g7,g0)
    c: Coincident(g7,g0)
    c: DistanceX(g4) = 0
    c: DistanceY(g4) = -270
    c: DistanceX(g0,g4) = 20
    c: DistanceX(g11,g4) = 17
    c: DistanceY(g11,g4) = 17
    c: DistanceX(g4,g10) = 17
    c: DistanceY(g10,g4) = 17
    c: DistanceX(g4,g9) = 17
    c: Vertical(g8,g11)
    c: Horizontal(g8,g9)
    c: DistanceY(g4,g8) = 17
    c: Equal(g10,g9)
    c: Equal(g10,g8)
    c: Equal(g10,g11)
    c: Diameter(g10) = 3.2
FEATURE [Part::Extrusion] Extrude195  label="cameraHold002"
  Base = -> Sketch419
  Dir = (0,0,1)
  DirMode = 2
  FaceMakerClass = Part::FaceMakerBullseye
  FaceMakerMode = 3
  LengthFwd = 31
  LengthRev = 0
  Solid = true
  Symmetric = false
FEATURE [Sketcher::SketchObject] Sketch420
  ArcFitTolerance = 0
  FullyConstrained = true
  MakeInternals = false
  Placement = pos=(85,0,0) rot=(0.57735,0.57735,0.57735;2.0944rad)
  sketch-geometry (2):
    g0: ArcOfCircle CenterX=-270 CenterY=-20 CenterZ=0 NormalX=0 NormalY=0 NormalZ=1 AngleXU=0 Radius=15 StartAngle=0 EndAngle=3.14159
    g1: LineSegment StartX=-285 StartY=-20 StartZ=0 EndX=-255 EndY=-20 EndZ=0
  constraints (7):
    c: Horizontal(g0,g0)
    c: Horizontal(g0,g0)
    c: DistanceX(g0) = -270
    c: DistanceY(g0) = -20
    c: Diameter(g0) = 30
    c: Coincident(g1,g0)
    c: Coincident(g1,g0)
FEATURE [Part::Extrusion] Extrude196  label="WireCutcut004"
  Base = -> Sketch420
  Dir = (1,0,0)
  DirMode = 2
  FaceMakerClass = Part::FaceMakerBullseye
  FaceMakerMode = 3
  LengthFwd = 170
  LengthRev = 0
  Reversed = true
  Solid = true
  Symmetric = false
FEATURE [Sketcher::SketchObject] Sketch421
  ArcFitTolerance = 0
  FullyConstrained = true
  MakeInternals = false
  Placement = pos=(0,0,-25) rot=(0,0,1;0rad)
  sketch-geometry (3):
    g0: Circle CenterX=-80 CenterY=-270.2 CenterZ=0 NormalX=0 NormalY=0 NormalZ=1 AngleXU=0 Radius=40
    g1: Circle CenterX=0 CenterY=-270.2 CenterZ=0 NormalX=0 NormalY=0 NormalZ=1 AngleXU=0 Radius=40
    g2: Circle CenterX=80 CenterY=-270.2 CenterZ=0 NormalX=0 NormalY=0 NormalZ=1 AngleXU=0 Radius=40
  constraints (9):
    c: PointOnObject(g1,g-2)
    c: Diameter(g1) = 80
    c: Diameter(g0) = 80
    c: Horizontal(g1,g0)
    c: DistanceY(g0) = -270.2
    c: DistanceX(g0) = -80
    c: Horizontal(g2,g1)
    c: Diameter(g2) = 80
    c: DistanceX(g1,g2) = 80
FEATURE [Part::Extrusion] Extrude197  label="base008"
  Base = -> Sketch421
  Dir = (0,0,1)
  DirMode = 2
  FaceMakerClass = Part::FaceMakerBullseye
  FaceMakerMode = 3
  LengthFwd = 5
  LengthRev = 0
  Solid = true
  Symmetric = false
FEATURE [Part::Fillet] Fillet265  label="base009"
  Base = -> Extrude197
  EdgeLinks = -> Extrude197 [Edge2,Edge5,Edge8]
  Edges = 3 edges r=4: [Edge2,Edge5,Edge8]
FEATURE [Sketcher::SketchObject] Sketch422
  ArcFitTolerance = 0
  FullyConstrained = true
  MakeInternals = false
  Placement = pos=(0,0,-20) rot=(0,0,1;0rad)
  sketch-geometry (2):
    g0: Circle CenterX=0 CenterY=-270 CenterZ=0 NormalX=0 NormalY=0 NormalZ=1 AngleXU=0 Radius=30
    g1: Circle CenterX=0 CenterY=-270 CenterZ=0 NormalX=0 NormalY=0 NormalZ=1 AngleXU=0 Radius=40
  constraints (5):
    c: PointOnObject(g0,g-2)
    c: Coincident(g1,g0)
    c: DistanceY(g0) = -270
    c: Diameter(g0) = 60
    c: Diameter(g1) = 80
FEATURE [Part::Extrusion] Extrude198  label="domeHolds008"
  Base = -> Sketch422
  Dir = (0,0,1)
  DirMode = 2
  FaceMakerClass = Part::FaceMakerBullseye
  FaceMakerMode = 3
  LengthFwd = 48
  LengthRev = 0
  Solid = true
  Symmetric = false
FEATURE [Sketcher::SketchObject] Sketch423
  ArcFitTolerance = 0
  FullyConstrained = true
  MakeInternals = false
  Placement = pos=(0,0,-20) rot=(0,0,1;0rad)
  sketch-geometry (2):
    g0: Circle CenterX=0 CenterY=-270 CenterZ=0 NormalX=0 NormalY=0 NormalZ=1 AngleXU=0 Radius=30
    g1: Circle CenterX=0 CenterY=-270 CenterZ=0 NormalX=0 NormalY=0 NormalZ=1 AngleXU=0 Radius=40
  constraints (5):
    c: PointOnObject(g0,g-2)
    c: Coincident(g1,g0)
    c: DistanceY(g0) = -270
    c: Diameter(g0) = 60
    c: Diameter(g1) = 80
FEATURE [Part::Extrusion] Extrude199  label="domeHolds009"
  Base = -> Sketch423
  Dir = (0,0,1)
  DirMode = 2
  FaceMakerClass = Part::FaceMakerBullseye
  FaceMakerMode = 3
  LengthFwd = 48
  LengthRev = 0
  Placement = pos=(80,0,0) rot=(0,0,1;0rad)
  Solid = true
  Symmetric = false
FEATURE [Sketcher::SketchObject] Sketch424
  ArcFitTolerance = 0
  FullyConstrained = true
  MakeInternals = false
  Placement = pos=(0,0,-20) rot=(0,0,1;0rad)
  sketch-geometry (2):
    g0: Circle CenterX=0 CenterY=-270 CenterZ=0 NormalX=0 NormalY=0 NormalZ=1 AngleXU=0 Radius=30
    g1: Circle CenterX=0 CenterY=-270 CenterZ=0 NormalX=0 NormalY=0 NormalZ=1 AngleXU=0 Radius=40
  constraints (5):
    c: PointOnObject(g0,g-2)
    c: Coincident(g1,g0)
    c: DistanceY(g0) = -270
    c: Diameter(g0) = 60
    c: Diameter(g1) = 80
FEATURE [Part::Extrusion] Extrude200  label="domeHolds010"
  Base = -> Sketch424
  Dir = (0,0,1)
  DirMode = 2
  FaceMakerClass = Part::FaceMakerBullseye
  FaceMakerMode = 3
  LengthFwd = 48
  LengthRev = 0
  Placement = pos=(-80,0,0) rot=(0,0,1;0rad)
  Solid = true
  Symmetric = false
FEATURE [Part::MultiFuse] Fusion294  label="domeHolds011"
  Shapes = -> [Extrude198,Extrude199,Extrude200]
FEATURE [Part::MultiFuse] Fusion295  label="mainLightModule015"
  Shapes = -> [Fillet265,Fillet264,Fusion294,Extrude193]
FEATURE [Part::Fillet] Fillet266  label="mainLightModule013"
  Base = -> Fusion295
  EdgeLinks = -> Fusion295 [Edge124,Edge127,Edge206,Edge218,Edge219,Edge220,Edge265,Edge268,Edge277,Edge279,Edge280,Edge281,Edge295,Edge297,Edge301,Edge302,Edge303]
  Edges = 17 edges r=4: [Edge124,Edge127,Edge206,Edge218,Edge219,Edge220,Edge265,Edge268,Edge277,Edge279,Edge280,Edge281,Edge295,Edge297,Edge301,Edge302,Edge303]
FEATURE [Part::Cut] Cut159  label="mainLightModule011"
  Base = -> Fillet266
  Tool = -> Extrude196
FEATURE [Part::MultiFuse] Fusion296  label="mainLightModule016"
  Shapes = -> [Cut159,Extrude194,Extrude195]
FEATURE [Part::Cut] Cut160  label="mainLightModule012"
  Base = -> Fusion296
  Tool = -> Fusion297
FEATURE [Part::MultiFuse] Fusion298  label="mainLightModule017"
  Shapes = -> [Extrude191,Cut160,Fillet263]
FEATURE [Part::Fillet] Fillet267
  Base = -> Fusion298
  EdgeLinks = -> Fusion298 [Edge277,Edge279,Edge489,Edge491]
  Edges = 4 edges r=4: [Edge277,Edge279,Edge489,Edge491]
FEATURE [Part::Fillet] Fillet268  label="mainLightModule014"
  Base = -> Fillet267
  EdgeLinks = -> Fillet267 [Edge555,Edge744,Edge745,Edge897,Edge898,Edge1054]
  Edges = 6 edges r=1: [Edge555,Edge744,Edge745,Edge897,Edge898,Edge1054]
FEATURE [Part::Sphere] Sphere017  label="Sphere_out008"
  Angle1 = -90
  Angle2 = 90
  Angle3 = 180
  AttacherType = Attacher::AttachEngine3D
  Placement = pos=(0,0,0) rot=(1,0,0;1.5708rad)
  Radius = 30
FEATURE [Part::Sphere] Sphere018  label="Sphere_in008"
  Angle1 = -90
  Angle2 = 90
  Angle3 = 180
  AttacherType = Attacher::AttachEngine3D
  Placement = pos=(0,0,0) rot=(1,0,0;1.5708rad)
  Radius = 28.7
FEATURE [Part::Cut] Cut149  label="Dome008"
  Base = -> Sphere017
  Tool = -> Sphere018
FEATURE [Part::MultiFuse] Fusion262  label="dome009"
  Shapes = -> [Cut149,Cut150]
FEATURE [Part::Cut] Cut151  label="dome006"
  Base = -> Fusion262
  Placement = pos=(0,-270,30.5) rot=(0,0,1;0rad)
  Tool = -> Extrude177
FEATURE [Part::Sphere] Sphere019  label="Sphere_out009"
  Angle1 = -90
  Angle2 = 90
  Angle3 = 180
  AttacherType = Attacher::AttachEngine3D
  Placement = pos=(0,0,0) rot=(1,0,0;1.5708rad)
  Radius = 30
FEATURE [Part::Sphere] Sphere020  label="Sphere_in009"
  Angle1 = -90
  Angle2 = 90
  Angle3 = 180
  AttacherType = Attacher::AttachEngine3D
  Placement = pos=(0,0,0) rot=(1,0,0;1.5708rad)
  Radius = 28.7
FEATURE [Part::Cut] Cut152  label="Dome009"
  Base = -> Sphere019
  Tool = -> Sphere020
FEATURE [Part::MultiFuse] Fusion263  label="dome010"
  Shapes = -> [Cut152,Cut153]
FEATURE [Part::Cut] Cut154  label="dome007"
  Base = -> Fusion263
  Placement = pos=(-80,-270,30.5) rot=(0,0,1;0rad)
  Tool = -> Extrude178
FEATURE [Part::Sphere] Sphere021  label="Sphere_out010"
  Angle1 = -90
  Angle2 = 90
  Angle3 = 180
  AttacherType = Attacher::AttachEngine3D
  Placement = pos=(0,0,0) rot=(1,0,0;1.5708rad)
  Radius = 30
FEATURE [Part::Sphere] Sphere022  label="Sphere_in010"
  Angle1 = -90
  Angle2 = 90
  Angle3 = 180
  AttacherType = Attacher::AttachEngine3D
  Placement = pos=(0,0,0) rot=(1,0,0;1.5708rad)
  Radius = 28.7
FEATURE [Part::Cut] Cut155  label="Dome010"
  Base = -> Sphere021
  Tool = -> Sphere022
FEATURE [Part::MultiFuse] Fusion264  label="dome011"
  Shapes = -> [Cut155,Cut156]
FEATURE [Part::Cut] Cut157  label="dome008"
  Base = -> Fusion264
  Placement = pos=(80,-270,30.5) rot=(0,0,1;0rad)
  Tool = -> Extrude179
FEATURE [Part::Compound] Compound004  label="domesAndSeals001"
  Links = -> [Cut151,Cut154,Cut157,Extrude180,Extrude181,Extrude182]
FEATURE [App::Part] sot_23_6_v004  label="sot-23-6 v004"
  Group = -> [Part__Feature381,Part__Feature382,Part__Feature383,Part__Feature384,Part__Feature385,Part__Feature386,Part__Feature387]
  Origin = -> Origin015
  Placement = pos=(-4.47945,-0.603742,1.69152) rot=(0,0,1;0rad)
FEATURE [App::Part] Adafruit_AS7341_STEMMA_QT_v004  label="ltr392"
  Group = -> [Part__Feature374,Part__Feature375,Part__Feature376,Part__Feature377,Part__Feature378,Part__Feature379,Part__Feature380,sot_23_6_v004,Part__Feature388,Part__Feature389,Part__Feature390,Part__Feature391,Part__Feature392,Part__Feature393,Part__Feature394]
  Origin = -> Origin016
  Placement = pos=(80,-274.25,28) rot=(0,0,1;0rad)
FEATURE [Part::Compound] Compound003  label="setItems001"
  Links = -> [Part__Feature395,Cut148,Adafruit_AS7341_STEMMA_QT_v004,Clone053,Compound004,Extrude183,Adafruit_INA219_STEMMA_QT_v008,PG7_Gland004,PG7_Gland003]
FEATURE [Part::Compound] Compound005  label="lightModule"
  Links = -> [Fillet268,Compound003]
  Placement = pos=(0,0,561) rot=(0,0,1;0rad)
FEATURE [Part::Compound] Compound006  label="SRS"
  Links = -> [Fusion175]
FEATURE [Part::Compound] Compound007
  Links = -> [ZH_161407_33,Cut137,Part__Feature329,Clone,Clone001,Box,Part__Feature,Compound,Cut043,Cut045,Cut051,Adafruit_AS7341_STEMMA_QT_v2,Box005,Cut018,Part__Feature330,Fusion003,Part__Feature331,Compound001,Fillet017,Compound005,Compound006]
